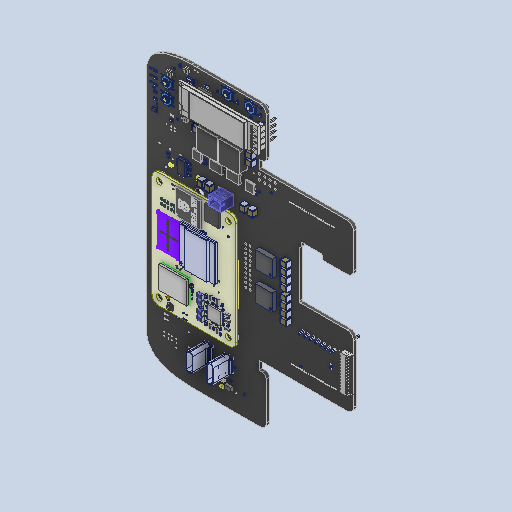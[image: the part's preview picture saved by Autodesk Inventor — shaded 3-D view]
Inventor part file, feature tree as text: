
AUTODESK INVENTOR PART (.ipt)
format: ipt  version: 2022 (Build 260153000, 153)  size: 57,300,480 bytes
history: native  units: mm
features: other x3626, sketch x2448, extrude x2
ambient origin geometry x8: Origin, YZ Plane, XZ Plane, XY Plane, X Axis, Y Axis, Z Axis, Center Point
bodies: Body1 (feature_tree), Body2 (feature_tree), Body3 (feature_tree), Body4 (feature_tree), Body5 (feature_tree), Body6 (feature_tree), Body7 (feature_tree), Body8 (feature_tree), Body9 (feature_tree), Body10 (feature_tree), Body11 (feature_tree), Body12 (feature_tree), Body13 (feature_tree), Body14 (feature_tree), Body15 (feature_tree), Body16 (feature_tree), Body17 (feature_tree), Body18 (feature_tree), Body19 (feature_tree), Body20 (feature_tree), Body21 (feature_tree), Body22 (feature_tree), Body23 (feature_tree), Body24 (feature_tree), Body25 (feature_tree), Body26 (feature_tree), Body27 (feature_tree), Body28 (feature_tree), Body29 (feature_tree), Body30 (feature_tree), Body31 (feature_tree), Body32 (feature_tree), Body33 (feature_tree), Body34 (feature_tree), Body35 (feature_tree), Body36 (feature_tree), Body37 (feature_tree), Body38 (feature_tree), Body39 (feature_tree), Body40 (feature_tree), Body41 (feature_tree), Body42 (feature_tree), Body43 (feature_tree), Body44 (feature_tree), Body45 (feature_tree), Body46 (feature_tree), Body47 (feature_tree), Body48 (feature_tree), Body49 (feature_tree), Body50 (feature_tree), Body51 (feature_tree), Body52 (feature_tree), Body53 (feature_tree), Body54 (feature_tree), Body55 (feature_tree), Body56 (feature_tree), Body57 (feature_tree), Body58 (feature_tree), Body59 (feature_tree), Body60 (feature_tree), Body61 (feature_tree), Body62 (feature_tree), Body63 (feature_tree), Body64 (feature_tree), Body65 (feature_tree), Body66 (feature_tree), Body67 (feature_tree), Body68 (feature_tree), Body69 (feature_tree), Body70 (feature_tree), Body71 (feature_tree), Body72 (feature_tree), Body73 (feature_tree), Body74 (feature_tree), Body75 (feature_tree), Body76 (feature_tree), Body77 (feature_tree), Body78 (feature_tree), Body79 (feature_tree), Body80 (feature_tree), Body81 (feature_tree), Body82 (feature_tree), Body83 (feature_tree), Body84 (feature_tree), Body85 (feature_tree), Body86 (feature_tree), Body87 (feature_tree), Body88 (feature_tree), Body89 (feature_tree), Body90 (feature_tree), Body91 (feature_tree), Body92 (feature_tree), Body93 (feature_tree), Body94 (feature_tree), Body95 (feature_tree), Body96 (feature_tree), Body97 (feature_tree), Body98 (feature_tree), Body99 (feature_tree), Body100 (feature_tree), Body101 (feature_tree), Body102 (feature_tree), Body103 (feature_tree), Body104 (feature_tree), Body105 (feature_tree), Body106 (feature_tree), Body107 (feature_tree), Body108 (feature_tree), Body109 (feature_tree), Body110 (feature_tree), Body111 (feature_tree), Body112 (feature_tree), Body113 (feature_tree), Body114 (feature_tree), Body115 (feature_tree), Body116 (feature_tree), Body117 (feature_tree), Body118 (feature_tree), Body119 (feature_tree), Body120 (feature_tree), Body121 (feature_tree), Body122 (feature_tree), Body123 (feature_tree), Body124 (feature_tree), Body125 (feature_tree), Body126 (feature_tree), Body127 (feature_tree), Body128 (feature_tree), Body129 (feature_tree), Body130 (feature_tree), Body131 (feature_tree), Body132 (feature_tree), Body133 (feature_tree), Body134 (feature_tree), Body135 (feature_tree), Body136 (feature_tree), Body137 (feature_tree), Body138 (feature_tree), Body139 (feature_tree), Body140 (feature_tree), Body141 (feature_tree), Body142 (feature_tree), Body143 (feature_tree), Body144 (feature_tree), Body145 (feature_tree), Body146 (feature_tree), Body147 (feature_tree), Body148 (feature_tree), Body149 (feature_tree), Body150 (feature_tree), Body151 (feature_tree), Body152 (feature_tree), Body153 (feature_tree), Body154 (feature_tree), Body155 (feature_tree), Body156 (feature_tree), Body157 (feature_tree), Body158 (feature_tree), Body159 (feature_tree), Body160 (feature_tree), Body161 (feature_tree), Body162 (feature_tree), Body163 (feature_tree), Body164 (feature_tree), Body165 (feature_tree), Body166 (feature_tree), Body167 (feature_tree), Body168 (feature_tree), Body169 (feature_tree), Body170 (feature_tree), Body171 (feature_tree), Body172 (feature_tree), Body173 (feature_tree), Body174 (feature_tree), Body175 (feature_tree), Body176 (feature_tree), Body177 (feature_tree), Body178 (feature_tree), Body179 (feature_tree), Body180 (feature_tree), Body181 (feature_tree), Body182 (feature_tree), Body183 (feature_tree), Body184 (feature_tree), Body185 (feature_tree), Body186 (feature_tree), Body187 (feature_tree), Body188 (feature_tree), Body189 (feature_tree), Body190 (feature_tree), Body191 (feature_tree), Body192 (feature_tree), Body193 (feature_tree), Body194 (feature_tree), Body195 (feature_tree), Body196 (feature_tree), Body197 (feature_tree), Body198 (feature_tree), Body199 (feature_tree), Body200 (feature_tree), Body201 (feature_tree), Body202 (feature_tree), Body203 (feature_tree), Body204 (feature_tree), Body205 (feature_tree), Body206 (feature_tree), Body207 (feature_tree), Body208 (feature_tree), Body209 (feature_tree), Body210 (feature_tree), Body211 (feature_tree), Body212 (feature_tree), Body213 (feature_tree), Body214 (feature_tree), Body215 (feature_tree), Body216 (feature_tree), Body217 (feature_tree), Body218 (feature_tree), Body219 (feature_tree), Body220 (feature_tree), Body221 (feature_tree), Body222 (feature_tree), Body223 (feature_tree), Body224 (feature_tree), Body225 (feature_tree), Body226 (feature_tree), Body227 (feature_tree), Body228 (feature_tree), Body229 (feature_tree), Body230 (feature_tree), Body231 (feature_tree), Body232 (feature_tree), Body233 (feature_tree), Body234 (feature_tree), Body235 (feature_tree), Body236 (feature_tree), Body237 (feature_tree), Body238 (feature_tree), Body239 (feature_tree), Body240 (feature_tree), Body241 (feature_tree), Body242 (feature_tree), Body243 (feature_tree), Body244 (feature_tree), Body245 (feature_tree), Body246 (feature_tree), Body247 (feature_tree), Body248 (feature_tree), Body249 (feature_tree), Body250 (feature_tree), Body251 (feature_tree), Body252 (feature_tree), Body253 (feature_tree), Body254 (feature_tree), Body255 (feature_tree), Body256 (feature_tree), Body257 (feature_tree), Body258 (feature_tree), Body259 (feature_tree), Body260 (feature_tree), Body261 (feature_tree), Body262 (feature_tree), Body263 (feature_tree), Body264 (feature_tree), Body265 (feature_tree), Body266 (feature_tree), Body267 (feature_tree), Body268 (feature_tree), Body269 (feature_tree), Body270 (feature_tree), Body271 (feature_tree), Body272 (feature_tree), Body273 (feature_tree), Body274 (feature_tree), Body275 (feature_tree), Body276 (feature_tree), Body277 (feature_tree), Body278 (feature_tree), Body279 (feature_tree), Body280 (feature_tree), Body281 (feature_tree), Body282 (feature_tree), Body283 (feature_tree), Body284 (feature_tree), Body285 (feature_tree), Body286 (feature_tree), Body287 (feature_tree), Body288 (feature_tree), Body289 (feature_tree), Body290 (feature_tree), Body291 (feature_tree), Body292 (feature_tree), Body293 (feature_tree), Body294 (feature_tree), Body295 (feature_tree), Body296 (feature_tree), Body297 (feature_tree), Body298 (feature_tree), Body299 (feature_tree), Body300 (feature_tree), Body301 (feature_tree), Body302 (feature_tree), Body303 (feature_tree), Body304 (feature_tree), Body305 (feature_tree), Body306 (feature_tree), Body307 (feature_tree), Body308 (feature_tree), Body309 (feature_tree), Body310 (feature_tree), Body311 (feature_tree), Body312 (feature_tree), Body313 (feature_tree), Body314 (feature_tree), Body315 (feature_tree), Body316 (feature_tree), Body317 (feature_tree), Body318 (feature_tree), Body319 (feature_tree), Body320 (feature_tree), Body321 (feature_tree), Body322 (feature_tree), Body323 (feature_tree), Body324 (feature_tree), Body325 (feature_tree), Body326 (feature_tree), Body327 (feature_tree), Body328 (feature_tree), Body329 (feature_tree), Body330 (feature_tree), Body331 (feature_tree), Body332 (feature_tree), Body333 (feature_tree), Body334 (feature_tree), Body335 (feature_tree), Body336 (feature_tree), Body337 (feature_tree), Body338 (feature_tree), Body339 (feature_tree), Body340 (feature_tree), Body341 (feature_tree), Body342 (feature_tree), Body343 (feature_tree), Body344 (feature_tree), Body345 (feature_tree), Body346 (feature_tree), Body347 (feature_tree), Body348 (feature_tree), Body349 (feature_tree), Body350 (feature_tree), Body351 (feature_tree), Body352 (feature_tree), Body353 (feature_tree), Body354 (feature_tree), Body355 (feature_tree), Body356 (feature_tree), Body357 (feature_tree), Body358 (feature_tree), Body359 (feature_tree), Body360 (feature_tree), Body361 (feature_tree), Body362 (feature_tree), Body363 (feature_tree), Body364 (feature_tree), Body365 (feature_tree), Body366 (feature_tree), Body367 (feature_tree), Body368 (feature_tree), Body369 (feature_tree), Body370 (feature_tree), Body371 (feature_tree), Body372 (feature_tree), Body373 (feature_tree), Body374 (feature_tree), Body375 (feature_tree), Body376 (feature_tree), Body377 (feature_tree), Body378 (feature_tree), Body379 (feature_tree), Body380 (feature_tree), Body381 (feature_tree), Body382 (feature_tree), Body383 (feature_tree), Body384 (feature_tree), Body385 (feature_tree), Body386 (feature_tree), Body387 (feature_tree), Body388 (feature_tree), Body389 (feature_tree), Body390 (feature_tree), Body391 (feature_tree), Body392 (feature_tree), Body393 (feature_tree), Body394 (feature_tree), Body395 (feature_tree), Body396 (feature_tree), Body397 (feature_tree), Body398 (feature_tree), Body399 (feature_tree), Body400 (feature_tree), Body401 (feature_tree), Body402 (feature_tree), Body403 (feature_tree), Body404 (feature_tree), Body405 (feature_tree), Body406 (feature_tree), Body407 (feature_tree), Body408 (feature_tree), Body409 (feature_tree), Body410 (feature_tree), Body411 (feature_tree), Body412 (feature_tree), Body413 (feature_tree), Body414 (feature_tree), Body415 (feature_tree), Body416 (feature_tree), Body417 (feature_tree), Body418 (feature_tree), Body419 (feature_tree), Body420 (feature_tree), Body421 (feature_tree), Body422 (feature_tree), Body423 (feature_tree), Body424 (feature_tree), Body425 (feature_tree), Body426 (feature_tree), Body427 (feature_tree), Body428 (feature_tree), Body429 (feature_tree), Body430 (feature_tree), Body431 (feature_tree), Body432 (feature_tree), Body433 (feature_tree), Body434 (feature_tree), Body435 (feature_tree), Body436 (feature_tree), Body437 (feature_tree), Body438 (feature_tree), Body439 (feature_tree), Body440 (feature_tree), Body441 (feature_tree), Body442 (feature_tree), Body443 (feature_tree), Body444 (feature_tree), Body445 (feature_tree), Body446 (feature_tree), Body447 (feature_tree), Body448 (feature_tree), Body449 (feature_tree), Body450 (feature_tree), Body451 (feature_tree), Body452 (feature_tree), Body453 (feature_tree), Body454 (feature_tree), Body455 (feature_tree), Body456 (feature_tree), Body457 (feature_tree), Body458 (feature_tree), Body459 (feature_tree), Body460 (feature_tree), Body461 (feature_tree), Body462 (feature_tree), Body463 (feature_tree), Body464 (feature_tree), Body465 (feature_tree), Body466 (feature_tree), Body467 (feature_tree), Body468 (feature_tree), Body469 (feature_tree), Body470 (feature_tree), Body471 (feature_tree), Body472 (feature_tree), Body473 (feature_tree), Body474 (feature_tree), Body475 (feature_tree), Body476 (feature_tree), Body477 (feature_tree), Body478 (feature_tree), Body479 (feature_tree), Body480 (feature_tree), Body481 (feature_tree), Body482 (feature_tree), Body483 (feature_tree), Body484 (feature_tree), Body485 (feature_tree), Body486 (feature_tree), Body487 (feature_tree), Body488 (feature_tree), Body489 (feature_tree), Body490 (feature_tree), Body491 (feature_tree), Body492 (feature_tree), Body493 (feature_tree), Body494 (feature_tree), Body495 (feature_tree), Body496 (feature_tree), Body497 (feature_tree), Body498 (feature_tree), Body499 (feature_tree), Body500 (feature_tree), Body501 (feature_tree), Body502 (feature_tree), Body503 (feature_tree), Body504 (feature_tree), Body505 (feature_tree), Body506 (feature_tree), Body507 (feature_tree), Body508 (feature_tree), Body509 (feature_tree), Body510 (feature_tree), Body511 (feature_tree), Body512 (feature_tree), Body513 (feature_tree), Body514 (feature_tree), Body515 (feature_tree), Body516 (feature_tree), Body517 (feature_tree), Body518 (feature_tree), Body519 (feature_tree), Body520 (feature_tree), Body521 (feature_tree), Body522 (feature_tree), Body523 (feature_tree), Body524 (feature_tree), Body525 (feature_tree), Body526 (feature_tree), Body527 (feature_tree), Body528 (feature_tree), Body529 (feature_tree), Body530 (feature_tree), Body531 (feature_tree), Body532 (feature_tree), Body533 (feature_tree), Body534 (feature_tree), Body535 (feature_tree), Body536 (feature_tree), Body537 (feature_tree), Body538 (feature_tree), Body539 (feature_tree), Body540 (feature_tree), Body541 (feature_tree), Body542 (feature_tree), Body543 (feature_tree), Body544 (feature_tree), Body545 (feature_tree), Body546 (feature_tree), Body547 (feature_tree), Body548 (feature_tree), Body549 (feature_tree), Body550 (feature_tree), Body551 (feature_tree), Body552 (feature_tree), Body553 (feature_tree), Body554 (feature_tree), Body555 (feature_tree), Body556 (feature_tree), Body557 (feature_tree), Body558 (feature_tree), Body559 (feature_tree), Body560 (feature_tree), Body561 (feature_tree), Body562 (feature_tree), Body563 (feature_tree), Body564 (feature_tree), Body565 (feature_tree), Body566 (feature_tree), Body567 (feature_tree), Body568 (feature_tree), Body569 (feature_tree), Body570 (feature_tree), Body571 (feature_tree), Body572 (feature_tree), Body573 (feature_tree), Body574 (feature_tree), Body575 (feature_tree), Body576 (feature_tree), Body577 (feature_tree), Body578 (feature_tree), Body579 (feature_tree), Body580 (feature_tree), Body581 (feature_tree), Body582 (feature_tree), Body583 (feature_tree), Body584 (feature_tree), Body585 (feature_tree), Body586 (feature_tree), Body587 (feature_tree), Body588 (feature_tree), Body589 (feature_tree), Body590 (feature_tree), Body591 (feature_tree), Body592 (feature_tree), Body593 (feature_tree), Body594 (feature_tree), Body595 (feature_tree), Body596 (feature_tree), Body597 (feature_tree), Body598 (feature_tree), Body599 (feature_tree), Body600 (feature_tree), Body601 (feature_tree), Body602 (feature_tree), Body603 (feature_tree), Body604 (feature_tree), Body605 (feature_tree), Body606 (feature_tree), Body607 (feature_tree), Body608 (feature_tree), Body609 (feature_tree), Body610 (feature_tree), Body611 (feature_tree), Body612 (feature_tree), Body613 (feature_tree), Body614 (feature_tree), Body615 (feature_tree), Body616 (feature_tree), Body617 (feature_tree), Body618 (feature_tree), Body619 (feature_tree), Body620 (feature_tree), Body621 (feature_tree), Body622 (feature_tree), Body623 (feature_tree), Body624 (feature_tree), Body625 (feature_tree), Body626 (feature_tree), Body627 (feature_tree), Body628 (feature_tree), Body629 (feature_tree), Body630 (feature_tree), Body631 (feature_tree), Body632 (feature_tree), Body633 (feature_tree), Body634 (feature_tree), Body635 (feature_tree), Body636 (feature_tree), Body637 (feature_tree), Body638 (feature_tree), Body639 (feature_tree), Body640 (feature_tree), Body641 (feature_tree), Body642 (feature_tree), Body643 (feature_tree), Body644 (feature_tree), Body645 (feature_tree), Body646 (feature_tree), Body647 (feature_tree), Body648 (feature_tree), Body649 (feature_tree), Body650 (feature_tree), Body651 (feature_tree), Body652 (feature_tree), Body653 (feature_tree), Body654 (feature_tree), Body655 (feature_tree), Body656 (feature_tree), Body657 (feature_tree), Body658 (feature_tree), Body659 (feature_tree), Body660 (feature_tree), Body661 (feature_tree), Body662 (feature_tree), Body663 (feature_tree), Body664 (feature_tree), Body665 (feature_tree), Body666 (feature_tree), Body667 (feature_tree), Body668 (feature_tree), Body669 (feature_tree), Body670 (feature_tree), Body671 (feature_tree), Body672 (feature_tree), Body673 (feature_tree), Body674 (feature_tree), Body675 (feature_tree), Body676 (feature_tree), Body677 (feature_tree), Body678 (feature_tree), Body679 (feature_tree), Body680 (feature_tree), Body681 (feature_tree), Body682 (feature_tree), Body683 (feature_tree), Body684 (feature_tree), Body685 (feature_tree), Body686 (feature_tree), Body687 (feature_tree), Body688 (feature_tree), Body689 (feature_tree), Body690 (feature_tree), Body691 (feature_tree), Body692 (feature_tree), Body693 (feature_tree), Body694 (feature_tree), Body695 (feature_tree), Body696 (feature_tree), Body697 (feature_tree), Body698 (feature_tree), Body699 (feature_tree), Body700 (feature_tree), Body701 (feature_tree), Body702 (feature_tree), Body703 (feature_tree), Body704 (feature_tree), Body705 (feature_tree), Body706 (feature_tree), Body707 (feature_tree), Body708 (feature_tree), Body709 (feature_tree), Body710 (feature_tree), Body711 (feature_tree), Body712 (feature_tree), Body713 (feature_tree), Body714 (feature_tree), Body715 (feature_tree), Body716 (feature_tree), Body717 (feature_tree), Body718 (feature_tree), Body719 (feature_tree), Body720 (feature_tree), Body721 (feature_tree), Body722 (feature_tree), Body723 (feature_tree), Body724 (feature_tree), Body725 (feature_tree), Body726 (feature_tree), Body727 (feature_tree), Body728 (feature_tree), Body729 (feature_tree), Body730 (feature_tree), Body731 (feature_tree), Body732 (feature_tree), Body733 (feature_tree), Body734 (feature_tree), Body735 (feature_tree), Body736 (feature_tree), Body737 (feature_tree), Body738 (feature_tree), Body739 (feature_tree), Body740 (feature_tree), Body741 (feature_tree), Body742 (feature_tree), Body743 (feature_tree), Body744 (feature_tree), Body745 (feature_tree), Body746 (feature_tree), Body747 (feature_tree), Body748 (feature_tree), Body749 (feature_tree), Body750 (feature_tree), Body751 (feature_tree), Body752 (feature_tree), Body753 (feature_tree), Body754 (feature_tree), Body755 (feature_tree), Body756 (feature_tree), Body757 (feature_tree), Body758 (feature_tree), Body759 (feature_tree), Body760 (feature_tree), Body761 (feature_tree), Body762 (feature_tree), Body763 (feature_tree), Body764 (feature_tree), Body765 (feature_tree), Body766 (feature_tree), Body767 (feature_tree), Body768 (feature_tree), Body769 (feature_tree), Body770 (feature_tree), Body771 (feature_tree), Body772 (feature_tree), Body773 (feature_tree), Body774 (feature_tree), Body775 (feature_tree), Body776 (feature_tree), Body777 (feature_tree), Body778 (feature_tree), Body779 (feature_tree), Body780 (feature_tree), Body781 (feature_tree), Body782 (feature_tree), Body783 (feature_tree), Body784 (feature_tree), Body785 (feature_tree), Body786 (feature_tree), Body787 (feature_tree), Body788 (feature_tree), Body789 (feature_tree), Body790 (feature_tree), Body791 (feature_tree), Body792 (feature_tree), Body793 (feature_tree), Body794 (feature_tree), Body795 (feature_tree), Body796 (feature_tree), Body797 (feature_tree), Body798 (feature_tree), Body799 (feature_tree), Body800 (feature_tree), Body801 (feature_tree), Body802 (feature_tree), Body803 (feature_tree), Body804 (feature_tree), Body805 (feature_tree), Body806 (feature_tree), Body807 (feature_tree), Body808 (feature_tree), Body809 (feature_tree), Body810 (feature_tree), Body811 (feature_tree), Body812 (feature_tree), Body813 (feature_tree), Body814 (feature_tree), Body815 (feature_tree), Body816 (feature_tree), Body817 (feature_tree), Body818 (feature_tree), Body819 (feature_tree), Body820 (feature_tree), Body821 (feature_tree), Body822 (feature_tree), Body823 (feature_tree), Body824 (feature_tree), Body825 (feature_tree), Body826 (feature_tree), Body827 (feature_tree), Body828 (feature_tree), Body829 (feature_tree), Body830 (feature_tree), Body831 (feature_tree), Body832 (feature_tree), Body833 (feature_tree), Body834 (feature_tree), Body835 (feature_tree), Body836 (feature_tree), Body837 (feature_tree), Body838 (feature_tree), Body839 (feature_tree), Body840 (feature_tree), Body841 (feature_tree), Body842 (feature_tree), Body843 (feature_tree), Body844 (feature_tree), Body845 (feature_tree), Body846 (feature_tree), Body847 (feature_tree), Body848 (feature_tree), Body849 (feature_tree), Body850 (feature_tree), Body851 (feature_tree), Body852 (feature_tree), Body853 (feature_tree), Body854 (feature_tree), Body855 (feature_tree), Body856 (feature_tree), Body857 (feature_tree), Body858 (feature_tree), Body859 (feature_tree), Body860 (feature_tree), Body861 (feature_tree), Body862 (feature_tree), Body863 (feature_tree), Body864 (feature_tree), Body865 (feature_tree), Body866 (feature_tree), Body867 (feature_tree), Body868 (feature_tree), Body869 (feature_tree), Body870 (feature_tree), Body871 (feature_tree), Body872 (feature_tree), Body873 (feature_tree), Body874 (feature_tree), Body875 (feature_tree), Body876 (feature_tree), Body877 (feature_tree), Body878 (feature_tree), Body879 (feature_tree), Body880 (feature_tree), Body881 (feature_tree), Body882 (feature_tree), Body883 (feature_tree), Body884 (feature_tree), Body885 (feature_tree), Body886 (feature_tree), Body887 (feature_tree), Body888 (feature_tree), Body889 (feature_tree), Body890 (feature_tree), Body891 (feature_tree), Body892 (feature_tree), Body893 (feature_tree), Body894 (feature_tree), Body895 (feature_tree), Body896 (feature_tree), Body897 (feature_tree), Body898 (feature_tree), Body899 (feature_tree), Body900 (feature_tree), Body901 (feature_tree), Body902 (feature_tree), Body903 (feature_tree), Body904 (feature_tree), Body905 (feature_tree), Body906 (feature_tree), Body907 (feature_tree), Body908 (feature_tree), Body909 (feature_tree), Body910 (feature_tree), Body911 (feature_tree), Body912 (feature_tree), Body913 (feature_tree), Body914 (feature_tree), Body915 (feature_tree), Body916 (feature_tree), Body917 (feature_tree), Body918 (feature_tree), Body919 (feature_tree), Body920 (feature_tree), Body921 (feature_tree), Body922 (feature_tree), Body923 (feature_tree), Body924 (feature_tree), Body925 (feature_tree), Body926 (feature_tree), Body927 (feature_tree), Body928 (feature_tree), Body929 (feature_tree), Body930 (feature_tree), Body931 (feature_tree), Body932 (feature_tree), Body933 (feature_tree), Body934 (feature_tree), Body935 (feature_tree), Body936 (feature_tree), Body937 (feature_tree), Body938 (feature_tree), Body939 (feature_tree), Body940 (feature_tree), Body941 (feature_tree), Body942 (feature_tree), Body943 (feature_tree), Body944 (feature_tree), Body945 (feature_tree), Body946 (feature_tree), Body947 (feature_tree), Body948 (feature_tree), Body949 (feature_tree), Body950 (feature_tree), Body951 (feature_tree), Body952 (feature_tree), Body953 (feature_tree), Body954 (feature_tree), Body955 (feature_tree), Body956 (feature_tree), Body957 (feature_tree), Body958 (feature_tree), Body959 (feature_tree), Body960 (feature_tree), Body961 (feature_tree), Body962 (feature_tree), Body963 (feature_tree), Body964 (feature_tree), Body965 (feature_tree), Body966 (feature_tree), Body967 (feature_tree), Body968 (feature_tree), Body969 (feature_tree), Body970 (feature_tree), Body971 (feature_tree), Body972 (feature_tree), Body973 (feature_tree), Body974 (feature_tree), Body975 (feature_tree), Body976 (feature_tree), Body977 (feature_tree), Body978 (feature_tree), Body979 (feature_tree), Body980 (feature_tree), Body981 (feature_tree), Body982 (feature_tree), Body983 (feature_tree), Body984 (feature_tree), Body985 (feature_tree), Body986 (feature_tree), Body987 (feature_tree), Body988 (feature_tree), Body989 (feature_tree), Body990 (feature_tree), Body991 (feature_tree), Body992 (feature_tree), Body993 (feature_tree), Body994 (feature_tree), Body995 (feature_tree), Body996 (feature_tree), Body997 (feature_tree), Body998 (feature_tree), Body999 (feature_tree), Body1000 (feature_tree), Body1001 (feature_tree), Body1002 (feature_tree), Body1003 (feature_tree), Body1004 (feature_tree), Body1005 (feature_tree), Body1006 (feature_tree), Body1007 (feature_tree), Body1008 (feature_tree), Body1009 (feature_tree), Body1010 (feature_tree), Body1011 (feature_tree), Body1012 (feature_tree), Body1013 (feature_tree), Body1014 (feature_tree), Body1015 (feature_tree), Body1016 (feature_tree), Body1017 (feature_tree), Body1018 (feature_tree), Body1019 (feature_tree), Body1020 (feature_tree), Body1021 (feature_tree), Body1022 (feature_tree), Body1023 (feature_tree), Body1024 (feature_tree), Body1025 (feature_tree), Body1026 (feature_tree), Body1027 (feature_tree), Body1028 (feature_tree), Body1029 (feature_tree), Body1030 (feature_tree), Body1031 (feature_tree), Body1032 (feature_tree), Body1033 (feature_tree), Body1034 (feature_tree), Body1035 (feature_tree), Body1036 (feature_tree), Body1037 (feature_tree), Body1038 (feature_tree), Body1039 (feature_tree), Body1040 (feature_tree), Body1041 (feature_tree), Body1042 (feature_tree), Body1043 (feature_tree), Body1044 (feature_tree), Body1045 (feature_tree), Body1046 (feature_tree), Body1047 (feature_tree), Body1048 (feature_tree), Body1049 (feature_tree), Body1050 (feature_tree), Body1051 (feature_tree), Body1052 (feature_tree), Body1053 (feature_tree), Body1054 (feature_tree), Body1055 (feature_tree), Body1056 (feature_tree), Body1057 (feature_tree), Body1058 (feature_tree), Body1059 (feature_tree), Body1060 (feature_tree), Body1061 (feature_tree), Body1062 (feature_tree), Body1063 (feature_tree), Body1064 (feature_tree), Body1065 (feature_tree), Body1066 (feature_tree), Body1067 (feature_tree), Body1068 (feature_tree), Body1069 (feature_tree), Body1070 (feature_tree), Body1071 (feature_tree), Body1072 (feature_tree), Body1073 (feature_tree), Body1074 (feature_tree), Body1075 (feature_tree), Body1076 (feature_tree), Body1077 (feature_tree), Body1078 (feature_tree), Body1079 (feature_tree), Body1080 (feature_tree), Body1081 (feature_tree), Body1082 (feature_tree), Body1083 (feature_tree), Body1084 (feature_tree), Body1085 (feature_tree), Body1086 (feature_tree), Body1087 (feature_tree), Body1088 (feature_tree), Body1089 (feature_tree), Body1090 (feature_tree), Body1091 (feature_tree), Body1092 (feature_tree), Body1093 (feature_tree), Body1094 (feature_tree), Body1095 (feature_tree), Body1096 (feature_tree), Body1097 (feature_tree), Body1098 (feature_tree), Body1099 (feature_tree), Body1100 (feature_tree), Body1101 (feature_tree), Body1102 (feature_tree), Body1103 (feature_tree), Body1104 (feature_tree), Body1105 (feature_tree), Body1106 (feature_tree), Body1107 (feature_tree), Body1108 (feature_tree), Body1109 (feature_tree), Body1110 (feature_tree), Body1111 (feature_tree), Body1112 (feature_tree), Body1113 (feature_tree), Body1114 (feature_tree), Body1115 (feature_tree), Body1116 (feature_tree), Body1117 (feature_tree), Body1118 (feature_tree), Body1119 (feature_tree), Body1120 (feature_tree), Body1121 (feature_tree), Body1122 (feature_tree), Body1123 (feature_tree), Body1124 (feature_tree), Body1125 (feature_tree), Body1126 (feature_tree), Body1127 (feature_tree), Body1128 (feature_tree), Body1129 (feature_tree), Body1130 (feature_tree), Body1131 (feature_tree), Body1132 (feature_tree), Body1133 (feature_tree), Body1134 (feature_tree), Body1135 (feature_tree), Body1136 (feature_tree), Body1137 (feature_tree), Body1138 (feature_tree), Body1139 (feature_tree), Body1140 (feature_tree), Body1141 (feature_tree), Body1142 (feature_tree), Body1143 (feature_tree), Body1144 (feature_tree), Body1145 (feature_tree), Body1146 (feature_tree), Body1147 (feature_tree), Body1148 (feature_tree), Body1149 (feature_tree), Body1150 (feature_tree), Body1151 (feature_tree), Body1152 (feature_tree), Body1153 (feature_tree), Body1154 (feature_tree), Body1155 (feature_tree), Body1156 (feature_tree), Body1157 (feature_tree), Body1158 (feature_tree), Body1159 (feature_tree), Body1160 (feature_tree), Body1161 (feature_tree), Body1162 (feature_tree), Body1163 (feature_tree), Body1164 (feature_tree), Body1165 (feature_tree), Body1166 (feature_tree), Body1167 (feature_tree), Body1168 (feature_tree), Body1169 (feature_tree), Body1170 (feature_tree), Body1171 (feature_tree), Body1172 (feature_tree), Body1173 (feature_tree), Body1174 (feature_tree), Body1175 (feature_tree), Body1176 (feature_tree), Body1177 (feature_tree), Body1178 (feature_tree), Body1179 (feature_tree), Body1180 (feature_tree), Body1181 (feature_tree), Body1182 (feature_tree), Body1183 (feature_tree), Body1184 (feature_tree), Body1185 (feature_tree), Body1186 (feature_tree), Body1187 (feature_tree), Body1188 (feature_tree), Body1189 (feature_tree), Body1190 (feature_tree), Body1191 (feature_tree), Body1192 (feature_tree), Body1193 (feature_tree), Body1194 (feature_tree), Body1195 (feature_tree), Body1196 (feature_tree), Body1197 (feature_tree), Body1198 (feature_tree), Body1199 (feature_tree), Body1200 (feature_tree), Body1201 (feature_tree), Body1202 (feature_tree), Body1203 (feature_tree), Body1204 (feature_tree), Body1205 (feature_tree), Body1206 (feature_tree), Body1207 (feature_tree), Body1208 (feature_tree), Body1209 (feature_tree), Body1210 (feature_tree), Body1211 (feature_tree), Body1212 (feature_tree), Body1213 (feature_tree), Body1214 (feature_tree), Body1215 (feature_tree), Body1216 (feature_tree), Body1217 (feature_tree), Body1218 (feature_tree), Body1219 (feature_tree), Body1220 (feature_tree), Body1221 (feature_tree), Body1222 (feature_tree), Body1223 (feature_tree), Body1224 (feature_tree), Body1225 (feature_tree), Body1226 (feature_tree), Body1227 (feature_tree), Body1228 (feature_tree), Body1229 (feature_tree), Body1230 (feature_tree), Body1231 (feature_tree), Body1232 (feature_tree), Body1233 (feature_tree), Body1234 (feature_tree), Body1235 (feature_tree), Body1236 (feature_tree), Body1237 (feature_tree), Body1238 (feature_tree), Body1239 (feature_tree), Body1240 (feature_tree), Body1241 (feature_tree), Body1242 (feature_tree), Body1243 (feature_tree), Body1244 (feature_tree), Body1245 (feature_tree), Body1246 (feature_tree), Body1247 (feature_tree), Body1248 (feature_tree), Body1249 (feature_tree), Body1250 (feature_tree), Body1251 (feature_tree), Body1252 (feature_tree), Body1253 (feature_tree), Body1254 (feature_tree), Body1255 (feature_tree), Body1256 (feature_tree), Body1257 (feature_tree), Body1258 (feature_tree), Body1259 (feature_tree), Body1260 (feature_tree), Body1261 (feature_tree), Body1262 (feature_tree), Body1263 (feature_tree), Body1264 (feature_tree), Body1265 (feature_tree), Body1266 (feature_tree), Body1267 (feature_tree), Body1268 (feature_tree), Body1269 (feature_tree), Body1270 (feature_tree), Body1271 (feature_tree), Body1272 (feature_tree), Body1273 (feature_tree), Body1274 (feature_tree), Body1275 (feature_tree), Body1276 (feature_tree), Body1277 (feature_tree), Body1278 (feature_tree), Body1279 (feature_tree), Body1280 (feature_tree), Body1281 (feature_tree), Body1282 (feature_tree), Body1283 (feature_tree), Body1284 (feature_tree), Body1285 (feature_tree), Body1286 (feature_tree), Body1287 (feature_tree), Body1288 (feature_tree), Body1289 (feature_tree), Body1290 (feature_tree), Body1291 (feature_tree), Body1292 (feature_tree), Body1293 (feature_tree), Body1294 (feature_tree), Body1295 (feature_tree), Body1296 (feature_tree), Body1297 (feature_tree), Body1298 (feature_tree), Body1299 (feature_tree), Body1300 (feature_tree), Body1301 (feature_tree), Body1302 (feature_tree), Body1303 (feature_tree), Body1304 (feature_tree), Body1305 (feature_tree), Body1306 (feature_tree), Body1307 (feature_tree), Body1308 (feature_tree), Body1309 (feature_tree), Body1310 (feature_tree), Body1311 (feature_tree), Body1312 (feature_tree), Body1313 (feature_tree), Body1314 (feature_tree), Body1315 (feature_tree), Body1316 (feature_tree), Body1317 (feature_tree), Body1318 (feature_tree), Body1319 (feature_tree), Body1320 (feature_tree), Body1321 (feature_tree), Body1322 (feature_tree), Body1323 (feature_tree), Body1324 (feature_tree), Body1325 (feature_tree), Body1326 (feature_tree), Body1327 (feature_tree), Body1328 (feature_tree), Body1329 (feature_tree), Body1330 (feature_tree), Body1331 (feature_tree), Body1332 (feature_tree), Body1333 (feature_tree), Body1334 (feature_tree), Body1335 (feature_tree), Body1336 (feature_tree), Body1337 (feature_tree), Body1338 (feature_tree), Body1339 (feature_tree), Body1340 (feature_tree), Body1341 (feature_tree), Body1342 (feature_tree), Body1343 (feature_tree), Body1344 (feature_tree), Body1345 (feature_tree), Body1346 (feature_tree), Body1347 (feature_tree), Body1348 (feature_tree), Body1349 (feature_tree), Body1350 (feature_tree), Body1351 (feature_tree), Body1352 (feature_tree), Body1353 (feature_tree), Body1354 (feature_tree), Body1355 (feature_tree), Body1356 (feature_tree), Body1357 (feature_tree), Body1358 (feature_tree), Body1359 (feature_tree), Body1360 (feature_tree), Body1361 (feature_tree), Body1362 (feature_tree), Body1363 (feature_tree), Body1364 (feature_tree), Body1365 (feature_tree), Body1366 (feature_tree), Body1367 (feature_tree), Body1368 (feature_tree), Body1369 (feature_tree), Body1370 (feature_tree), Body1371 (feature_tree), Body1372 (feature_tree), Body1373 (feature_tree), Body1374 (feature_tree), Body1375 (feature_tree), Body1376 (feature_tree), Body1377 (feature_tree), Body1378 (feature_tree), Body1379 (feature_tree), Body1380 (feature_tree), Body1381 (feature_tree), Body1382 (feature_tree), Body1383 (feature_tree), Body1384 (feature_tree), Body1385 (feature_tree), Body1386 (feature_tree), Body1387 (feature_tree), Body1388 (feature_tree), Body1389 (feature_tree), Body1390 (feature_tree), Body1391 (feature_tree), Body1392 (feature_tree), Body1393 (feature_tree), Body1394 (feature_tree), Body1395 (feature_tree), Body1396 (feature_tree), Body1397 (feature_tree), Body1398 (feature_tree), Body1399 (feature_tree), Body1400 (feature_tree), Body1401 (feature_tree), Body1402 (feature_tree), Body1403 (feature_tree), Body1404 (feature_tree), Body1405 (feature_tree), Body1406 (feature_tree), Body1407 (feature_tree), Body1408 (feature_tree), Body1409 (feature_tree), Body1410 (feature_tree), Body1411 (feature_tree), Body1412 (feature_tree), Body1413 (feature_tree), Body1414 (feature_tree), Body1415 (feature_tree), Body1416 (feature_tree), Body1417 (feature_tree), Body1418 (feature_tree), Body1419 (feature_tree), Body1420 (feature_tree), Body1421 (feature_tree), Body1422 (feature_tree), Body1423 (feature_tree), Body1424 (feature_tree), Body1425 (feature_tree), Body1426 (feature_tree), Body1427 (feature_tree), Body1428 (feature_tree), Body1429 (feature_tree), Body1430 (feature_tree), Body1431 (feature_tree), Body1432 (feature_tree), Body1433 (feature_tree), Body1434 (feature_tree), Body1435 (feature_tree), Body1436 (feature_tree), Body1437 (feature_tree), Body1438 (feature_tree), Body1439 (feature_tree), Body1440 (feature_tree), Body1441 (feature_tree), Body1442 (feature_tree), Body1443 (feature_tree), Body1444 (feature_tree), Body1445 (feature_tree), Body1446 (feature_tree), Body1447 (feature_tree), Body1448 (feature_tree), Body1449 (feature_tree), Body1450 (feature_tree), Body1451 (feature_tree), Body1452 (feature_tree), Body1453 (feature_tree), Body1454 (feature_tree), Body1455 (feature_tree), Body1456 (feature_tree), Body1457 (feature_tree), Body1458 (feature_tree), Body1459 (feature_tree), Body1460 (feature_tree), Body1461 (feature_tree), Body1462 (feature_tree), Body1463 (feature_tree), Body1464 (feature_tree), Body1465 (feature_tree), Body1466 (feature_tree), Body1467 (feature_tree), Body1468 (feature_tree), Body1469 (feature_tree), Body1470 (feature_tree), Body1471 (feature_tree), Body1472 (feature_tree), Body1473 (feature_tree), Body1474 (feature_tree), Body1475 (feature_tree), Body1476 (feature_tree), Body1477 (feature_tree), Body1478 (feature_tree), Body1479 (feature_tree), Body1480 (feature_tree), Body1481 (feature_tree), Body1482 (feature_tree), Body1483 (feature_tree), Body1484 (feature_tree), Body1485 (feature_tree), Body1486 (feature_tree), Body1487 (feature_tree), Body1488 (feature_tree), Body1489 (feature_tree), Body1490 (feature_tree), Body1491 (feature_tree), Body1492 (feature_tree), Body1493 (feature_tree), Body1494 (feature_tree), Body1495 (feature_tree), Body1496 (feature_tree), Body1497 (feature_tree), Body1498 (feature_tree), Body1499 (feature_tree), Body1500 (feature_tree), Body1501 (feature_tree), Body1502 (feature_tree), Body1503 (feature_tree), Body1504 (feature_tree), Body1505 (feature_tree), Body1506 (feature_tree), Body1507 (feature_tree), Body1508 (feature_tree), Body1509 (feature_tree), Body1510 (feature_tree), Body1511 (feature_tree), Body1512 (feature_tree), Body1513 (feature_tree), Body1514 (feature_tree), Body1515 (feature_tree), Body1516 (feature_tree), Body1517 (feature_tree), Body1518 (feature_tree), Body1519 (feature_tree), Body1520 (feature_tree), Body1521 (feature_tree), Body1522 (feature_tree), Body1523 (feature_tree), Body1524 (feature_tree), Body1525 (feature_tree), Body1526 (feature_tree), Body1527 (feature_tree), Body1528 (feature_tree), Body1529 (feature_tree), Body1530 (feature_tree), Body1531 (feature_tree), Body1532 (feature_tree), Body1533 (feature_tree), Body1534 (feature_tree), Body1535 (feature_tree), Body1536 (feature_tree), Body1537 (feature_tree), Body1538 (feature_tree), Body1539 (feature_tree), Body1540 (feature_tree), Body1541 (feature_tree), Body1542 (feature_tree), Body1543 (feature_tree), Body1544 (feature_tree), Body1545 (feature_tree), Body1546 (feature_tree), Body1547 (feature_tree), Body1548 (feature_tree), Body1549 (feature_tree), Body1550 (feature_tree), Body1551 (feature_tree), Body1552 (feature_tree), Body1553 (feature_tree), Body1554 (feature_tree), Body1555 (feature_tree), Body1556 (feature_tree), Body1557 (feature_tree), Body1558 (feature_tree), Body1559 (feature_tree), Body1560 (feature_tree), Body1561 (feature_tree), Body1562 (feature_tree), Body1563 (feature_tree), Body1564 (feature_tree), Body1565 (feature_tree), Body1566 (feature_tree), Body1567 (feature_tree), Body1568 (feature_tree), Body1569 (feature_tree), Body1570 (feature_tree), Body1571 (feature_tree), Body1572 (feature_tree), Body1573 (feature_tree), Body1574 (feature_tree), Body1575 (feature_tree), Body1576 (feature_tree), Body1577 (feature_tree), Body1578 (feature_tree), Body1579 (feature_tree), Body1580 (feature_tree), Body1581 (feature_tree), Body1582 (feature_tree), Body1583 (feature_tree), Body1584 (feature_tree), Body1585 (feature_tree), Body1586 (feature_tree), Body1587 (feature_tree), Body1588 (feature_tree), Body1589 (feature_tree), Body1590 (feature_tree), Body1591 (feature_tree), Body1592 (feature_tree), Body1593 (feature_tree), Body1594 (feature_tree), Body1595 (feature_tree), Body1596 (feature_tree), Body1597 (feature_tree), Body1598 (feature_tree), Body1599 (feature_tree), Body1600 (feature_tree), Body1601 (feature_tree), Body1602 (feature_tree), Body1603 (feature_tree), Body1604 (feature_tree), Body1605 (feature_tree), Body1606 (feature_tree), Body1607 (feature_tree), Body1608 (feature_tree), Body1609 (feature_tree), Body1610 (feature_tree), Body1611 (feature_tree), Body1612 (feature_tree), Body1613 (feature_tree), Body1614 (feature_tree), Body1615 (feature_tree), Body1616 (feature_tree), Body1617 (feature_tree), Body1618 (feature_tree), Body1619 (feature_tree), Body1620 (feature_tree), Body1621 (feature_tree), Body1622 (feature_tree), Body1623 (feature_tree), Body1624 (feature_tree), Body1625 (feature_tree), Body1626 (feature_tree), Body1627 (feature_tree), Body1628 (feature_tree), Body1629 (feature_tree), Body1630 (feature_tree), Body1631 (feature_tree), Body1632 (feature_tree), Body1633 (feature_tree), Body1634 (feature_tree), Body1635 (feature_tree), Body1636 (feature_tree), Body1637 (feature_tree), Body1638 (feature_tree), Body1639 (feature_tree), Body1640 (feature_tree), Body1641 (feature_tree), Body1642 (feature_tree), Body1643 (feature_tree), Body1644 (feature_tree), Body1645 (feature_tree), Body1646 (feature_tree), Body1647 (feature_tree), Body1648 (feature_tree), Body1649 (feature_tree), Body1650 (feature_tree), Body1651 (feature_tree), Body1652 (feature_tree), Body1653 (feature_tree), Body1654 (feature_tree), Body1655 (feature_tree), Body1656 (feature_tree), Body1657 (feature_tree), Body1658 (feature_tree), Body1659 (feature_tree), Body1660 (feature_tree), Body1661 (feature_tree), Body1662 (feature_tree), Body1663 (feature_tree), Body1664 (feature_tree), Body1665 (feature_tree), Body1666 (feature_tree), Body1667 (feature_tree), Body1668 (feature_tree), Body1669 (feature_tree), Body1670 (feature_tree), Body1671 (feature_tree), Body1672 (feature_tree), Body1673 (feature_tree), Body1674 (feature_tree), Body1675 (feature_tree), Body1676 (feature_tree), Body1677 (feature_tree), Body1678 (feature_tree), Body1679 (feature_tree), Body1680 (feature_tree), Body1681 (feature_tree), Body1682 (feature_tree), Body1683 (feature_tree), Body1684 (feature_tree), Body1685 (feature_tree), Body1686 (feature_tree), Body1687 (feature_tree), Body1688 (feature_tree), Body1689 (feature_tree), Body1690 (feature_tree), Body1691 (feature_tree), Body1692 (feature_tree), Body1693 (feature_tree), Body1694 (feature_tree), Body1695 (feature_tree), Body1696 (feature_tree), Body1697 (feature_tree), Body1698 (feature_tree), Body1699 (feature_tree), Body1700 (feature_tree), Body1701 (feature_tree), Body1702 (feature_tree), Body1703 (feature_tree), Body1704 (feature_tree), Body1705 (feature_tree), Body1706 (feature_tree), Body1707 (feature_tree), Body1708 (feature_tree), Body1709 (feature_tree), Body1710 (feature_tree), Body1711 (feature_tree), Body1712 (feature_tree), Body1713 (feature_tree), Body1714 (feature_tree), Body1715 (feature_tree), Body1716 (feature_tree), Body1717 (feature_tree), Body1718 (feature_tree), Body1719 (feature_tree), Body1720 (feature_tree), Body1721 (feature_tree), Body1722 (feature_tree), Body1723 (feature_tree), Body1724 (feature_tree), Body1725 (feature_tree), Body1726 (feature_tree), Body1727 (feature_tree), Body1728 (feature_tree), Body1729 (feature_tree), Body1730 (feature_tree), Body1731 (feature_tree), Body1732 (feature_tree), Body1733 (feature_tree), Body1734 (feature_tree), Body1735 (feature_tree), Body1736 (feature_tree), Body1737 (feature_tree), Body1738 (feature_tree), Body1739 (feature_tree), Body1740 (feature_tree), Body1741 (feature_tree), Body1742 (feature_tree), Body1743 (feature_tree), Body1744 (feature_tree), Body1745 (feature_tree), Body1746 (feature_tree), Body1747 (feature_tree), Body1748 (feature_tree), Body1749 (feature_tree), Body1750 (feature_tree), Body1751 (feature_tree), Body1752 (feature_tree), Body1753 (feature_tree), Body1754 (feature_tree), Body1755 (feature_tree), Body1756 (feature_tree), Body1757 (feature_tree), Body1758 (feature_tree), Body1759 (feature_tree), Body1760 (feature_tree), Body1761 (feature_tree), Body1762 (feature_tree), Body1763 (feature_tree), Body1764 (feature_tree), Body1765 (feature_tree), Body1766 (feature_tree), Body1767 (feature_tree), Body1768 (feature_tree), Body1769 (feature_tree), Body1770 (feature_tree), Body1771 (feature_tree), Body1772 (feature_tree), Body1773 (feature_tree), Body1774 (feature_tree), Body1775 (feature_tree), Body1776 (feature_tree), Body1777 (feature_tree), Body1778 (feature_tree), Body1779 (feature_tree), Body1780 (feature_tree), Body1781 (feature_tree), Body1782 (feature_tree), Body1783 (feature_tree), Body1784 (feature_tree), Body1785 (feature_tree), Body1786 (feature_tree), Body1787 (feature_tree), Body1788 (feature_tree), Body1789 (feature_tree), Body1790 (feature_tree), Body1791 (feature_tree), Body1792 (feature_tree), Body1793 (feature_tree), Body1794 (feature_tree), Body1795 (feature_tree), Body1796 (feature_tree), Body1797 (feature_tree), Body1798 (feature_tree), Body1799 (feature_tree), Body1800 (feature_tree), Body1801 (feature_tree), Body1802 (feature_tree), Body1803 (feature_tree), Body1804 (feature_tree), Body1805 (feature_tree), Body1806 (feature_tree), Body1807 (feature_tree), Body1808 (feature_tree), Body1809 (feature_tree), Body1810 (feature_tree), Body1811 (feature_tree), Body1812 (feature_tree), Body1813 (feature_tree), Body1814 (feature_tree), Body1815 (feature_tree)
feature tree (6076):
  other  "Твердое тело1"
  other  "Исправленная геометрия1"
  sketch  "3D эскиз1"
  sketch  "3D эскиз2"
  sketch  "3D эскиз3"
  sketch  "3D эскиз4"
  sketch  "3D эскиз5"
  sketch  "3D эскиз6"
  sketch  "3D эскиз7"
  sketch  "3D эскиз8"
  sketch  "3D эскиз9"
  sketch  "3D эскиз10"
  sketch  "3D эскиз11"
  sketch  "3D эскиз12"
  sketch  "3D эскиз13"
  sketch  "3D эскиз14"
  sketch  "3D эскиз15"
  sketch  "3D эскиз16"
  sketch  "3D эскиз17"
  sketch  "3D эскиз18"
  sketch  "3D эскиз19"
  sketch  "3D эскиз20"
  sketch  "3D эскиз21"
  sketch  "3D эскиз22"
  sketch  "3D эскиз23"
  sketch  "3D эскиз24"
  sketch  "3D эскиз25"
  sketch  "3D эскиз26"
  sketch  "3D эскиз27"
  sketch  "3D эскиз28"
  sketch  "3D эскиз29"
  sketch  "3D эскиз30"
  sketch  "3D эскиз31"
  sketch  "3D эскиз32"
  sketch  "3D эскиз33"
  sketch  "3D эскиз34"
  sketch  "3D эскиз35"
  sketch  "3D эскиз36"
  sketch  "3D эскиз37"
  sketch  "3D эскиз38"
  sketch  "3D эскиз39"
  sketch  "3D эскиз40"
  sketch  "3D эскиз41"
  sketch  "3D эскиз42"
  sketch  "3D эскиз43"
  sketch  "3D эскиз44"
  sketch  "3D эскиз45"
  sketch  "3D эскиз46"
  sketch  "3D эскиз47"
  sketch  "3D эскиз48"
  sketch  "3D эскиз49"
  sketch  "3D эскиз50"
  sketch  "3D эскиз51"
  sketch  "3D эскиз52"
  sketch  "3D эскиз53"
  sketch  "3D эскиз54"
  sketch  "3D эскиз55"
  sketch  "3D эскиз56"
  sketch  "3D эскиз57"
  sketch  "3D эскиз58"
  sketch  "3D эскиз59"
  sketch  "3D эскиз60"
  sketch  "3D эскиз61"
  sketch  "3D эскиз62"
  sketch  "3D эскиз63"
  sketch  "3D эскиз64"
  sketch  "3D эскиз65"
  sketch  "3D эскиз66"
  sketch  "3D эскиз67"
  sketch  "3D эскиз68"
  sketch  "3D эскиз69"
  sketch  "3D эскиз70"
  sketch  "3D эскиз71"
  sketch  "3D эскиз72"
  sketch  "3D эскиз73"
  sketch  "3D эскиз74"
  sketch  "3D эскиз75"
  sketch  "3D эскиз76"
  sketch  "3D эскиз77"
  sketch  "3D эскиз78"
  sketch  "3D эскиз79"
  sketch  "3D эскиз80"
  sketch  "3D эскиз81"
  sketch  "3D эскиз82"
  sketch  "3D эскиз83"
  sketch  "3D эскиз84"
  sketch  "3D эскиз85"
  sketch  "3D эскиз86"
  sketch  "3D эскиз87"
  sketch  "3D эскиз88"
  sketch  "3D эскиз89"
  sketch  "3D эскиз90"
  sketch  "3D эскиз91"
  sketch  "3D эскиз92"
  sketch  "3D эскиз93"
  sketch  "3D эскиз94"
  sketch  "3D эскиз95"
  sketch  "3D эскиз96"
  sketch  "3D эскиз97"
  sketch  "3D эскиз98"
  sketch  "3D эскиз99"
  sketch  "3D эскиз100"
  sketch  "3D эскиз101"
  sketch  "3D эскиз102"
  sketch  "3D эскиз103"
  sketch  "3D эскиз104"
  sketch  "3D эскиз105"
  sketch  "3D эскиз106"
  sketch  "3D эскиз107"
  sketch  "3D эскиз108"
  sketch  "3D эскиз109"
  sketch  "3D эскиз110"
  sketch  "3D эскиз111"
  sketch  "3D эскиз112"
  sketch  "3D эскиз113"
  sketch  "3D эскиз114"
  sketch  "3D эскиз115"
  sketch  "3D эскиз116"
  sketch  "3D эскиз117"
  sketch  "3D эскиз118"
  sketch  "3D эскиз119"
  sketch  "3D эскиз120"
  sketch  "3D эскиз121"
  sketch  "3D эскиз122"
  sketch  "3D эскиз123"
  sketch  "3D эскиз124"
  sketch  "3D эскиз125"
  sketch  "3D эскиз126"
  sketch  "3D эскиз127"
  sketch  "3D эскиз128"
  sketch  "3D эскиз129"
  sketch  "3D эскиз130"
  sketch  "3D эскиз131"
  sketch  "3D эскиз132"
  sketch  "3D эскиз133"
  sketch  "3D эскиз134"
  sketch  "3D эскиз135"
  sketch  "3D эскиз136"
  sketch  "3D эскиз137"
  sketch  "3D эскиз138"
  sketch  "3D эскиз139"
  sketch  "3D эскиз140"
  sketch  "3D эскиз141"
  sketch  "3D эскиз142"
  sketch  "3D эскиз143"
  sketch  "3D эскиз144"
  sketch  "3D эскиз145"
  sketch  "3D эскиз146"
  sketch  "3D эскиз147"
  sketch  "3D эскиз148"
  sketch  "3D эскиз149"
  sketch  "3D эскиз150"
  sketch  "3D эскиз151"
  sketch  "3D эскиз152"
  sketch  "3D эскиз153"
  sketch  "3D эскиз154"
  sketch  "3D эскиз155"
  sketch  "3D эскиз156"
  sketch  "3D эскиз157"
  sketch  "3D эскиз158"
  sketch  "3D эскиз159"
  sketch  "3D эскиз160"
  sketch  "3D эскиз161"
  sketch  "3D эскиз162"
  sketch  "3D эскиз163"
  sketch  "3D эскиз164"
  sketch  "3D эскиз165"
  sketch  "3D эскиз166"
  sketch  "3D эскиз167"
  sketch  "3D эскиз168"
  sketch  "3D эскиз169"
  sketch  "3D эскиз170"
  sketch  "3D эскиз171"
  sketch  "3D эскиз172"
  sketch  "3D эскиз173"
  sketch  "3D эскиз174"
  sketch  "3D эскиз175"
  sketch  "3D эскиз176"
  sketch  "3D эскиз177"
  sketch  "3D эскиз178"
  sketch  "3D эскиз179"
  sketch  "3D эскиз180"
  sketch  "3D эскиз181"
  sketch  "3D эскиз182"
  sketch  "3D эскиз183"
  sketch  "3D эскиз184"
  sketch  "3D эскиз185"
  sketch  "3D эскиз186"
  sketch  "3D эскиз187"
  sketch  "3D эскиз188"
  sketch  "3D эскиз189"
  sketch  "3D эскиз190"
  sketch  "3D эскиз191"
  sketch  "3D эскиз192"
  sketch  "3D эскиз193"
  sketch  "3D эскиз194"
  sketch  "3D эскиз195"
  sketch  "3D эскиз196"
  sketch  "3D эскиз197"
  sketch  "3D эскиз198"
  sketch  "3D эскиз199"
  sketch  "3D эскиз200"
  sketch  "3D эскиз201"
  sketch  "3D эскиз202"
  sketch  "3D эскиз203"
  sketch  "3D эскиз204"
  sketch  "3D эскиз205"
  sketch  "3D эскиз206"
  sketch  "3D эскиз207"
  sketch  "3D эскиз208"
  sketch  "3D эскиз209"
  sketch  "3D эскиз210"
  sketch  "3D эскиз211"
  sketch  "3D эскиз212"
  sketch  "3D эскиз213"
  sketch  "3D эскиз214"
  sketch  "3D эскиз215"
  sketch  "3D эскиз216"
  sketch  "3D эскиз217"
  sketch  "3D эскиз218"
  sketch  "3D эскиз219"
  sketch  "3D эскиз220"
  sketch  "3D эскиз221"
  sketch  "3D эскиз222"
  sketch  "3D эскиз223"
  sketch  "3D эскиз224"
  sketch  "3D эскиз225"
  sketch  "3D эскиз226"
  sketch  "3D эскиз227"
  sketch  "3D эскиз228"
  sketch  "3D эскиз229"
  sketch  "3D эскиз230"
  sketch  "3D эскиз231"
  sketch  "3D эскиз232"
  sketch  "3D эскиз233"
  sketch  "3D эскиз234"
  sketch  "3D эскиз235"
  sketch  "3D эскиз236"
  sketch  "3D эскиз237"
  sketch  "3D эскиз238"
  sketch  "3D эскиз239"
  sketch  "3D эскиз240"
  sketch  "3D эскиз241"
  sketch  "3D эскиз242"
  sketch  "3D эскиз243"
  sketch  "3D эскиз244"
  sketch  "3D эскиз245"
  sketch  "3D эскиз246"
  sketch  "3D эскиз247"
  sketch  "3D эскиз248"
  sketch  "3D эскиз249"
  sketch  "3D эскиз250"
  sketch  "3D эскиз251"
  sketch  "3D эскиз252"
  sketch  "3D эскиз253"
  sketch  "3D эскиз254"
  sketch  "3D эскиз255"
  sketch  "3D эскиз256"
  sketch  "3D эскиз257"
  sketch  "3D эскиз258"
  sketch  "3D эскиз259"
  sketch  "3D эскиз260"
  sketch  "3D эскиз261"
  sketch  "3D эскиз262"
  sketch  "3D эскиз263"
  sketch  "3D эскиз264"
  sketch  "3D эскиз265"
  sketch  "3D эскиз266"
  sketch  "3D эскиз267"
  sketch  "3D эскиз268"
  sketch  "3D эскиз269"
  sketch  "3D эскиз270"
  sketch  "3D эскиз271"
  sketch  "3D эскиз272"
  sketch  "3D эскиз273"
  sketch  "3D эскиз274"
  sketch  "3D эскиз275"
  sketch  "3D эскиз276"
  sketch  "3D эскиз277"
  sketch  "3D эскиз278"
  sketch  "3D эскиз279"
  sketch  "3D эскиз280"
  sketch  "3D эскиз281"
  sketch  "3D эскиз282"
  sketch  "3D эскиз283"
  sketch  "3D эскиз284"
  sketch  "3D эскиз285"
  sketch  "3D эскиз286"
  sketch  "3D эскиз287"
  sketch  "3D эскиз288"
  sketch  "3D эскиз289"
  sketch  "3D эскиз290"
  sketch  "3D эскиз291"
  sketch  "3D эскиз292"
  sketch  "3D эскиз293"
  sketch  "3D эскиз294"
  sketch  "3D эскиз295"
  sketch  "3D эскиз296"
  sketch  "3D эскиз297"
  sketch  "3D эскиз298"
  sketch  "3D эскиз299"
  sketch  "3D эскиз300"
  sketch  "3D эскиз301"
  sketch  "3D эскиз302"
  sketch  "3D эскиз303"
  sketch  "3D эскиз304"
  sketch  "3D эскиз305"
  sketch  "3D эскиз306"
  sketch  "3D эскиз307"
  sketch  "3D эскиз308"
  sketch  "3D эскиз309"
  sketch  "3D эскиз310"
  sketch  "3D эскиз311"
  sketch  "3D эскиз312"
  sketch  "3D эскиз313"
  sketch  "3D эскиз314"
  sketch  "3D эскиз315"
  sketch  "3D эскиз316"
  sketch  "3D эскиз317"
  sketch  "3D эскиз318"
  sketch  "3D эскиз319"
  sketch  "3D эскиз320"
  sketch  "3D эскиз321"
  sketch  "3D эскиз322"
  sketch  "3D эскиз323"
  sketch  "3D эскиз324"
  sketch  "3D эскиз325"
  sketch  "3D эскиз326"
  sketch  "3D эскиз327"
  sketch  "3D эскиз328"
  sketch  "3D эскиз329"
  sketch  "3D эскиз330"
  sketch  "3D эскиз331"
  sketch  "3D эскиз332"
  sketch  "3D эскиз333"
  sketch  "3D эскиз334"
  sketch  "3D эскиз335"
  sketch  "3D эскиз336"
  sketch  "3D эскиз337"
  sketch  "3D эскиз338"
  sketch  "3D эскиз339"
  sketch  "3D эскиз340"
  sketch  "3D эскиз341"
  sketch  "3D эскиз342"
  sketch  "3D эскиз343"
  sketch  "3D эскиз344"
  sketch  "3D эскиз345"
  sketch  "3D эскиз346"
  sketch  "3D эскиз347"
  sketch  "3D эскиз348"
  sketch  "3D эскиз349"
  sketch  "3D эскиз350"
  sketch  "3D эскиз351"
  sketch  "3D эскиз352"
  sketch  "3D эскиз353"
  sketch  "3D эскиз354"
  sketch  "3D эскиз355"
  sketch  "3D эскиз356"
  sketch  "3D эскиз357"
  sketch  "3D эскиз358"
  sketch  "3D эскиз359"
  sketch  "3D эскиз360"
  sketch  "3D эскиз361"
  sketch  "3D эскиз362"
  sketch  "3D эскиз363"
  sketch  "3D эскиз364"
  sketch  "3D эскиз365"
  sketch  "3D эскиз366"
  sketch  "3D эскиз367"
  sketch  "3D эскиз368"
  sketch  "3D эскиз369"
  sketch  "3D эскиз370"
  sketch  "3D эскиз371"
  sketch  "3D эскиз372"
  sketch  "3D эскиз373"
  sketch  "3D эскиз374"
  sketch  "3D эскиз375"
  sketch  "3D эскиз376"
  sketch  "3D эскиз377"
  sketch  "3D эскиз378"
  sketch  "3D эскиз379"
  sketch  "3D эскиз380"
  sketch  "3D эскиз381"
  sketch  "3D эскиз382"
  sketch  "3D эскиз383"
  sketch  "3D эскиз384"
  sketch  "3D эскиз385"
  sketch  "3D эскиз386"
  sketch  "3D эскиз387"
  sketch  "3D эскиз388"
  sketch  "3D эскиз389"
  sketch  "3D эскиз390"
  sketch  "3D эскиз391"
  sketch  "3D эскиз392"
  sketch  "3D эскиз393"
  sketch  "3D эскиз394"
  sketch  "3D эскиз395"
  sketch  "3D эскиз396"
  sketch  "3D эскиз397"
  sketch  "3D эскиз398"
  sketch  "3D эскиз399"
  sketch  "3D эскиз400"
  sketch  "3D эскиз401"
  sketch  "3D эскиз402"
  sketch  "3D эскиз403"
  sketch  "3D эскиз404"
  sketch  "3D эскиз405"
  sketch  "3D эскиз406"
  sketch  "3D эскиз407"
  sketch  "3D эскиз408"
  sketch  "3D эскиз409"
  sketch  "3D эскиз410"
  sketch  "3D эскиз411"
  sketch  "3D эскиз412"
  sketch  "3D эскиз413"
  sketch  "3D эскиз414"
  sketch  "3D эскиз415"
  sketch  "3D эскиз416"
  sketch  "3D эскиз417"
  sketch  "3D эскиз418"
  sketch  "3D эскиз419"
  sketch  "3D эскиз420"
  sketch  "3D эскиз421"
  sketch  "3D эскиз422"
  sketch  "3D эскиз423"
  sketch  "3D эскиз424"
  sketch  "3D эскиз425"
  sketch  "3D эскиз426"
  sketch  "3D эскиз427"
  sketch  "3D эскиз428"
  sketch  "3D эскиз429"
  sketch  "3D эскиз430"
  sketch  "3D эскиз431"
  sketch  "3D эскиз432"
  sketch  "3D эскиз433"
  sketch  "3D эскиз434"
  sketch  "3D эскиз435"
  sketch  "3D эскиз436"
  sketch  "3D эскиз437"
  sketch  "3D эскиз438"
  sketch  "3D эскиз439"
  sketch  "3D эскиз440"
  sketch  "3D эскиз441"
  sketch  "3D эскиз442"
  sketch  "3D эскиз443"
  sketch  "3D эскиз444"
  sketch  "3D эскиз445"
  sketch  "3D эскиз446"
  sketch  "3D эскиз447"
  sketch  "3D эскиз448"
  sketch  "3D эскиз449"
  sketch  "3D эскиз450"
  sketch  "3D эскиз451"
  sketch  "3D эскиз452"
  sketch  "3D эскиз453"
  sketch  "3D эскиз454"
  sketch  "3D эскиз455"
  sketch  "3D эскиз456"
  sketch  "3D эскиз457"
  sketch  "3D эскиз458"
  sketch  "3D эскиз459"
  sketch  "3D эскиз460"
  sketch  "3D эскиз461"
  sketch  "3D эскиз462"
  sketch  "3D эскиз463"
  sketch  "3D эскиз464"
  sketch  "3D эскиз465"
  sketch  "3D эскиз466"
  sketch  "3D эскиз467"
  sketch  "3D эскиз468"
  sketch  "3D эскиз469"
  sketch  "3D эскиз470"
  sketch  "3D эскиз471"
  sketch  "3D эскиз472"
  sketch  "3D эскиз473"
  sketch  "3D эскиз474"
  sketch  "3D эскиз475"
  sketch  "3D эскиз476"
  sketch  "3D эскиз477"
  sketch  "3D эскиз478"
  sketch  "3D эскиз479"
  sketch  "3D эскиз480"
  sketch  "3D эскиз481"
  sketch  "3D эскиз482"
  sketch  "3D эскиз483"
  sketch  "3D эскиз484"
  sketch  "3D эскиз485"
  sketch  "3D эскиз486"
  sketch  "3D эскиз487"
  sketch  "3D эскиз488"
  sketch  "3D эскиз489"
  sketch  "3D эскиз490"
  sketch  "3D эскиз491"
  sketch  "3D эскиз492"
  sketch  "3D эскиз493"
  sketch  "3D эскиз494"
  sketch  "3D эскиз495"
  sketch  "3D эскиз496"
  sketch  "3D эскиз497"
  sketch  "3D эскиз498"
  sketch  "3D эскиз499"
  sketch  "3D эскиз500"
  sketch  "3D эскиз501"
  sketch  "3D эскиз502"
  sketch  "3D эскиз503"
  sketch  "3D эскиз504"
  sketch  "3D эскиз505"
  sketch  "3D эскиз506"
  sketch  "3D эскиз507"
  sketch  "3D эскиз508"
  sketch  "3D эскиз509"
  sketch  "3D эскиз510"
  sketch  "3D эскиз511"
  sketch  "3D эскиз512"
  sketch  "3D эскиз513"
  sketch  "3D эскиз514"
  sketch  "3D эскиз515"
  sketch  "3D эскиз516"
  sketch  "3D эскиз517"
  sketch  "3D эскиз518"
  sketch  "3D эскиз519"
  sketch  "3D эскиз520"
  sketch  "3D эскиз521"
  sketch  "3D эскиз522"
  sketch  "3D эскиз523"
  sketch  "3D эскиз524"
  sketch  "3D эскиз525"
  sketch  "3D эскиз526"
  sketch  "3D эскиз527"
  sketch  "3D эскиз528"
  sketch  "3D эскиз529"
  sketch  "3D эскиз530"
  sketch  "3D эскиз531"
  sketch  "3D эскиз532"
  sketch  "3D эскиз533"
  sketch  "3D эскиз534"
  sketch  "3D эскиз535"
  sketch  "3D эскиз536"
  sketch  "3D эскиз537"
  sketch  "3D эскиз538"
  sketch  "3D эскиз539"
  sketch  "3D эскиз540"
  sketch  "3D эскиз541"
  sketch  "3D эскиз542"
  sketch  "3D эскиз543"
  sketch  "3D эскиз544"
  sketch  "3D эскиз545"
  sketch  "3D эскиз546"
  sketch  "3D эскиз547"
  sketch  "3D эскиз548"
  sketch  "3D эскиз549"
  sketch  "3D эскиз550"
  sketch  "3D эскиз551"
  sketch  "3D эскиз552"
  sketch  "3D эскиз553"
  sketch  "3D эскиз554"
  sketch  "3D эскиз555"
  sketch  "3D эскиз556"
  sketch  "3D эскиз557"
  sketch  "3D эскиз558"
  sketch  "3D эскиз559"
  sketch  "3D эскиз560"
  sketch  "3D эскиз561"
  sketch  "3D эскиз562"
  sketch  "3D эскиз563"
  sketch  "3D эскиз564"
  sketch  "3D эскиз565"
  sketch  "3D эскиз566"
  sketch  "3D эскиз567"
  sketch  "3D эскиз568"
  sketch  "3D эскиз569"
  sketch  "3D эскиз570"
  sketch  "3D эскиз571"
  sketch  "3D эскиз572"
  sketch  "3D эскиз573"
  sketch  "3D эскиз574"
  sketch  "3D эскиз575"
  sketch  "3D эскиз576"
  sketch  "3D эскиз577"
  sketch  "3D эскиз578"
  sketch  "3D эскиз579"
  sketch  "3D эскиз580"
  sketch  "3D эскиз581"
  sketch  "3D эскиз582"
  sketch  "3D эскиз583"
  sketch  "3D эскиз584"
  sketch  "3D эскиз585"
  sketch  "3D эскиз586"
  sketch  "3D эскиз587"
  sketch  "3D эскиз588"
  sketch  "3D эскиз589"
  sketch  "3D эскиз590"
  sketch  "3D эскиз591"
  sketch  "3D эскиз592"
  sketch  "3D эскиз593"
  sketch  "3D эскиз594"
  sketch  "3D эскиз595"
  sketch  "3D эскиз596"
  sketch  "3D эскиз597"
  sketch  "3D эскиз598"
  sketch  "3D эскиз599"
  sketch  "3D эскиз600"
  sketch  "3D эскиз601"
  sketch  "3D эскиз602"
  sketch  "3D эскиз603"
  sketch  "3D эскиз604"
  sketch  "3D эскиз605"
  sketch  "3D эскиз606"
  sketch  "3D эскиз607"
  sketch  "3D эскиз608"
  sketch  "3D эскиз609"
  sketch  "3D эскиз610"
  sketch  "3D эскиз611"
  sketch  "3D эскиз612"
  sketch  "3D эскиз613"
  sketch  "3D эскиз614"
  sketch  "3D эскиз615"
  sketch  "3D эскиз616"
  sketch  "3D эскиз617"
  sketch  "3D эскиз618"
  sketch  "3D эскиз619"
  sketch  "3D эскиз620"
  sketch  "3D эскиз621"
  sketch  "3D эскиз622"
  sketch  "3D эскиз623"
  sketch  "3D эскиз624"
  sketch  "3D эскиз625"
  sketch  "3D эскиз626"
  sketch  "3D эскиз627"
  sketch  "3D эскиз628"
  sketch  "3D эскиз629"
  sketch  "3D эскиз630"
  sketch  "3D эскиз631"
  sketch  "3D эскиз632"
  sketch  "3D эскиз633"
  sketch  "3D эскиз634"
  sketch  "3D эскиз635"
  sketch  "3D эскиз636"
  sketch  "3D эскиз637"
  sketch  "3D эскиз638"
  sketch  "3D эскиз639"
  sketch  "3D эскиз640"
  sketch  "3D эскиз641"
  sketch  "3D эскиз642"
  sketch  "3D эскиз643"
  sketch  "3D эскиз644"
  sketch  "3D эскиз645"
  sketch  "3D эскиз646"
  sketch  "3D эскиз647"
  sketch  "3D эскиз648"
  sketch  "3D эскиз649"
  sketch  "3D эскиз650"
  sketch  "3D эскиз651"
  sketch  "3D эскиз652"
  sketch  "3D эскиз653"
  sketch  "3D эскиз654"
  sketch  "3D эскиз655"
  sketch  "3D эскиз656"
  sketch  "3D эскиз657"
  sketch  "3D эскиз658"
  sketch  "3D эскиз659"
  sketch  "3D эскиз660"
  sketch  "3D эскиз661"
  sketch  "3D эскиз662"
  sketch  "3D эскиз663"
  sketch  "3D эскиз664"
  sketch  "3D эскиз665"
  sketch  "3D эскиз666"
  sketch  "3D эскиз667"
  sketch  "3D эскиз668"
  sketch  "3D эскиз669"
  sketch  "3D эскиз670"
  sketch  "3D эскиз671"
  sketch  "3D эскиз672"
  sketch  "3D эскиз673"
  sketch  "3D эскиз674"
  sketch  "3D эскиз675"
  sketch  "3D эскиз676"
  sketch  "3D эскиз677"
  sketch  "3D эскиз678"
  sketch  "3D эскиз679"
  sketch  "3D эскиз680"
  sketch  "3D эскиз681"
  sketch  "3D эскиз682"
  sketch  "3D эскиз683"
  sketch  "3D эскиз684"
  sketch  "3D эскиз685"
  sketch  "3D эскиз686"
  sketch  "3D эскиз687"
  sketch  "3D эскиз688"
  sketch  "3D эскиз689"
  sketch  "3D эскиз690"
  sketch  "3D эскиз691"
  sketch  "3D эскиз692"
  sketch  "3D эскиз693"
  sketch  "3D эскиз694"
  sketch  "3D эскиз695"
  sketch  "3D эскиз696"
  sketch  "3D эскиз697"
  sketch  "3D эскиз698"
  sketch  "3D эскиз699"
  sketch  "3D эскиз700"
  sketch  "3D эскиз701"
  sketch  "3D эскиз702"
  sketch  "3D эскиз703"
  sketch  "3D эскиз704"
  sketch  "3D эскиз705"
  sketch  "3D эскиз706"
  sketch  "3D эскиз707"
  sketch  "3D эскиз708"
  sketch  "3D эскиз709"
  sketch  "3D эскиз710"
  sketch  "3D эскиз711"
  sketch  "3D эскиз712"
  sketch  "3D эскиз713"
  sketch  "3D эскиз714"
  sketch  "3D эскиз715"
  sketch  "3D эскиз716"
  sketch  "3D эскиз717"
  sketch  "3D эскиз718"
  sketch  "3D эскиз719"
  sketch  "3D эскиз720"
  sketch  "3D эскиз721"
  sketch  "3D эскиз722"
  sketch  "3D эскиз723"
  sketch  "3D эскиз724"
  sketch  "3D эскиз725"
  sketch  "3D эскиз726"
  sketch  "3D эскиз727"
  sketch  "3D эскиз728"
  sketch  "3D эскиз729"
  sketch  "3D эскиз730"
  sketch  "3D эскиз731"
  sketch  "3D эскиз732"
  sketch  "3D эскиз733"
  sketch  "3D эскиз734"
  sketch  "3D эскиз735"
  sketch  "3D эскиз736"
  sketch  "3D эскиз737"
  sketch  "3D эскиз738"
  sketch  "3D эскиз739"
  sketch  "3D эскиз740"
  sketch  "3D эскиз741"
  sketch  "3D эскиз742"
  sketch  "3D эскиз743"
  sketch  "3D эскиз744"
  sketch  "3D эскиз745"
  sketch  "3D эскиз746"
  sketch  "3D эскиз747"
  sketch  "3D эскиз748"
  sketch  "3D эскиз749"
  sketch  "3D эскиз750"
  sketch  "3D эскиз751"
  sketch  "3D эскиз752"
  sketch  "3D эскиз753"
  sketch  "3D эскиз754"
  sketch  "3D эскиз755"
  sketch  "3D эскиз756"
  sketch  "3D эскиз757"
  sketch  "3D эскиз758"
  sketch  "3D эскиз759"
  sketch  "3D эскиз760"
  sketch  "3D эскиз761"
  sketch  "3D эскиз762"
  sketch  "3D эскиз763"
  sketch  "3D эскиз764"
  sketch  "3D эскиз765"
  sketch  "3D эскиз766"
  sketch  "3D эскиз767"
  sketch  "3D эскиз768"
  sketch  "3D эскиз769"
  sketch  "3D эскиз770"
  sketch  "3D эскиз771"
  sketch  "3D эскиз772"
  sketch  "3D эскиз773"
  sketch  "3D эскиз774"
  sketch  "3D эскиз775"
  sketch  "3D эскиз776"
  sketch  "3D эскиз777"
  sketch  "3D эскиз778"
  sketch  "3D эскиз779"
  sketch  "3D эскиз780"
  sketch  "3D эскиз781"
  sketch  "3D эскиз782"
  sketch  "3D эскиз783"
  sketch  "3D эскиз784"
  sketch  "3D эскиз785"
  sketch  "3D эскиз786"
  sketch  "3D эскиз787"
  sketch  "3D эскиз788"
  sketch  "3D эскиз789"
  sketch  "3D эскиз790"
  sketch  "3D эскиз791"
  sketch  "3D эскиз792"
  sketch  "3D эскиз793"
  sketch  "3D эскиз794"
  sketch  "3D эскиз795"
  sketch  "3D эскиз796"
  sketch  "3D эскиз797"
  sketch  "3D эскиз798"
  sketch  "3D эскиз799"
  sketch  "3D эскиз800"
  sketch  "3D эскиз801"
  sketch  "3D эскиз802"
  sketch  "3D эскиз803"
  sketch  "3D эскиз804"
  sketch  "3D эскиз805"
  sketch  "3D эскиз806"
  sketch  "3D эскиз807"
  sketch  "3D эскиз808"
  sketch  "3D эскиз809"
  sketch  "3D эскиз810"
  sketch  "3D эскиз811"
  sketch  "3D эскиз812"
  sketch  "3D эскиз813"
  sketch  "3D эскиз814"
  sketch  "3D эскиз815"
  sketch  "3D эскиз816"
  sketch  "3D эскиз817"
  sketch  "3D эскиз818"
  sketch  "3D эскиз819"
  sketch  "3D эскиз820"
  sketch  "3D эскиз821"
  sketch  "3D эскиз822"
  sketch  "3D эскиз823"
  sketch  "3D эскиз824"
  sketch  "3D эскиз825"
  sketch  "3D эскиз826"
  sketch  "3D эскиз827"
  sketch  "3D эскиз828"
  sketch  "3D эскиз829"
  sketch  "3D эскиз830"
  sketch  "3D эскиз831"
  sketch  "3D эскиз832"
  sketch  "3D эскиз833"
  sketch  "3D эскиз834"
  sketch  "3D эскиз835"
  sketch  "3D эскиз836"
  sketch  "3D эскиз837"
  sketch  "3D эскиз838"
  sketch  "3D эскиз839"
  sketch  "3D эскиз840"
  sketch  "3D эскиз841"
  sketch  "3D эскиз842"
  sketch  "3D эскиз843"
  sketch  "3D эскиз844"
  sketch  "3D эскиз845"
  sketch  "3D эскиз846"
  sketch  "3D эскиз847"
  sketch  "3D эскиз848"
  sketch  "3D эскиз849"
  sketch  "3D эскиз850"
  sketch  "3D эскиз851"
  sketch  "3D эскиз852"
  sketch  "3D эскиз853"
  sketch  "3D эскиз854"
  sketch  "3D эскиз855"
  sketch  "3D эскиз856"
  sketch  "3D эскиз857"
  sketch  "3D эскиз858"
  sketch  "3D эскиз859"
  sketch  "3D эскиз860"
  sketch  "3D эскиз861"
  sketch  "3D эскиз862"
  sketch  "3D эскиз863"
  sketch  "3D эскиз864"
  sketch  "3D эскиз865"
  sketch  "3D эскиз866"
  sketch  "3D эскиз867"
  sketch  "3D эскиз868"
  sketch  "3D эскиз869"
  sketch  "3D эскиз870"
  sketch  "3D эскиз871"
  sketch  "3D эскиз872"
  sketch  "3D эскиз873"
  sketch  "3D эскиз874"
  sketch  "3D эскиз875"
  sketch  "3D эскиз876"
  sketch  "3D эскиз877"
  sketch  "3D эскиз878"
  sketch  "3D эскиз879"
  sketch  "3D эскиз880"
  sketch  "3D эскиз881"
  sketch  "3D эскиз882"
  sketch  "3D эскиз883"
  sketch  "3D эскиз884"
  sketch  "3D эскиз885"
  sketch  "3D эскиз886"
  sketch  "3D эскиз887"
  sketch  "3D эскиз888"
  sketch  "3D эскиз889"
  sketch  "3D эскиз890"
  sketch  "3D эскиз891"
  sketch  "3D эскиз892"
  sketch  "3D эскиз893"
  sketch  "3D эскиз894"
  sketch  "3D эскиз895"
  sketch  "3D эскиз896"
  sketch  "3D эскиз897"
  sketch  "3D эскиз898"
  sketch  "3D эскиз899"
  sketch  "3D эскиз900"
  sketch  "3D эскиз901"
  sketch  "3D эскиз902"
  sketch  "3D эскиз903"
  sketch  "3D эскиз904"
  sketch  "3D эскиз905"
  sketch  "3D эскиз906"
  sketch  "3D эскиз907"
  sketch  "3D эскиз908"
  sketch  "3D эскиз909"
  sketch  "3D эскиз910"
  sketch  "3D эскиз911"
  sketch  "3D эскиз912"
  sketch  "3D эскиз913"
  sketch  "3D эскиз914"
  sketch  "3D эскиз915"
  sketch  "3D эскиз916"
  sketch  "3D эскиз917"
  sketch  "3D эскиз918"
  sketch  "3D эскиз919"
  sketch  "3D эскиз920"
  sketch  "3D эскиз921"
  sketch  "3D эскиз922"
  sketch  "3D эскиз923"
  sketch  "3D эскиз924"
  sketch  "3D эскиз925"
  sketch  "3D эскиз926"
  sketch  "3D эскиз927"
  sketch  "3D эскиз928"
  sketch  "3D эскиз929"
  sketch  "3D эскиз930"
  sketch  "3D эскиз931"
  sketch  "3D эскиз932"
  sketch  "3D эскиз933"
  sketch  "3D эскиз934"
  sketch  "3D эскиз935"
  sketch  "3D эскиз936"
  sketch  "3D эскиз937"
  sketch  "3D эскиз938"
  sketch  "3D эскиз939"
  sketch  "3D эскиз940"
  sketch  "3D эскиз941"
  sketch  "3D эскиз942"
  sketch  "3D эскиз943"
  sketch  "3D эскиз944"
  sketch  "3D эскиз945"
  sketch  "3D эскиз946"
  sketch  "3D эскиз947"
  sketch  "3D эскиз948"
  sketch  "3D эскиз949"
  sketch  "3D эскиз950"
  sketch  "3D эскиз951"
  sketch  "3D эскиз952"
  sketch  "3D эскиз953"
  sketch  "3D эскиз954"
  sketch  "3D эскиз955"
  sketch  "3D эскиз956"
  sketch  "3D эскиз957"
  sketch  "3D эскиз958"
  sketch  "3D эскиз959"
  sketch  "3D эскиз960"
  sketch  "3D эскиз961"
  sketch  "3D эскиз962"
  sketch  "3D эскиз963"
  sketch  "3D эскиз964"
  sketch  "3D эскиз965"
  sketch  "3D эскиз966"
  sketch  "3D эскиз967"
  sketch  "3D эскиз968"
  sketch  "3D эскиз969"
  sketch  "3D эскиз970"
  sketch  "3D эскиз971"
  sketch  "3D эскиз972"
  sketch  "3D эскиз973"
  sketch  "3D эскиз974"
  sketch  "3D эскиз975"
  sketch  "3D эскиз976"
  sketch  "3D эскиз977"
  sketch  "3D эскиз978"
  sketch  "3D эскиз979"
  sketch  "3D эскиз980"
  sketch  "3D эскиз981"
  sketch  "3D эскиз982"
  sketch  "3D эскиз983"
  sketch  "3D эскиз984"
  sketch  "3D эскиз985"
  sketch  "3D эскиз986"
  sketch  "3D эскиз987"
  sketch  "3D эскиз988"
  sketch  "3D эскиз989"
  sketch  "3D эскиз990"
  sketch  "3D эскиз991"
  sketch  "3D эскиз992"
  sketch  "3D эскиз993"
  sketch  "3D эскиз994"
  sketch  "3D эскиз995"
  sketch  "3D эскиз996"
  sketch  "3D эскиз997"
  sketch  "3D эскиз998"
  sketch  "3D эскиз999"
  sketch  "3D эскиз1000"
  sketch  "3D эскиз1001"
  sketch  "3D эскиз1002"
  sketch  "3D эскиз1003"
  sketch  "3D эскиз1004"
  sketch  "3D эскиз1005"
  sketch  "3D эскиз1006"
  sketch  "3D эскиз1007"
  sketch  "3D эскиз1008"
  sketch  "3D эскиз1009"
  sketch  "3D эскиз1010"
  sketch  "3D эскиз1011"
  sketch  "3D эскиз1012"
  sketch  "3D эскиз1013"
  sketch  "3D эскиз1014"
  sketch  "3D эскиз1015"
  sketch  "3D эскиз1016"
  sketch  "3D эскиз1017"
  sketch  "3D эскиз1018"
  sketch  "3D эскиз1019"
  sketch  "3D эскиз1020"
  sketch  "3D эскиз1021"
  sketch  "3D эскиз1022"
  sketch  "3D эскиз1023"
  sketch  "3D эскиз1024"
  sketch  "3D эскиз1025"
  sketch  "3D эскиз1026"
  sketch  "3D эскиз1027"
  sketch  "3D эскиз1028"
  sketch  "3D эскиз1029"
  sketch  "3D эскиз1030"
  sketch  "3D эскиз1031"
  sketch  "3D эскиз1032"
  sketch  "3D эскиз1033"
  sketch  "3D эскиз1034"
  sketch  "3D эскиз1035"
  sketch  "3D эскиз1036"
  sketch  "3D эскиз1037"
  sketch  "3D эскиз1038"
  sketch  "3D эскиз1039"
  sketch  "3D эскиз1040"
  sketch  "3D эскиз1041"
  sketch  "3D эскиз1042"
  sketch  "3D эскиз1043"
  sketch  "3D эскиз1044"
  sketch  "3D эскиз1045"
  sketch  "3D эскиз1046"
  sketch  "3D эскиз1047"
  sketch  "3D эскиз1048"
  sketch  "3D эскиз1049"
  sketch  "3D эскиз1050"
  sketch  "3D эскиз1051"
  sketch  "3D эскиз1052"
  sketch  "3D эскиз1053"
  sketch  "3D эскиз1054"
  sketch  "3D эскиз1055"
  sketch  "3D эскиз1056"
  sketch  "3D эскиз1057"
  sketch  "3D эскиз1058"
  sketch  "3D эскиз1059"
  sketch  "3D эскиз1060"
  sketch  "3D эскиз1061"
  sketch  "3D эскиз1062"
  sketch  "3D эскиз1063"
  sketch  "3D эскиз1064"
  sketch  "3D эскиз1065"
  sketch  "3D эскиз1066"
  sketch  "3D эскиз1067"
  sketch  "3D эскиз1068"
  sketch  "3D эскиз1069"
  sketch  "3D эскиз1070"
  sketch  "3D эскиз1071"
  sketch  "3D эскиз1072"
  sketch  "3D эскиз1073"
  sketch  "3D эскиз1074"
  sketch  "3D эскиз1075"
  sketch  "3D эскиз1076"
  sketch  "3D эскиз1077"
  sketch  "3D эскиз1078"
  sketch  "3D эскиз1079"
  sketch  "3D эскиз1080"
  sketch  "3D эскиз1081"
  sketch  "3D эскиз1082"
  sketch  "3D эскиз1083"
  sketch  "3D эскиз1084"
  sketch  "3D эскиз1085"
  sketch  "3D эскиз1086"
  sketch  "3D эскиз1087"
  sketch  "3D эскиз1088"
  sketch  "3D эскиз1089"
  sketch  "3D эскиз1090"
  sketch  "3D эскиз1091"
  sketch  "3D эскиз1092"
  sketch  "3D эскиз1093"
  sketch  "3D эскиз1094"
  sketch  "3D эскиз1095"
  sketch  "3D эскиз1096"
  sketch  "3D эскиз1097"
  sketch  "3D эскиз1098"
  sketch  "3D эскиз1099"
  sketch  "3D эскиз1100"
  sketch  "3D эскиз1101"
  sketch  "3D эскиз1102"
  sketch  "3D эскиз1103"
  sketch  "3D эскиз1104"
  sketch  "3D эскиз1105"
  sketch  "3D эскиз1106"
  sketch  "3D эскиз1107"
  sketch  "3D эскиз1108"
  sketch  "3D эскиз1109"
  sketch  "3D эскиз1110"
  sketch  "3D эскиз1111"
  sketch  "3D эскиз1112"
  sketch  "3D эскиз1113"
  sketch  "3D эскиз1114"
  sketch  "3D эскиз1115"
  sketch  "3D эскиз1116"
  sketch  "3D эскиз1117"
  sketch  "3D эскиз1118"
  sketch  "3D эскиз1119"
  sketch  "3D эскиз1120"
  sketch  "3D эскиз1121"
  sketch  "3D эскиз1122"
  sketch  "3D эскиз1123"
  sketch  "3D эскиз1124"
  sketch  "3D эскиз1125"
  sketch  "3D эскиз1126"
  sketch  "3D эскиз1127"
  sketch  "3D эскиз1128"
  sketch  "3D эскиз1129"
  sketch  "3D эскиз1130"
  sketch  "3D эскиз1131"
  sketch  "3D эскиз1132"
  sketch  "3D эскиз1133"
  sketch  "3D эскиз1134"
  sketch  "3D эскиз1135"
  sketch  "3D эскиз1136"
  sketch  "3D эскиз1137"
  sketch  "3D эскиз1138"
  sketch  "3D эскиз1139"
  sketch  "3D эскиз1140"
  sketch  "3D эскиз1141"
  sketch  "3D эскиз1142"
  sketch  "3D эскиз1143"
  sketch  "3D эскиз1144"
  sketch  "3D эскиз1145"
  sketch  "3D эскиз1146"
  sketch  "3D эскиз1147"
  sketch  "3D эскиз1148"
  sketch  "3D эскиз1149"
  sketch  "3D эскиз1150"
  sketch  "3D эскиз1151"
  sketch  "3D эскиз1152"
  sketch  "3D эскиз1153"
  sketch  "3D эскиз1154"
  sketch  "3D эскиз1155"
  sketch  "3D эскиз1156"
  sketch  "3D эскиз1157"
  sketch  "3D эскиз1158"
  sketch  "3D эскиз1159"
  sketch  "3D эскиз1160"
  sketch  "3D эскиз1161"
  sketch  "3D эскиз1162"
  sketch  "3D эскиз1163"
  sketch  "3D эскиз1164"
  sketch  "3D эскиз1165"
  sketch  "3D эскиз1166"
  sketch  "3D эскиз1167"
  sketch  "3D эскиз1168"
  sketch  "3D эскиз1169"
  sketch  "3D эскиз1170"
  sketch  "3D эскиз1171"
  sketch  "3D эскиз1172"
  sketch  "3D эскиз1173"
  sketch  "3D эскиз1174"
  sketch  "3D эскиз1175"
  sketch  "3D эскиз1176"
  sketch  "3D эскиз1177"
  sketch  "3D эскиз1178"
  sketch  "3D эскиз1179"
  sketch  "3D эскиз1180"
  sketch  "3D эскиз1181"
  sketch  "3D эскиз1182"
  sketch  "3D эскиз1183"
  sketch  "3D эскиз1184"
  sketch  "3D эскиз1185"
  sketch  "3D эскиз1186"
  sketch  "3D эскиз1187"
  sketch  "3D эскиз1188"
  sketch  "3D эскиз1189"
  sketch  "3D эскиз1190"
  sketch  "3D эскиз1191"
  sketch  "3D эскиз1192"
  sketch  "3D эскиз1193"
  sketch  "3D эскиз1194"
  sketch  "3D эскиз1195"
  sketch  "3D эскиз1196"
  sketch  "3D эскиз1197"
  sketch  "3D эскиз1198"
  sketch  "3D эскиз1199"
  sketch  "3D эскиз1200"
  sketch  "3D эскиз1201"
  sketch  "3D эскиз1202"
  sketch  "3D эскиз1203"
  sketch  "3D эскиз1204"
  sketch  "3D эскиз1205"
  sketch  "3D эскиз1206"
  sketch  "3D эскиз1207"
  sketch  "3D эскиз1208"
  sketch  "3D эскиз1209"
  sketch  "3D эскиз1210"
  sketch  "3D эскиз1211"
  sketch  "3D эскиз1212"
  sketch  "3D эскиз1213"
  sketch  "3D эскиз1214"
  sketch  "3D эскиз1215"
  sketch  "3D эскиз1216"
  sketch  "3D эскиз1217"
  sketch  "3D эскиз1218"
  sketch  "3D эскиз1219"
  sketch  "3D эскиз1220"
  sketch  "3D эскиз1221"
  sketch  "3D эскиз1222"
  sketch  "3D эскиз1223"
  sketch  "3D эскиз1224"
  sketch  "3D эскиз1225"
  sketch  "3D эскиз1226"
  sketch  "3D эскиз1227"
  sketch  "3D эскиз1228"
  sketch  "3D эскиз1229"
  sketch  "3D эскиз1230"
  sketch  "3D эскиз1231"
  sketch  "3D эскиз1232"
  sketch  "3D эскиз1233"
  sketch  "3D эскиз1234"
  sketch  "3D эскиз1235"
  sketch  "3D эскиз1236"
  sketch  "3D эскиз1237"
  sketch  "3D эскиз1238"
  sketch  "3D эскиз1239"
  sketch  "3D эскиз1240"
  sketch  "3D эскиз1241"
  sketch  "3D эскиз1242"
  sketch  "3D эскиз1243"
  sketch  "3D эскиз1244"
  sketch  "3D эскиз1245"
  sketch  "3D эскиз1246"
  sketch  "3D эскиз1247"
  sketch  "3D эскиз1248"
  sketch  "3D эскиз1249"
  sketch  "3D эскиз1250"
  sketch  "3D эскиз1251"
  sketch  "3D эскиз1252"
  sketch  "3D эскиз1253"
  sketch  "3D эскиз1254"
  sketch  "3D эскиз1255"
  sketch  "3D эскиз1256"
  sketch  "3D эскиз1257"
  sketch  "3D эскиз1258"
  sketch  "3D эскиз1259"
  sketch  "3D эскиз1260"
  sketch  "3D эскиз1261"
  sketch  "3D эскиз1262"
  sketch  "3D эскиз1263"
  sketch  "3D эскиз1264"
  sketch  "3D эскиз1265"
  sketch  "3D эскиз1266"
  sketch  "3D эскиз1267"
  sketch  "3D эскиз1268"
  sketch  "3D эскиз1269"
  sketch  "3D эскиз1270"
  sketch  "3D эскиз1271"
  sketch  "3D эскиз1272"
  sketch  "3D эскиз1273"
  sketch  "3D эскиз1274"
  sketch  "3D эскиз1275"
  sketch  "3D эскиз1276"
  sketch  "3D эскиз1277"
  sketch  "3D эскиз1278"
  sketch  "3D эскиз1279"
  sketch  "3D эскиз1280"
  sketch  "3D эскиз1281"
  sketch  "3D эскиз1282"
  sketch  "3D эскиз1283"
  sketch  "3D эскиз1284"
  sketch  "3D эскиз1285"
  sketch  "3D эскиз1286"
  sketch  "3D эскиз1287"
  sketch  "3D эскиз1288"
  sketch  "3D эскиз1289"
  sketch  "3D эскиз1290"
  sketch  "3D эскиз1291"
  sketch  "3D эскиз1292"
  sketch  "3D эскиз1293"
  sketch  "3D эскиз1294"
  sketch  "3D эскиз1295"
  sketch  "3D эскиз1296"
  sketch  "3D эскиз1297"
  sketch  "3D эскиз1298"
  sketch  "3D эскиз1299"
  sketch  "3D эскиз1300"
  sketch  "3D эскиз1301"
  sketch  "3D эскиз1302"
  sketch  "3D эскиз1303"
  sketch  "3D эскиз1304"
  sketch  "3D эскиз1305"
  sketch  "3D эскиз1306"
  sketch  "3D эскиз1307"
  sketch  "3D эскиз1308"
  sketch  "3D эскиз1309"
  sketch  "3D эскиз1310"
  sketch  "3D эскиз1311"
  sketch  "3D эскиз1312"
  sketch  "3D эскиз1313"
  sketch  "3D эскиз1314"
  sketch  "3D эскиз1315"
  sketch  "3D эскиз1316"
  sketch  "3D эскиз1317"
  sketch  "3D эскиз1318"
  sketch  "3D эскиз1319"
  sketch  "3D эскиз1320"
  sketch  "3D эскиз1321"
  sketch  "3D эскиз1322"
  sketch  "3D эскиз1323"
  sketch  "3D эскиз1324"
  sketch  "3D эскиз1325"
  sketch  "3D эскиз1326"
  sketch  "3D эскиз1327"
  sketch  "3D эскиз1328"
  sketch  "3D эскиз1329"
  sketch  "3D эскиз1330"
  sketch  "3D эскиз1331"
  sketch  "3D эскиз1332"
  sketch  "3D эскиз1333"
  sketch  "3D эскиз1334"
  sketch  "3D эскиз1335"
  sketch  "3D эскиз1336"
  sketch  "3D эскиз1337"
  sketch  "3D эскиз1338"
  sketch  "3D эскиз1339"
  sketch  "3D эскиз1340"
  sketch  "3D эскиз1341"
  sketch  "3D эскиз1342"
  sketch  "3D эскиз1343"
  sketch  "3D эскиз1344"
  sketch  "3D эскиз1345"
  sketch  "3D эскиз1346"
  sketch  "3D эскиз1347"
  sketch  "3D эскиз1348"
  sketch  "3D эскиз1349"
  sketch  "3D эскиз1350"
  sketch  "3D эскиз1351"
  sketch  "3D эскиз1352"
  sketch  "3D эскиз1353"
  sketch  "3D эскиз1354"
  sketch  "3D эскиз1355"
  sketch  "3D эскиз1356"
  sketch  "3D эскиз1357"
  sketch  "3D эскиз1358"
  sketch  "3D эскиз1359"
  sketch  "3D эскиз1360"
  sketch  "3D эскиз1361"
  sketch  "3D эскиз1362"
  sketch  "3D эскиз1363"
  sketch  "3D эскиз1364"
  sketch  "3D эскиз1365"
  sketch  "3D эскиз1366"
  sketch  "3D эскиз1367"
  sketch  "3D эскиз1368"
  sketch  "3D эскиз1369"
  sketch  "3D эскиз1370"
  sketch  "3D эскиз1371"
  sketch  "3D эскиз1372"
  sketch  "3D эскиз1373"
  sketch  "3D эскиз1374"
  sketch  "3D эскиз1375"
  sketch  "3D эскиз1376"
  sketch  "3D эскиз1377"
  sketch  "3D эскиз1378"
  sketch  "3D эскиз1379"
  sketch  "3D эскиз1380"
  sketch  "3D эскиз1381"
  sketch  "3D эскиз1382"
  sketch  "3D эскиз1383"
  sketch  "3D эскиз1384"
  sketch  "3D эскиз1385"
  sketch  "3D эскиз1386"
  sketch  "3D эскиз1387"
  sketch  "3D эскиз1388"
  sketch  "3D эскиз1389"
  sketch  "3D эскиз1390"
  sketch  "3D эскиз1391"
  sketch  "3D эскиз1392"
  sketch  "3D эскиз1393"
  sketch  "3D эскиз1394"
  sketch  "3D эскиз1395"
  sketch  "3D эскиз1396"
  sketch  "3D эскиз1397"
  sketch  "3D эскиз1398"
  sketch  "3D эскиз1399"
  sketch  "3D эскиз1400"
  sketch  "3D эскиз1401"
  sketch  "3D эскиз1402"
  sketch  "3D эскиз1403"
  sketch  "3D эскиз1404"
  sketch  "3D эскиз1405"
  sketch  "3D эскиз1406"
  sketch  "3D эскиз1407"
  sketch  "3D эскиз1408"
  sketch  "3D эскиз1409"
  sketch  "3D эскиз1410"
  sketch  "3D эскиз1411"
  sketch  "3D эскиз1412"
  sketch  "3D эскиз1413"
  sketch  "3D эскиз1414"
  sketch  "3D эскиз1415"
  sketch  "3D эскиз1416"
  sketch  "3D эскиз1417"
  sketch  "3D эскиз1418"
  sketch  "3D эскиз1419"
  sketch  "3D эскиз1420"
  sketch  "3D эскиз1421"
  sketch  "3D эскиз1422"
  sketch  "3D эскиз1423"
  sketch  "3D эскиз1424"
  sketch  "3D эскиз1425"
  sketch  "3D эскиз1426"
  sketch  "3D эскиз1427"
  sketch  "3D эскиз1428"
  sketch  "3D эскиз1429"
  sketch  "3D эскиз1430"
  sketch  "3D эскиз1431"
  sketch  "3D эскиз1432"
  sketch  "3D эскиз1433"
  sketch  "3D эскиз1434"
  sketch  "3D эскиз1435"
  sketch  "3D эскиз1436"
  sketch  "3D эскиз1437"
  sketch  "3D эскиз1438"
  sketch  "3D эскиз1439"
  sketch  "3D эскиз1440"
  sketch  "3D эскиз1441"
  sketch  "3D эскиз1442"
  sketch  "3D эскиз1443"
  sketch  "3D эскиз1444"
  sketch  "3D эскиз1445"
  sketch  "3D эскиз1446"
  sketch  "3D эскиз1447"
  sketch  "3D эскиз1448"
  sketch  "3D эскиз1449"
  sketch  "3D эскиз1450"
  sketch  "3D эскиз1451"
  sketch  "3D эскиз1452"
  sketch  "3D эскиз1453"
  sketch  "3D эскиз1454"
  sketch  "3D эскиз1455"
  sketch  "3D эскиз1456"
  sketch  "3D эскиз1457"
  sketch  "3D эскиз1458"
  sketch  "3D эскиз1459"
  sketch  "3D эскиз1460"
  sketch  "3D эскиз1461"
  sketch  "3D эскиз1462"
  sketch  "3D эскиз1463"
  sketch  "3D эскиз1464"
  sketch  "3D эскиз1465"
  sketch  "3D эскиз1466"
  sketch  "3D эскиз1467"
  sketch  "3D эскиз1468"
  sketch  "3D эскиз1469"
  sketch  "3D эскиз1470"
  sketch  "3D эскиз1471"
  sketch  "3D эскиз1472"
  sketch  "3D эскиз1473"
  sketch  "3D эскиз1474"
  sketch  "3D эскиз1475"
  sketch  "3D эскиз1476"
  sketch  "3D эскиз1477"
  sketch  "3D эскиз1478"
  sketch  "3D эскиз1479"
  sketch  "3D эскиз1480"
  sketch  "3D эскиз1481"
  sketch  "3D эскиз1482"
  sketch  "3D эскиз1483"
  sketch  "3D эскиз1484"
  sketch  "3D эскиз1485"
  sketch  "3D эскиз1486"
  sketch  "3D эскиз1487"
  sketch  "3D эскиз1488"
  sketch  "3D эскиз1489"
  sketch  "3D эскиз1490"
  sketch  "3D эскиз1491"
  sketch  "3D эскиз1492"
  sketch  "3D эскиз1493"
  sketch  "3D эскиз1494"
  sketch  "3D эскиз1495"
  sketch  "3D эскиз1496"
  sketch  "3D эскиз1497"
  sketch  "3D эскиз1498"
  sketch  "3D эскиз1499"
  sketch  "3D эскиз1500"
  sketch  "3D эскиз1501"
  sketch  "3D эскиз1502"
  sketch  "3D эскиз1503"
  sketch  "3D эскиз1504"
  sketch  "3D эскиз1505"
  sketch  "3D эскиз1506"
  sketch  "3D эскиз1507"
  sketch  "3D эскиз1508"
  sketch  "3D эскиз1509"
  sketch  "3D эскиз1510"
  sketch  "3D эскиз1511"
  sketch  "3D эскиз1512"
  sketch  "3D эскиз1513"
  sketch  "3D эскиз1514"
  sketch  "3D эскиз1515"
  sketch  "3D эскиз1516"
  sketch  "3D эскиз1517"
  sketch  "3D эскиз1518"
  sketch  "3D эскиз1519"
  sketch  "3D эскиз1520"
  sketch  "3D эскиз1521"
  sketch  "3D эскиз1522"
  sketch  "3D эскиз1523"
  sketch  "3D эскиз1524"
  sketch  "3D эскиз1525"
  sketch  "3D эскиз1526"
  sketch  "3D эскиз1527"
  sketch  "3D эскиз1528"
  sketch  "3D эскиз1529"
  sketch  "3D эскиз1530"
  sketch  "3D эскиз1531"
  sketch  "3D эскиз1532"
  sketch  "3D эскиз1533"
  sketch  "3D эскиз1534"
  sketch  "3D эскиз1535"
  sketch  "3D эскиз1536"
  sketch  "3D эскиз1537"
  sketch  "3D эскиз1538"
  sketch  "3D эскиз1539"
  sketch  "3D эскиз1540"
  sketch  "3D эскиз1541"
  sketch  "3D эскиз1542"
  sketch  "3D эскиз1543"
  sketch  "3D эскиз1544"
  sketch  "3D эскиз1545"
  sketch  "3D эскиз1546"
  sketch  "3D эскиз1547"
  sketch  "3D эскиз1548"
  sketch  "3D эскиз1549"
  sketch  "3D эскиз1550"
  sketch  "3D эскиз1551"
  sketch  "3D эскиз1552"
  sketch  "3D эскиз1553"
  sketch  "3D эскиз1554"
  sketch  "3D эскиз1555"
  sketch  "3D эскиз1556"
  sketch  "3D эскиз1557"
  sketch  "3D эскиз1558"
  sketch  "3D эскиз1559"
  sketch  "3D эскиз1560"
  sketch  "3D эскиз1561"
  sketch  "3D эскиз1562"
  sketch  "3D эскиз1563"
  sketch  "3D эскиз1564"
  sketch  "3D эскиз1565"
  sketch  "3D эскиз1566"
  sketch  "3D эскиз1567"
  sketch  "3D эскиз1568"
  sketch  "3D эскиз1569"
  sketch  "3D эскиз1570"
  sketch  "3D эскиз1571"
  sketch  "3D эскиз1572"
  sketch  "3D эскиз1573"
  sketch  "3D эскиз1574"
  sketch  "3D эскиз1575"
  sketch  "3D эскиз1576"
  sketch  "3D эскиз1577"
  sketch  "3D эскиз1578"
  sketch  "3D эскиз1579"
  sketch  "3D эскиз1580"
  sketch  "3D эскиз1581"
  sketch  "3D эскиз1582"
  sketch  "3D эскиз1583"
  sketch  "3D эскиз1584"
  sketch  "3D эскиз1585"
  sketch  "3D эскиз1586"
  sketch  "3D эскиз1587"
  sketch  "3D эскиз1588"
  sketch  "3D эскиз1589"
  sketch  "3D эскиз1590"
  sketch  "3D эскиз1591"
  sketch  "3D эскиз1592"
  sketch  "3D эскиз1593"
  sketch  "3D эскиз1594"
  sketch  "3D эскиз1595"
  sketch  "3D эскиз1596"
  sketch  "3D эскиз1597"
  sketch  "3D эскиз1598"
  sketch  "3D эскиз1599"
  sketch  "3D эскиз1600"
  sketch  "3D эскиз1601"
  sketch  "3D эскиз1602"
  sketch  "3D эскиз1603"
  sketch  "3D эскиз1604"
  sketch  "3D эскиз1605"
  sketch  "3D эскиз1606"
  sketch  "3D эскиз1607"
  sketch  "3D эскиз1608"
  sketch  "3D эскиз1609"
  sketch  "3D эскиз1610"
  sketch  "3D эскиз1611"
  sketch  "3D эскиз1612"
  sketch  "3D эскиз1613"
  sketch  "3D эскиз1614"
  sketch  "3D эскиз1615"
  sketch  "3D эскиз1616"
  sketch  "3D эскиз1617"
  sketch  "3D эскиз1618"
  sketch  "3D эскиз1619"
  sketch  "3D эскиз1620"
  sketch  "3D эскиз1621"
  sketch  "3D эскиз1622"
  sketch  "3D эскиз1623"
  sketch  "3D эскиз1624"
  sketch  "3D эскиз1625"
  sketch  "3D эскиз1626"
  sketch  "3D эскиз1627"
  sketch  "3D эскиз1628"
  sketch  "3D эскиз1629"
  sketch  "3D эскиз1630"
  sketch  "3D эскиз1631"
  sketch  "3D эскиз1632"
  sketch  "3D эскиз1633"
  sketch  "3D эскиз1634"
  sketch  "3D эскиз1635"
  sketch  "3D эскиз1636"
  sketch  "3D эскиз1637"
  sketch  "3D эскиз1638"
  sketch  "3D эскиз1639"
  sketch  "3D эскиз1640"
  sketch  "3D эскиз1641"
  sketch  "3D эскиз1642"
  sketch  "3D эскиз1643"
  sketch  "3D эскиз1644"
  sketch  "3D эскиз1645"
  sketch  "3D эскиз1646"
  sketch  "3D эскиз1647"
  sketch  "3D эскиз1648"
  sketch  "3D эскиз1649"
  sketch  "3D эскиз1650"
  sketch  "3D эскиз1651"
  sketch  "3D эскиз1652"
  sketch  "3D эскиз1653"
  sketch  "3D эскиз1654"
  sketch  "3D эскиз1655"
  sketch  "3D эскиз1656"
  sketch  "3D эскиз1657"
  sketch  "3D эскиз1658"
  sketch  "3D эскиз1659"
  sketch  "3D эскиз1660"
  sketch  "3D эскиз1661"
  sketch  "3D эскиз1662"
  sketch  "3D эскиз1663"
  sketch  "3D эскиз1664"
  sketch  "3D эскиз1665"
  sketch  "3D эскиз1666"
  sketch  "3D эскиз1667"
  sketch  "3D эскиз1668"
  sketch  "3D эскиз1669"
  sketch  "3D эскиз1670"
  sketch  "3D эскиз1671"
  sketch  "3D эскиз1672"
  sketch  "3D эскиз1673"
  sketch  "3D эскиз1674"
  sketch  "3D эскиз1675"
  sketch  "3D эскиз1676"
  sketch  "3D эскиз1677"
  sketch  "3D эскиз1678"
  sketch  "3D эскиз1679"
  sketch  "3D эскиз1680"
  sketch  "3D эскиз1681"
  sketch  "3D эскиз1682"
  sketch  "3D эскиз1683"
  sketch  "3D эскиз1684"
  sketch  "3D эскиз1685"
  sketch  "3D эскиз1686"
  sketch  "3D эскиз1687"
  sketch  "3D эскиз1688"
  sketch  "3D эскиз1689"
  sketch  "3D эскиз1690"
  sketch  "3D эскиз1691"
  sketch  "3D эскиз1692"
  sketch  "3D эскиз1693"
  sketch  "3D эскиз1694"
  sketch  "3D эскиз1695"
  sketch  "3D эскиз1696"
  sketch  "3D эскиз1697"
  sketch  "3D эскиз1698"
  sketch  "3D эскиз1699"
  sketch  "3D эскиз1700"
  sketch  "3D эскиз1701"
  sketch  "3D эскиз1702"
  sketch  "3D эскиз1703"
  sketch  "3D эскиз1704"
  sketch  "3D эскиз1705"
  sketch  "3D эскиз1706"
  sketch  "3D эскиз1707"
  sketch  "3D эскиз1708"
  sketch  "3D эскиз1709"
  sketch  "3D эскиз1710"
  sketch  "3D эскиз1711"
  sketch  "3D эскиз1712"
  sketch  "3D эскиз1713"
  sketch  "3D эскиз1714"
  sketch  "3D эскиз1715"
  sketch  "3D эскиз1716"
  sketch  "3D эскиз1717"
  sketch  "3D эскиз1718"
  sketch  "3D эскиз1719"
  sketch  "3D эскиз1720"
  sketch  "3D эскиз1721"
  sketch  "3D эскиз1722"
  sketch  "3D эскиз1723"
  sketch  "3D эскиз1724"
  sketch  "3D эскиз1725"
  sketch  "3D эскиз1726"
  sketch  "3D эскиз1727"
  sketch  "3D эскиз1728"
  sketch  "3D эскиз1729"
  sketch  "3D эскиз1730"
  sketch  "3D эскиз1731"
  sketch  "3D эскиз1732"
  sketch  "3D эскиз1733"
  sketch  "3D эскиз1734"
  sketch  "3D эскиз1735"
  sketch  "3D эскиз1736"
  sketch  "3D эскиз1737"
  sketch  "3D эскиз1738"
  sketch  "3D эскиз1739"
  sketch  "3D эскиз1740"
  sketch  "3D эскиз1741"
  sketch  "3D эскиз1742"
  sketch  "3D эскиз1743"
  sketch  "3D эскиз1744"
  sketch  "3D эскиз1745"
  sketch  "3D эскиз1746"
  sketch  "3D эскиз1747"
  sketch  "3D эскиз1748"
  sketch  "3D эскиз1749"
  sketch  "3D эскиз1750"
  sketch  "3D эскиз1751"
  sketch  "3D эскиз1752"
  sketch  "3D эскиз1753"
  sketch  "3D эскиз1754"
  sketch  "3D эскиз1755"
  sketch  "3D эскиз1756"
  sketch  "3D эскиз1757"
  sketch  "3D эскиз1758"
  sketch  "3D эскиз1759"
  sketch  "3D эскиз1760"
  sketch  "3D эскиз1761"
  sketch  "3D эскиз1762"
  sketch  "3D эскиз1763"
  sketch  "3D эскиз1764"
  sketch  "3D эскиз1765"
  sketch  "3D эскиз1766"
  sketch  "3D эскиз1767"
  sketch  "3D эскиз1768"
  sketch  "3D эскиз1769"
  sketch  "3D эскиз1770"
  sketch  "3D эскиз1771"
  sketch  "3D эскиз1772"
  sketch  "3D эскиз1773"
  sketch  "3D эскиз1774"
  sketch  "3D эскиз1775"
  sketch  "3D эскиз1776"
  sketch  "3D эскиз1777"
  sketch  "3D эскиз1778"
  sketch  "3D эскиз1779"
  sketch  "3D эскиз1780"
  sketch  "3D эскиз1781"
  sketch  "3D эскиз1782"
  sketch  "3D эскиз1783"
  sketch  "3D эскиз1784"
  sketch  "3D эскиз1785"
  sketch  "3D эскиз1786"
  sketch  "3D эскиз1787"
  sketch  "3D эскиз1788"
  sketch  "3D эскиз1789"
  sketch  "3D эскиз1790"
  sketch  "3D эскиз1791"
  sketch  "3D эскиз1792"
  sketch  "3D эскиз1793"
  sketch  "3D эскиз1794"
  sketch  "3D эскиз1795"
  sketch  "3D эскиз1796"
  sketch  "3D эскиз1797"
  sketch  "3D эскиз1798"
  sketch  "3D эскиз1799"
  sketch  "3D эскиз1800"
  sketch  "3D эскиз1801"
  sketch  "3D эскиз1802"
  sketch  "3D эскиз1803"
  sketch  "3D эскиз1804"
  sketch  "3D эскиз1805"
  sketch  "3D эскиз1806"
  sketch  "3D эскиз1807"
  sketch  "3D эскиз1808"
  sketch  "3D эскиз1809"
  sketch  "3D эскиз1810"
  sketch  "3D эскиз1811"
  sketch  "3D эскиз1812"
  sketch  "3D эскиз1813"
  sketch  "3D эскиз1814"
  sketch  "3D эскиз1815"
  sketch  "3D эскиз1816"
  sketch  "3D эскиз1817"
  sketch  "3D эскиз1818"
  sketch  "3D эскиз1819"
  sketch  "3D эскиз1820"
  sketch  "3D эскиз1821"
  sketch  "3D эскиз1822"
  sketch  "3D эскиз1823"
  sketch  "3D эскиз1824"
  sketch  "3D эскиз1825"
  sketch  "3D эскиз1826"
  sketch  "3D эскиз1827"
  sketch  "3D эскиз1828"
  sketch  "3D эскиз1829"
  sketch  "3D эскиз1830"
  sketch  "3D эскиз1831"
  sketch  "3D эскиз1832"
  sketch  "3D эскиз1833"
  sketch  "3D эскиз1834"
  sketch  "3D эскиз1835"
  sketch  "3D эскиз1836"
  sketch  "3D эскиз1837"
  sketch  "3D эскиз1838"
  sketch  "3D эскиз1839"
  sketch  "3D эскиз1840"
  sketch  "3D эскиз1841"
  sketch  "3D эскиз1842"
  sketch  "3D эскиз1843"
  sketch  "3D эскиз1844"
  sketch  "3D эскиз1845"
  sketch  "3D эскиз1846"
  sketch  "3D эскиз1847"
  sketch  "3D эскиз1848"
  sketch  "3D эскиз1849"
  sketch  "3D эскиз1850"
  sketch  "3D эскиз1851"
  sketch  "3D эскиз1852"
  sketch  "3D эскиз1853"
  sketch  "3D эскиз1854"
  sketch  "3D эскиз1855"
  sketch  "3D эскиз1856"
  sketch  "3D эскиз1857"
  sketch  "3D эскиз1858"
  sketch  "3D эскиз1859"
  sketch  "3D эскиз1860"
  sketch  "3D эскиз1861"
  sketch  "3D эскиз1862"
  sketch  "3D эскиз1863"
  sketch  "3D эскиз1864"
  sketch  "3D эскиз1865"
  sketch  "3D эскиз1866"
  sketch  "3D эскиз1867"
  sketch  "3D эскиз1868"
  sketch  "3D эскиз1869"
  sketch  "3D эскиз1870"
  sketch  "3D эскиз1871"
  sketch  "3D эскиз1872"
  sketch  "3D эскиз1873"
  sketch  "3D эскиз1874"
  sketch  "3D эскиз1875"
  sketch  "3D эскиз1876"
  sketch  "3D эскиз1877"
  sketch  "3D эскиз1878"
  sketch  "3D эскиз1879"
  sketch  "3D эскиз1880"
  sketch  "3D эскиз1881"
  sketch  "3D эскиз1882"
  sketch  "3D эскиз1883"
  sketch  "3D эскиз1884"
  sketch  "3D эскиз1885"
  sketch  "3D эскиз1886"
  sketch  "3D эскиз1887"
  sketch  "3D эскиз1888"
  sketch  "3D эскиз1889"
  sketch  "3D эскиз1890"
  sketch  "3D эскиз1891"
  sketch  "3D эскиз1892"
  sketch  "3D эскиз1893"
  sketch  "3D эскиз1894"
  sketch  "3D эскиз1895"
  sketch  "3D эскиз1896"
  sketch  "3D эскиз1897"
  sketch  "3D эскиз1898"
  sketch  "3D эскиз1899"
  sketch  "3D эскиз1900"
  sketch  "3D эскиз1901"
  sketch  "3D эскиз1902"
  sketch  "3D эскиз1903"
  sketch  "3D эскиз1904"
  sketch  "3D эскиз1905"
  sketch  "3D эскиз1906"
  sketch  "3D эскиз1907"
  sketch  "3D эскиз1908"
  sketch  "3D эскиз1909"
  sketch  "3D эскиз1910"
  sketch  "3D эскиз1911"
  sketch  "3D эскиз1912"
  sketch  "3D эскиз1913"
  sketch  "3D эскиз1914"
  sketch  "3D эскиз1915"
  sketch  "3D эскиз1916"
  sketch  "3D эскиз1917"
  sketch  "3D эскиз1918"
  sketch  "3D эскиз1919"
  sketch  "3D эскиз1920"
  sketch  "3D эскиз1921"
  sketch  "3D эскиз1922"
  sketch  "3D эскиз1923"
  sketch  "3D эскиз1924"
  sketch  "3D эскиз1925"
  sketch  "3D эскиз1926"
  sketch  "3D эскиз1927"
  sketch  "3D эскиз1928"
  sketch  "3D эскиз1929"
  sketch  "3D эскиз1930"
  sketch  "3D эскиз1931"
  sketch  "3D эскиз1932"
  sketch  "3D эскиз1933"
  sketch  "3D эскиз1934"
  sketch  "3D эскиз1935"
  sketch  "3D эскиз1936"
  sketch  "3D эскиз1937"
  sketch  "3D эскиз1938"
  sketch  "3D эскиз1939"
  sketch  "3D эскиз1940"
  sketch  "3D эскиз1941"
  sketch  "3D эскиз1942"
  sketch  "3D эскиз1943"
  sketch  "3D эскиз1944"
  sketch  "3D эскиз1945"
  sketch  "3D эскиз1946"
  sketch  "3D эскиз1947"
  sketch  "3D эскиз1948"
  sketch  "3D эскиз1949"
  sketch  "3D эскиз1950"
  sketch  "3D эскиз1951"
  sketch  "3D эскиз1952"
  sketch  "3D эскиз1953"
  sketch  "3D эскиз1954"
  sketch  "3D эскиз1955"
  sketch  "3D эскиз1956"
  sketch  "3D эскиз1957"
  sketch  "3D эскиз1958"
  sketch  "3D эскиз1959"
  sketch  "3D эскиз1960"
  sketch  "3D эскиз1961"
  sketch  "3D эскиз1962"
  sketch  "3D эскиз1963"
  sketch  "3D эскиз1964"
  sketch  "3D эскиз1965"
  sketch  "3D эскиз1966"
  sketch  "3D эскиз1967"
  sketch  "3D эскиз1968"
  sketch  "3D эскиз1969"
  sketch  "3D эскиз1970"
  sketch  "3D эскиз1971"
  sketch  "3D эскиз1972"
  sketch  "3D эскиз1973"
  sketch  "3D эскиз1974"
  sketch  "3D эскиз1975"
  sketch  "3D эскиз1976"
  sketch  "3D эскиз1977"
  sketch  "3D эскиз1978"
  sketch  "3D эскиз1979"
  sketch  "3D эскиз1980"
  sketch  "3D эскиз1981"
  sketch  "3D эскиз1982"
  sketch  "3D эскиз1983"
  sketch  "3D эскиз1984"
  sketch  "3D эскиз1985"
  sketch  "3D эскиз1986"
  sketch  "3D эскиз1987"
  sketch  "3D эскиз1988"
  sketch  "3D эскиз1989"
  sketch  "3D эскиз1990"
  sketch  "3D эскиз1991"
  sketch  "3D эскиз1992"
  sketch  "3D эскиз1993"
  sketch  "3D эскиз1994"
  sketch  "3D эскиз1995"
  sketch  "3D эскиз1996"
  sketch  "3D эскиз1997"
  sketch  "3D эскиз1998"
  sketch  "3D эскиз1999"
  sketch  "3D эскиз2000"
  sketch  "3D эскиз2001"
  sketch  "3D эскиз2002"
  sketch  "3D эскиз2003"
  sketch  "3D эскиз2004"
  sketch  "3D эскиз2005"
  sketch  "3D эскиз2006"
  sketch  "3D эскиз2007"
  sketch  "3D эскиз2008"
  sketch  "3D эскиз2009"
  sketch  "3D эскиз2010"
  sketch  "3D эскиз2011"
  sketch  "3D эскиз2012"
  sketch  "3D эскиз2013"
  sketch  "3D эскиз2014"
  sketch  "3D эскиз2015"
  sketch  "3D эскиз2016"
  sketch  "3D эскиз2017"
  sketch  "3D эскиз2018"
  sketch  "3D эскиз2019"
  sketch  "3D эскиз2020"
  sketch  "3D эскиз2021"
  sketch  "3D эскиз2022"
  sketch  "3D эскиз2023"
  sketch  "3D эскиз2024"
  sketch  "3D эскиз2025"
  sketch  "3D эскиз2026"
  sketch  "3D эскиз2027"
  sketch  "3D эскиз2028"
  sketch  "3D эскиз2029"
  sketch  "3D эскиз2030"
  sketch  "3D эскиз2031"
  sketch  "3D эскиз2032"
  sketch  "3D эскиз2033"
  sketch  "3D эскиз2034"
  sketch  "3D эскиз2035"
  sketch  "3D эскиз2036"
  sketch  "3D эскиз2037"
  sketch  "3D эскиз2038"
  sketch  "3D эскиз2039"
  sketch  "3D эскиз2040"
  sketch  "3D эскиз2041"
  sketch  "3D эскиз2042"
  sketch  "3D эскиз2043"
  sketch  "3D эскиз2044"
  sketch  "3D эскиз2045"
  sketch  "3D эскиз2046"
  sketch  "3D эскиз2047"
  sketch  "3D эскиз2048"
  sketch  "3D эскиз2049"
  sketch  "3D эскиз2050"
  sketch  "3D эскиз2051"
  sketch  "3D эскиз2052"
  sketch  "3D эскиз2053"
  sketch  "3D эскиз2054"
  sketch  "3D эскиз2055"
  sketch  "3D эскиз2056"
  sketch  "3D эскиз2057"
  sketch  "3D эскиз2058"
  sketch  "3D эскиз2059"
  sketch  "3D эскиз2060"
  sketch  "3D эскиз2061"
  sketch  "3D эскиз2062"
  sketch  "3D эскиз2063"
  sketch  "3D эскиз2064"
  sketch  "3D эскиз2065"
  sketch  "3D эскиз2066"
  sketch  "3D эскиз2067"
  sketch  "3D эскиз2068"
  sketch  "3D эскиз2069"
  sketch  "3D эскиз2070"
  sketch  "3D эскиз2071"
  sketch  "3D эскиз2072"
  sketch  "3D эскиз2073"
  sketch  "3D эскиз2074"
  sketch  "3D эскиз2075"
  sketch  "3D эскиз2076"
  sketch  "3D эскиз2077"
  sketch  "3D эскиз2078"
  sketch  "3D эскиз2079"
  sketch  "3D эскиз2080"
  sketch  "3D эскиз2081"
  sketch  "3D эскиз2082"
  sketch  "3D эскиз2083"
  sketch  "3D эскиз2084"
  sketch  "3D эскиз2085"
  sketch  "3D эскиз2086"
  sketch  "3D эскиз2087"
  sketch  "3D эскиз2088"
  sketch  "3D эскиз2089"
  sketch  "3D эскиз2090"
  sketch  "3D эскиз2091"
  sketch  "3D эскиз2092"
  sketch  "3D эскиз2093"
  sketch  "3D эскиз2094"
  sketch  "3D эскиз2095"
  sketch  "3D эскиз2096"
  sketch  "3D эскиз2097"
  sketch  "3D эскиз2098"
  sketch  "3D эскиз2099"
  sketch  "3D эскиз2100"
  sketch  "3D эскиз2101"
  sketch  "3D эскиз2102"
  sketch  "3D эскиз2103"
  sketch  "3D эскиз2104"
  sketch  "3D эскиз2105"
  sketch  "3D эскиз2106"
  sketch  "3D эскиз2107"
  sketch  "3D эскиз2108"
  sketch  "3D эскиз2109"
  sketch  "3D эскиз2110"
  sketch  "3D эскиз2111"
  sketch  "3D эскиз2112"
  sketch  "3D эскиз2113"
  sketch  "3D эскиз2114"
  sketch  "3D эскиз2115"
  sketch  "3D эскиз2116"
  sketch  "3D эскиз2117"
  sketch  "3D эскиз2118"
  sketch  "3D эскиз2119"
  sketch  "3D эскиз2120"
  sketch  "3D эскиз2121"
  sketch  "3D эскиз2122"
  sketch  "3D эскиз2123"
  sketch  "3D эскиз2124"
  sketch  "3D эскиз2125"
  sketch  "3D эскиз2126"
  sketch  "3D эскиз2127"
  sketch  "3D эскиз2128"
  sketch  "3D эскиз2129"
  sketch  "3D эскиз2130"
  sketch  "3D эскиз2131"
  sketch  "3D эскиз2132"
  sketch  "3D эскиз2133"
  sketch  "3D эскиз2134"
  sketch  "3D эскиз2135"
  sketch  "3D эскиз2136"
  sketch  "3D эскиз2137"
  sketch  "3D эскиз2138"
  sketch  "3D эскиз2139"
  sketch  "3D эскиз2140"
  sketch  "3D эскиз2141"
  sketch  "3D эскиз2142"
  sketch  "3D эскиз2143"
  sketch  "3D эскиз2144"
  sketch  "3D эскиз2145"
  sketch  "3D эскиз2146"
  sketch  "3D эскиз2147"
  sketch  "3D эскиз2148"
  sketch  "3D эскиз2149"
  sketch  "3D эскиз2150"
  sketch  "3D эскиз2151"
  sketch  "3D эскиз2152"
  sketch  "3D эскиз2153"
  sketch  "3D эскиз2154"
  sketch  "3D эскиз2155"
  sketch  "3D эскиз2156"
  sketch  "3D эскиз2157"
  sketch  "3D эскиз2158"
  sketch  "3D эскиз2159"
  sketch  "3D эскиз2160"
  sketch  "3D эскиз2161"
  sketch  "3D эскиз2162"
  sketch  "3D эскиз2163"
  sketch  "3D эскиз2164"
  sketch  "3D эскиз2165"
  sketch  "3D эскиз2166"
  sketch  "3D эскиз2167"
  sketch  "3D эскиз2168"
  sketch  "3D эскиз2169"
  sketch  "3D эскиз2170"
  sketch  "3D эскиз2171"
  sketch  "3D эскиз2172"
  sketch  "3D эскиз2173"
  sketch  "3D эскиз2174"
  sketch  "3D эскиз2175"
  sketch  "3D эскиз2176"
  sketch  "3D эскиз2177"
  sketch  "3D эскиз2178"
  sketch  "3D эскиз2179"
  sketch  "3D эскиз2180"
  sketch  "3D эскиз2181"
  sketch  "3D эскиз2182"
  sketch  "3D эскиз2183"
  sketch  "3D эскиз2184"
  sketch  "3D эскиз2185"
  sketch  "3D эскиз2186"
  sketch  "3D эскиз2187"
  sketch  "3D эскиз2188"
  sketch  "3D эскиз2189"
  sketch  "3D эскиз2190"
  sketch  "3D эскиз2191"
  sketch  "3D эскиз2192"
  sketch  "3D эскиз2193"
  sketch  "3D эскиз2194"
  sketch  "3D эскиз2195"
  sketch  "3D эскиз2196"
  sketch  "3D эскиз2197"
  sketch  "3D эскиз2198"
  sketch  "3D эскиз2199"
  sketch  "3D эскиз2200"
  sketch  "3D эскиз2201"
  sketch  "3D эскиз2202"
  sketch  "3D эскиз2203"
  sketch  "3D эскиз2204"
  sketch  "3D эскиз2205"
  sketch  "3D эскиз2206"
  sketch  "3D эскиз2207"
  sketch  "3D эскиз2208"
  sketch  "3D эскиз2209"
  sketch  "3D эскиз2210"
  sketch  "3D эскиз2211"
  sketch  "3D эскиз2212"
  sketch  "3D эскиз2213"
  sketch  "3D эскиз2214"
  sketch  "3D эскиз2215"
  sketch  "3D эскиз2216"
  sketch  "3D эскиз2217"
  sketch  "3D эскиз2218"
  sketch  "3D эскиз2219"
  sketch  "3D эскиз2220"
  sketch  "3D эскиз2221"
  sketch  "3D эскиз2222"
  sketch  "3D эскиз2223"
  sketch  "3D эскиз2224"
  sketch  "3D эскиз2225"
  sketch  "3D эскиз2226"
  sketch  "3D эскиз2227"
  sketch  "3D эскиз2228"
  sketch  "3D эскиз2229"
  sketch  "3D эскиз2230"
  sketch  "3D эскиз2231"
  sketch  "3D эскиз2232"
  sketch  "3D эскиз2233"
  sketch  "3D эскиз2234"
  sketch  "3D эскиз2235"
  sketch  "3D эскиз2236"
  sketch  "3D эскиз2237"
  sketch  "3D эскиз2238"
  sketch  "3D эскиз2239"
  sketch  "3D эскиз2240"
  sketch  "3D эскиз2241"
  sketch  "3D эскиз2242"
  sketch  "3D эскиз2243"
  sketch  "3D эскиз2244"
  sketch  "3D эскиз2245"
  sketch  "3D эскиз2246"
  sketch  "3D эскиз2247"
  sketch  "3D эскиз2248"
  sketch  "3D эскиз2249"
  sketch  "3D эскиз2250"
  sketch  "3D эскиз2251"
  sketch  "3D эскиз2252"
  sketch  "3D эскиз2253"
  sketch  "3D эскиз2254"
  sketch  "3D эскиз2255"
  sketch  "3D эскиз2256"
  sketch  "3D эскиз2257"
  sketch  "3D эскиз2258"
  sketch  "3D эскиз2259"
  sketch  "3D эскиз2260"
  sketch  "3D эскиз2261"
  sketch  "3D эскиз2262"
  sketch  "3D эскиз2263"
  sketch  "3D эскиз2264"
  sketch  "3D эскиз2265"
  sketch  "3D эскиз2266"
  sketch  "3D эскиз2267"
  sketch  "3D эскиз2268"
  sketch  "3D эскиз2269"
  sketch  "3D эскиз2270"
  sketch  "3D эскиз2271"
  sketch  "3D эскиз2272"
  sketch  "3D эскиз2273"
  sketch  "3D эскиз2274"
  sketch  "3D эскиз2275"
  sketch  "3D эскиз2276"
  sketch  "3D эскиз2277"
  sketch  "3D эскиз2278"
  sketch  "3D эскиз2279"
  sketch  "3D эскиз2280"
  sketch  "3D эскиз2281"
  sketch  "3D эскиз2282"
  sketch  "3D эскиз2283"
  sketch  "3D эскиз2284"
  sketch  "3D эскиз2285"
  sketch  "3D эскиз2286"
  sketch  "3D эскиз2287"
  sketch  "3D эскиз2288"
  sketch  "3D эскиз2289"
  sketch  "3D эскиз2290"
  sketch  "3D эскиз2291"
  sketch  "3D эскиз2292"
  sketch  "3D эскиз2293"
  sketch  "3D эскиз2294"
  sketch  "3D эскиз2295"
  sketch  "3D эскиз2296"
  sketch  "3D эскиз2297"
  sketch  "3D эскиз2298"
  sketch  "3D эскиз2299"
  sketch  "3D эскиз2300"
  sketch  "3D эскиз2301"
  sketch  "3D эскиз2302"
  sketch  "3D эскиз2303"
  sketch  "3D эскиз2304"
  sketch  "3D эскиз2305"
  sketch  "3D эскиз2306"
  sketch  "3D эскиз2307"
  sketch  "3D эскиз2308"
  sketch  "3D эскиз2309"
  sketch  "3D эскиз2310"
  sketch  "3D эскиз2311"
  sketch  "3D эскиз2312"
  sketch  "3D эскиз2313"
  sketch  "3D эскиз2314"
  sketch  "3D эскиз2315"
  sketch  "3D эскиз2316"
  sketch  "3D эскиз2317"
  sketch  "3D эскиз2318"
  sketch  "3D эскиз2319"
  sketch  "3D эскиз2320"
  sketch  "3D эскиз2321"
  sketch  "3D эскиз2322"
  sketch  "3D эскиз2323"
  sketch  "3D эскиз2324"
  sketch  "3D эскиз2325"
  sketch  "3D эскиз2326"
  sketch  "3D эскиз2327"
  sketch  "3D эскиз2328"
  sketch  "3D эскиз2329"
  sketch  "3D эскиз2330"
  sketch  "3D эскиз2331"
  sketch  "3D эскиз2332"
  sketch  "3D эскиз2333"
  sketch  "3D эскиз2334"
  sketch  "3D эскиз2335"
  sketch  "3D эскиз2336"
  sketch  "3D эскиз2337"
  sketch  "3D эскиз2338"
  sketch  "3D эскиз2339"
  sketch  "3D эскиз2340"
  sketch  "3D эскиз2341"
  sketch  "3D эскиз2342"
  sketch  "3D эскиз2343"
  sketch  "3D эскиз2344"
  sketch  "3D эскиз2345"
  sketch  "3D эскиз2346"
  sketch  "3D эскиз2347"
  sketch  "3D эскиз2348"
  sketch  "3D эскиз2349"
  sketch  "3D эскиз2350"
  sketch  "3D эскиз2351"
  sketch  "3D эскиз2352"
  sketch  "3D эскиз2353"
  sketch  "3D эскиз2354"
  sketch  "3D эскиз2355"
  sketch  "3D эскиз2356"
  sketch  "3D эскиз2357"
  sketch  "3D эскиз2358"
  sketch  "3D эскиз2359"
  sketch  "3D эскиз2360"
  sketch  "3D эскиз2361"
  sketch  "3D эскиз2362"
  sketch  "3D эскиз2363"
  sketch  "3D эскиз2364"
  sketch  "3D эскиз2365"
  sketch  "3D эскиз2366"
  sketch  "3D эскиз2367"
  sketch  "3D эскиз2368"
  sketch  "3D эскиз2369"
  sketch  "3D эскиз2370"
  sketch  "3D эскиз2371"
  sketch  "3D эскиз2372"
  sketch  "3D эскиз2373"
  sketch  "3D эскиз2374"
  sketch  "3D эскиз2375"
  sketch  "3D эскиз2376"
  sketch  "3D эскиз2377"
  sketch  "3D эскиз2378"
  sketch  "3D эскиз2379"
  sketch  "3D эскиз2380"
  sketch  "3D эскиз2381"
  sketch  "3D эскиз2382"
  sketch  "3D эскиз2383"
  sketch  "3D эскиз2384"
  sketch  "3D эскиз2385"
  sketch  "3D эскиз2386"
  sketch  "3D эскиз2387"
  sketch  "3D эскиз2388"
  sketch  "3D эскиз2389"
  sketch  "3D эскиз2390"
  sketch  "3D эскиз2391"
  sketch  "3D эскиз2392"
  sketch  "3D эскиз2393"
  sketch  "3D эскиз2394"
  sketch  "3D эскиз2395"
  sketch  "3D эскиз2396"
  sketch  "3D эскиз2397"
  sketch  "3D эскиз2398"
  sketch  "3D эскиз2399"
  sketch  "3D эскиз2400"
  sketch  "3D эскиз2401"
  sketch  "3D эскиз2402"
  sketch  "3D эскиз2403"
  sketch  "3D эскиз2404"
  sketch  "3D эскиз2405"
  sketch  "3D эскиз2406"
  sketch  "3D эскиз2407"
  sketch  "3D эскиз2408"
  sketch  "3D эскиз2409"
  sketch  "3D эскиз2410"
  sketch  "3D эскиз2411"
  sketch  "3D эскиз2412"
  sketch  "3D эскиз2413"
  sketch  "3D эскиз2414"
  sketch  "3D эскиз2415"
  sketch  "3D эскиз2416"
  sketch  "3D эскиз2417"
  sketch  "3D эскиз2418"
  sketch  "3D эскиз2419"
  sketch  "3D эскиз2420"
  sketch  "3D эскиз2421"
  sketch  "3D эскиз2422"
  sketch  "3D эскиз2423"
  sketch  "3D эскиз2424"
  sketch  "3D эскиз2425"
  sketch  "3D эскиз2426"
  sketch  "3D эскиз2427"
  sketch  "3D эскиз2428"
  sketch  "3D эскиз2429"
  sketch  "3D эскиз2430"
  sketch  "3D эскиз2431"
  sketch  "3D эскиз2432"
  sketch  "3D эскиз2433"
  sketch  "3D эскиз2434"
  sketch  "3D эскиз2435"
  sketch  "3D эскиз2436"
  sketch  "3D эскиз2437"
  sketch  "3D эскиз2438"
  sketch  "3D эскиз2439"
  sketch  "3D эскиз2440"
  sketch  "3D эскиз2441"
  sketch  "3D эскиз2442"
  sketch  "3D эскиз2443"
  sketch  "3D эскиз2444"
  sketch  "3D эскиз2445"
  sketch  "3D эскиз2446"
  sketch  "3D эскиз2447"
  other  "Твердое тело2"
  other  "Твердое тело3"
  other  "Твердое тело4"
  other  "Твердое тело5"
  other  "Твердое тело6"
  other  "Твердое тело7"
  other  "Твердое тело8"
  other  "Твердое тело9"
  other  "Твердое тело10"
  other  "Твердое тело11"
  other  "Твердое тело12"
  other  "Твердое тело13"
  other  "Твердое тело14"
  other  "Твердое тело15"
  other  "Твердое тело16"
  other  "Твердое тело17"
  other  "Твердое тело18"
  other  "Твердое тело19"
  other  "Твердое тело20"
  other  "Твердое тело21"
  other  "Твердое тело22"
  other  "Твердое тело23"
  other  "Твердое тело24"
  other  "Твердое тело25"
  other  "Твердое тело26"
  other  "Твердое тело27"
  other  "Твердое тело28"
  other  "Твердое тело29"
  other  "Твердое тело30"
  other  "Твердое тело31"
  other  "Твердое тело32"
  other  "Твердое тело33"
  other  "Твердое тело34"
  other  "Твердое тело35"
  other  "Твердое тело36"
  other  "Твердое тело37"
  other  "Твердое тело38"
  other  "Твердое тело39"
  other  "Твердое тело40"
  other  "Твердое тело41"
  other  "Твердое тело42"
  other  "Твердое тело43"
  other  "Твердое тело44"
  other  "Твердое тело45"
  other  "Твердое тело46"
  other  "Твердое тело47"
  other  "Твердое тело48"
  other  "Твердое тело49"
  other  "Твердое тело50"
  other  "Твердое тело51"
  other  "Твердое тело52"
  other  "Твердое тело53"
  other  "Твердое тело54"
  other  "Твердое тело55"
  other  "Твердое тело56"
  other  "Твердое тело57"
  other  "Твердое тело58"
  other  "Твердое тело59"
  other  "Твердое тело60"
  other  "Твердое тело61"
  other  "Твердое тело62"
  other  "Твердое тело63"
  other  "Твердое тело64"
  other  "Твердое тело65"
  other  "Твердое тело66"
  other  "Твердое тело67"
  other  "Твердое тело68"
  other  "Твердое тело69"
  other  "Твердое тело70"
  other  "Твердое тело71"
  other  "Твердое тело72"
  other  "Твердое тело73"
  other  "Твердое тело74"
  other  "Твердое тело75"
  other  "Твердое тело76"
  other  "Твердое тело77"
  other  "Твердое тело78"
  other  "Твердое тело79"
  other  "Твердое тело80"
  other  "Твердое тело81"
  other  "Твердое тело82"
  other  "Твердое тело83"
  other  "Твердое тело84"
  other  "Твердое тело85"
  other  "Твердое тело86"
  other  "Твердое тело87"
  other  "Твердое тело88"
  other  "Твердое тело89"
  other  "Твердое тело90"
  other  "Твердое тело91"
  other  "Твердое тело92"
  other  "Твердое тело93"
  other  "Твердое тело94"
  other  "Твердое тело95"
  other  "Твердое тело96"
  other  "Твердое тело97"
  other  "Твердое тело98"
  other  "Твердое тело99"
  other  "Твердое тело100"
  other  "Твердое тело101"
  other  "Твердое тело102"
  other  "Твердое тело103"
  other  "Твердое тело104"
  other  "Твердое тело105"
  other  "Твердое тело106"
  other  "Твердое тело107"
  other  "Твердое тело108"
  other  "Твердое тело109"
  other  "Твердое тело110"
  other  "Твердое тело111"
  other  "Твердое тело112"
  other  "Твердое тело113"
  other  "Твердое тело114"
  other  "Твердое тело115"
  other  "Твердое тело116"
  other  "Твердое тело117"
  other  "Твердое тело118"
  other  "Твердое тело119"
  other  "Твердое тело120"
  other  "Твердое тело121"
  other  "Твердое тело122"
  other  "Твердое тело123"
  other  "Твердое тело124"
  other  "Твердое тело125"
  other  "Твердое тело126"
  other  "Твердое тело127"
  other  "Твердое тело128"
  other  "Твердое тело129"
  other  "Твердое тело130"
  other  "Твердое тело131"
  other  "Твердое тело132"
  other  "Твердое тело133"
  other  "Твердое тело134"
  other  "Твердое тело135"
  other  "Твердое тело136"
  other  "Твердое тело137"
  other  "Твердое тело138"
  other  "Твердое тело139"
  other  "Твердое тело140"
  other  "Твердое тело141"
  other  "Твердое тело142"
  other  "Твердое тело143"
  other  "Твердое тело144"
  other  "Твердое тело145"
  other  "Твердое тело146"
  other  "Твердое тело147"
  other  "Твердое тело148"
  other  "Твердое тело149"
  other  "Твердое тело150"
  other  "Твердое тело151"
  other  "Твердое тело152"
  other  "Твердое тело153"
  other  "Твердое тело154"
  other  "Твердое тело155"
  other  "Твердое тело156"
  other  "Твердое тело157"
  other  "Твердое тело158"
  other  "Твердое тело159"
  other  "Твердое тело160"
  other  "Твердое тело161"
  other  "Твердое тело162"
  other  "Твердое тело163"
  other  "Твердое тело164"
  other  "Твердое тело165"
  other  "Твердое тело166"
  other  "Твердое тело167"
  other  "Твердое тело168"
  other  "Твердое тело169"
  other  "Твердое тело170"
  other  "Твердое тело171"
  other  "Твердое тело172"
  other  "Твердое тело173"
  other  "Твердое тело174"
  other  "Твердое тело175"
  other  "Твердое тело176"
  other  "Твердое тело177"
  other  "Твердое тело178"
  other  "Твердое тело179"
  other  "Твердое тело180"
  other  "Твердое тело181"
  other  "Твердое тело182"
  other  "Твердое тело183"
  other  "Твердое тело184"
  other  "Твердое тело185"
  other  "Твердое тело186"
  other  "Твердое тело187"
  other  "Твердое тело188"
  other  "Твердое тело189"
  other  "Твердое тело190"
  other  "Твердое тело191"
  other  "Твердое тело192"
  other  "Твердое тело193"
  other  "Твердое тело194"
  other  "Твердое тело195"
  other  "Твердое тело196"
  other  "Твердое тело197"
  other  "Твердое тело198"
  other  "Твердое тело199"
  other  "Твердое тело200"
  other  "Твердое тело201"
  other  "Твердое тело202"
  other  "Твердое тело203"
  other  "Твердое тело204"
  other  "Твердое тело205"
  other  "Твердое тело206"
  other  "Твердое тело207"
  other  "Твердое тело208"
  other  "Твердое тело209"
  other  "Твердое тело210"
  other  "Твердое тело211"
  other  "Твердое тело212"
  other  "Твердое тело213"
  other  "Твердое тело214"
  other  "Твердое тело215"
  other  "Твердое тело216"
  other  "Твердое тело217"
  other  "Твердое тело218"
  other  "Твердое тело219"
  other  "Твердое тело220"
  other  "Твердое тело221"
  other  "Твердое тело222"
  other  "Твердое тело223"
  other  "Твердое тело224"
  other  "Твердое тело225"
  other  "Твердое тело226"
  other  "Твердое тело227"
  other  "Твердое тело228"
  other  "Твердое тело229"
  other  "Твердое тело230"
  other  "Твердое тело231"
  other  "Твердое тело232"
  other  "Твердое тело233"
  other  "Твердое тело234"
  other  "Твердое тело235"
  other  "Твердое тело236"
  other  "Твердое тело237"
  other  "Твердое тело238"
  other  "Твердое тело239"
  other  "Твердое тело240"
  other  "Твердое тело241"
  other  "Твердое тело242"
  other  "Твердое тело243"
  other  "Твердое тело244"
  other  "Твердое тело245"
  other  "Твердое тело246"
  other  "Твердое тело247"
  other  "Твердое тело248"
  other  "Твердое тело249"
  other  "Твердое тело250"
  other  "Твердое тело251"
  other  "Твердое тело252"
  other  "Твердое тело253"
  other  "Твердое тело254"
  other  "Твердое тело255"
  other  "Твердое тело256"
  other  "Твердое тело257"
  other  "Твердое тело258"
  other  "Твердое тело259"
  other  "Твердое тело260"
  other  "Твердое тело261"
  other  "Твердое тело262"
  other  "Твердое тело263"
  other  "Твердое тело264"
  other  "Твердое тело265"
  other  "Твердое тело266"
  other  "Твердое тело267"
  other  "Твердое тело268"
  other  "Твердое тело269"
  other  "Твердое тело270"
  other  "Твердое тело271"
  other  "Твердое тело272"
  other  "Твердое тело273"
  other  "Твердое тело274"
  other  "Твердое тело275"
  other  "Твердое тело276"
  other  "Твердое тело277"
  other  "Твердое тело278"
  other  "Твердое тело279"
  other  "Твердое тело280"
  other  "Твердое тело281"
  other  "Твердое тело282"
  other  "Твердое тело283"
  other  "Твердое тело284"
  other  "Твердое тело285"
  other  "Твердое тело286"
  other  "Твердое тело287"
  other  "Твердое тело288"
  other  "Твердое тело289"
  other  "Твердое тело290"
  other  "Твердое тело291"
  other  "Твердое тело292"
  other  "Твердое тело293"
  other  "Твердое тело294"
  other  "Твердое тело295"
  other  "Твердое тело296"
  other  "Твердое тело297"
  other  "Твердое тело298"
  other  "Твердое тело299"
  other  "Твердое тело300"
  other  "Твердое тело301"
  other  "Твердое тело302"
  other  "Твердое тело303"
  other  "Твердое тело304"
  other  "Твердое тело305"
  other  "Твердое тело306"
  other  "Твердое тело307"
  other  "Твердое тело308"
  other  "Твердое тело309"
  other  "Твердое тело310"
  other  "Твердое тело311"
  other  "Твердое тело312"
  other  "Твердое тело313"
  other  "Твердое тело314"
  other  "Твердое тело315"
  other  "Твердое тело316"
  other  "Твердое тело317"
  other  "Твердое тело318"
  other  "Твердое тело319"
  other  "Твердое тело320"
  other  "Твердое тело321"
  other  "Твердое тело322"
  other  "Твердое тело323"
  other  "Твердое тело324"
  other  "Твердое тело325"
  other  "Твердое тело326"
  other  "Твердое тело327"
  other  "Твердое тело328"
  other  "Твердое тело329"
  other  "Твердое тело330"
  other  "Твердое тело331"
  other  "Твердое тело332"
  other  "Твердое тело333"
  other  "Твердое тело334"
  other  "Твердое тело335"
  other  "Твердое тело336"
  other  "Твердое тело337"
  other  "Твердое тело338"
  other  "Твердое тело339"
  other  "Твердое тело340"
  other  "Твердое тело341"
  other  "Твердое тело342"
  other  "Твердое тело343"
  other  "Твердое тело344"
  other  "Твердое тело345"
  other  "Твердое тело346"
  other  "Твердое тело347"
  other  "Твердое тело348"
  other  "Твердое тело349"
  other  "Твердое тело350"
  other  "Твердое тело351"
  other  "Твердое тело352"
  other  "Твердое тело353"
  other  "Твердое тело354"
  other  "Твердое тело355"
  other  "Твердое тело356"
  other  "Твердое тело357"
  other  "Твердое тело358"
  other  "Твердое тело359"
  other  "Твердое тело360"
  other  "Твердое тело361"
  other  "Твердое тело362"
  other  "Твердое тело363"
  other  "Твердое тело364"
  other  "Твердое тело365"
  other  "Твердое тело366"
  other  "Твердое тело367"
  other  "Твердое тело368"
  other  "Твердое тело369"
  other  "Твердое тело370"
  other  "Твердое тело371"
  other  "Твердое тело372"
  other  "Твердое тело373"
  other  "Твердое тело374"
  other  "Твердое тело375"
  other  "Твердое тело376"
  other  "Твердое тело377"
  other  "Твердое тело378"
  other  "Твердое тело379"
  other  "Твердое тело380"
  other  "Твердое тело381"
  other  "Твердое тело382"
  other  "Твердое тело383"
  other  "Твердое тело384"
  other  "Твердое тело385"
  other  "Твердое тело386"
  other  "Твердое тело387"
  other  "Твердое тело388"
  other  "Твердое тело389"
  other  "Твердое тело390"
  other  "Твердое тело391"
  other  "Твердое тело392"
  other  "Твердое тело393"
  other  "Твердое тело394"
  other  "Твердое тело395"
  other  "Твердое тело396"
  other  "Твердое тело397"
  other  "Твердое тело398"
  other  "Твердое тело399"
  other  "Твердое тело400"
  other  "Твердое тело401"
  other  "Твердое тело402"
  other  "Твердое тело403"
  other  "Твердое тело404"
  other  "Твердое тело405"
  other  "Твердое тело406"
  other  "Твердое тело407"
  other  "Твердое тело408"
  other  "Твердое тело409"
  other  "Твердое тело410"
  other  "Твердое тело411"
  other  "Твердое тело412"
  other  "Твердое тело413"
  other  "Твердое тело414"
  other  "Твердое тело415"
  other  "Твердое тело416"
  other  "Твердое тело417"
  other  "Твердое тело418"
  other  "Твердое тело419"
  other  "Твердое тело420"
  other  "Твердое тело421"
  other  "Твердое тело422"
  other  "Твердое тело423"
  other  "Твердое тело424"
  other  "Твердое тело425"
  other  "Твердое тело426"
  other  "Твердое тело427"
  other  "Твердое тело428"
  other  "Твердое тело429"
  other  "Твердое тело430"
  other  "Твердое тело431"
  other  "Твердое тело432"
  other  "Твердое тело433"
  other  "Твердое тело434"
  other  "Твердое тело435"
  other  "Твердое тело436"
  other  "Твердое тело437"
  other  "Твердое тело438"
  other  "Твердое тело439"
  other  "Твердое тело440"
  other  "Твердое тело441"
  other  "Твердое тело442"
  other  "Твердое тело443"
  other  "Твердое тело444"
  other  "Твердое тело445"
  other  "Твердое тело446"
  other  "Твердое тело447"
  other  "Твердое тело448"
  other  "Твердое тело449"
  other  "Твердое тело450"
  other  "Твердое тело451"
  other  "Твердое тело452"
  other  "Твердое тело453"
  other  "Твердое тело454"
  other  "Твердое тело455"
  other  "Твердое тело456"
  other  "Твердое тело457"
  other  "Твердое тело458"
  other  "Твердое тело459"
  other  "Твердое тело460"
  other  "Твердое тело461"
  other  "Твердое тело462"
  other  "Твердое тело463"
  other  "Твердое тело464"
  other  "Твердое тело465"
  other  "Твердое тело466"
  other  "Твердое тело467"
  other  "Твердое тело468"
  other  "Твердое тело469"
  other  "Твердое тело470"
  other  "Твердое тело471"
  other  "Твердое тело472"
  other  "Твердое тело473"
  other  "Твердое тело474"
  other  "Твердое тело475"
  other  "Твердое тело476"
  other  "Твердое тело477"
  other  "Твердое тело478"
  other  "Твердое тело479"
  other  "Твердое тело480"
  other  "Твердое тело481"
  other  "Твердое тело482"
  other  "Твердое тело483"
  other  "Твердое тело484"
  other  "Твердое тело485"
  other  "Твердое тело486"
  other  "Твердое тело487"
  other  "Твердое тело488"
  other  "Твердое тело489"
  other  "Твердое тело490"
  other  "Твердое тело491"
  other  "Твердое тело492"
  other  "Твердое тело493"
  other  "Твердое тело494"
  other  "Твердое тело495"
  other  "Твердое тело496"
  other  "Твердое тело497"
  other  "Твердое тело498"
  other  "Твердое тело499"
  other  "Твердое тело500"
  other  "Твердое тело501"
  other  "Твердое тело502"
  other  "Твердое тело503"
  other  "Твердое тело504"
  other  "Твердое тело505"
  other  "Твердое тело506"
  other  "Твердое тело507"
  other  "Твердое тело508"
  other  "Твердое тело509"
  other  "Твердое тело510"
  other  "Твердое тело511"
  other  "Твердое тело512"
  other  "Твердое тело513"
  other  "Твердое тело514"
  other  "Твердое тело515"
  other  "Твердое тело516"
  other  "Твердое тело517"
  other  "Твердое тело518"
  other  "Твердое тело519"
  other  "Твердое тело520"
  other  "Твердое тело521"
  other  "Твердое тело522"
  other  "Твердое тело523"
  other  "Твердое тело524"
  other  "Твердое тело525"
  other  "Твердое тело526"
  other  "Твердое тело527"
  other  "Твердое тело528"
  other  "Твердое тело529"
  other  "Твердое тело530"
  other  "Твердое тело531"
  other  "Твердое тело532"
  other  "Твердое тело533"
  other  "Твердое тело534"
  other  "Твердое тело535"
  other  "Твердое тело536"
  other  "Твердое тело537"
  other  "Твердое тело538"
  other  "Твердое тело539"
  other  "Твердое тело540"
  other  "Твердое тело541"
  other  "Твердое тело542"
  other  "Твердое тело543"
  other  "Твердое тело544"
  other  "Твердое тело545"
  other  "Твердое тело546"
  other  "Твердое тело547"
  other  "Твердое тело548"
  other  "Твердое тело549"
  other  "Твердое тело550"
  other  "Твердое тело551"
  other  "Твердое тело552"
  other  "Твердое тело553"
  other  "Твердое тело554"
  other  "Твердое тело555"
  other  "Твердое тело556"
  other  "Твердое тело557"
  other  "Твердое тело558"
  other  "Твердое тело559"
  other  "Твердое тело560"
  other  "Твердое тело561"
  other  "Твердое тело562"
  other  "Твердое тело563"
  other  "Твердое тело564"
  other  "Твердое тело565"
  other  "Твердое тело566"
  other  "Твердое тело567"
  other  "Твердое тело568"
  other  "Твердое тело569"
  other  "Твердое тело570"
  other  "Твердое тело571"
  other  "Твердое тело572"
  other  "Твердое тело573"
  other  "Твердое тело574"
  other  "Твердое тело575"
  other  "Твердое тело576"
  other  "Твердое тело577"
  other  "Твердое тело578"
  other  "Твердое тело579"
  other  "Твердое тело580"
  other  "Твердое тело581"
  other  "Твердое тело582"
  other  "Твердое тело583"
  other  "Твердое тело584"
  other  "Твердое тело585"
  other  "Твердое тело586"
  other  "Твердое тело587"
  other  "Твердое тело588"
  other  "Твердое тело589"
  other  "Твердое тело590"
  other  "Твердое тело591"
  other  "Твердое тело592"
  other  "Твердое тело593"
  other  "Твердое тело594"
  other  "Твердое тело595"
  other  "Твердое тело596"
  other  "Твердое тело597"
  other  "Твердое тело598"
  other  "Твердое тело599"
  other  "Твердое тело600"
  other  "Твердое тело601"
  other  "Твердое тело602"
  other  "Твердое тело603"
  other  "Твердое тело604"
  other  "Твердое тело605"
  other  "Твердое тело606"
  other  "Твердое тело607"
  other  "Твердое тело608"
  other  "Твердое тело609"
  other  "Твердое тело610"
  other  "Твердое тело611"
  other  "Твердое тело612"
  other  "Твердое тело613"
  other  "Твердое тело614"
  other  "Твердое тело615"
  other  "Твердое тело616"
  other  "Твердое тело617"
  other  "Твердое тело618"
  other  "Твердое тело619"
  other  "Твердое тело620"
  other  "Твердое тело621"
  other  "Твердое тело622"
  other  "Твердое тело623"
  other  "Твердое тело624"
  other  "Твердое тело625"
  other  "Твердое тело626"
  other  "Твердое тело627"
  other  "Твердое тело628"
  other  "Твердое тело629"
  other  "Твердое тело630"
  other  "Твердое тело631"
  other  "Твердое тело632"
  other  "Твердое тело633"
  other  "Твердое тело634"
  other  "Твердое тело635"
  other  "Твердое тело636"
  other  "Твердое тело637"
  other  "Твердое тело638"
  other  "Твердое тело639"
  other  "Твердое тело640"
  other  "Твердое тело641"
  other  "Твердое тело642"
  other  "Твердое тело643"
  other  "Твердое тело644"
  other  "Твердое тело645"
  other  "Твердое тело646"
  other  "Твердое тело647"
  other  "Твердое тело648"
  other  "Твердое тело649"
  other  "Твердое тело650"
  other  "Твердое тело651"
  other  "Твердое тело652"
  other  "Твердое тело653"
  other  "Твердое тело654"
  other  "Твердое тело655"
  other  "Твердое тело656"
  other  "Твердое тело657"
  other  "Твердое тело658"
  other  "Твердое тело659"
  other  "Твердое тело660"
  other  "Твердое тело661"
  other  "Твердое тело662"
  other  "Твердое тело663"
  other  "Твердое тело664"
  other  "Твердое тело665"
  other  "Твердое тело666"
  other  "Твердое тело667"
  other  "Твердое тело668"
  other  "Твердое тело669"
  other  "Твердое тело670"
  other  "Твердое тело671"
  other  "Твердое тело672"
  other  "Твердое тело673"
  other  "Твердое тело674"
  other  "Твердое тело675"
  other  "Твердое тело676"
  other  "Твердое тело677"
  other  "Твердое тело678"
  other  "Твердое тело679"
  other  "Твердое тело680"
  other  "Твердое тело681"
  other  "Твердое тело682"
  other  "Твердое тело683"
  other  "Твердое тело684"
  other  "Твердое тело685"
  other  "Твердое тело686"
  other  "Твердое тело687"
  other  "Твердое тело688"
  other  "Твердое тело689"
  other  "Твердое тело690"
  other  "Твердое тело691"
  other  "Твердое тело692"
  other  "Твердое тело693"
  other  "Твердое тело694"
  other  "Твердое тело695"
  other  "Твердое тело696"
  other  "Твердое тело697"
  other  "Твердое тело698"
  other  "Твердое тело699"
  other  "Твердое тело700"
  other  "Твердое тело701"
  other  "Твердое тело702"
  other  "Твердое тело703"
  other  "Твердое тело704"
  other  "Твердое тело705"
  other  "Твердое тело706"
  other  "Твердое тело707"
  other  "Твердое тело708"
  other  "Твердое тело709"
  other  "Твердое тело710"
  other  "Твердое тело711"
  other  "Твердое тело712"
  other  "Твердое тело713"
  other  "Твердое тело714"
  other  "Твердое тело715"
  other  "Твердое тело716"
  other  "Твердое тело717"
  other  "Твердое тело718"
  other  "Твердое тело719"
  other  "Твердое тело720"
  other  "Твердое тело721"
  other  "Твердое тело722"
  other  "Твердое тело723"
  other  "Твердое тело724"
  other  "Твердое тело725"
  other  "Твердое тело726"
  other  "Твердое тело727"
  other  "Твердое тело728"
  other  "Твердое тело729"
  other  "Твердое тело730"
  other  "Твердое тело731"
  other  "Твердое тело732"
  other  "Твердое тело733"
  other  "Твердое тело734"
  other  "Твердое тело735"
  other  "Твердое тело736"
  other  "Твердое тело737"
  other  "Твердое тело738"
  other  "Твердое тело739"
  other  "Твердое тело740"
  other  "Твердое тело741"
  other  "Твердое тело742"
  other  "Твердое тело743"
  other  "Твердое тело744"
  other  "Твердое тело745"
  other  "Твердое тело746"
  other  "Твердое тело747"
  other  "Твердое тело748"
  other  "Твердое тело749"
  other  "Твердое тело750"
  other  "Твердое тело751"
  other  "Твердое тело752"
  other  "Твердое тело753"
  other  "Твердое тело754"
  other  "Твердое тело755"
  other  "Твердое тело756"
  other  "Твердое тело757"
  other  "Твердое тело758"
  other  "Твердое тело759"
  other  "Твердое тело760"
  other  "Твердое тело761"
  other  "Твердое тело762"
  other  "Твердое тело763"
  other  "Твердое тело764"
  other  "Твердое тело765"
  other  "Твердое тело766"
  other  "Твердое тело767"
  other  "Твердое тело768"
  other  "Твердое тело769"
  other  "Твердое тело770"
  other  "Твердое тело771"
  other  "Твердое тело772"
  other  "Твердое тело773"
  other  "Твердое тело774"
  other  "Твердое тело775"
  other  "Твердое тело776"
  other  "Твердое тело777"
  other  "Твердое тело778"
  other  "Твердое тело779"
  other  "Твердое тело780"
  other  "Твердое тело781"
  other  "Твердое тело782"
  other  "Твердое тело783"
  other  "Твердое тело784"
  other  "Твердое тело785"
  other  "Твердое тело786"
  other  "Твердое тело787"
  other  "Твердое тело788"
  other  "Твердое тело789"
  other  "Твердое тело790"
  other  "Твердое тело791"
  other  "Твердое тело792"
  other  "Твердое тело793"
  other  "Твердое тело794"
  other  "Твердое тело795"
  other  "Твердое тело796"
  other  "Твердое тело797"
  other  "Твердое тело798"
  other  "Твердое тело799"
  other  "Твердое тело800"
  other  "Твердое тело801"
  other  "Твердое тело802"
  other  "Твердое тело803"
  other  "Твердое тело804"
  other  "Твердое тело805"
  other  "Твердое тело806"
  other  "Твердое тело807"
  other  "Твердое тело808"
  other  "Твердое тело809"
  other  "Твердое тело810"
  other  "Твердое тело811"
  other  "Твердое тело812"
  other  "Твердое тело813"
  other  "Твердое тело814"
  other  "Твердое тело815"
  other  "Твердое тело816"
  other  "Твердое тело817"
  other  "Твердое тело818"
  other  "Твердое тело819"
  other  "Твердое тело820"
  other  "Твердое тело821"
  other  "Твердое тело822"
  other  "Твердое тело823"
  other  "Твердое тело824"
  other  "Твердое тело825"
  other  "Твердое тело826"
  other  "Твердое тело827"
  other  "Твердое тело828"
  other  "Твердое тело829"
  other  "Твердое тело830"
  other  "Твердое тело831"
  other  "Твердое тело832"
  other  "Твердое тело833"
  other  "Твердое тело834"
  other  "Твердое тело835"
  other  "Твердое тело836"
  other  "Твердое тело837"
  other  "Твердое тело838"
  other  "Твердое тело839"
  other  "Твердое тело840"
  other  "Твердое тело841"
  other  "Твердое тело842"
  other  "Твердое тело843"
  other  "Твердое тело844"
  other  "Твердое тело845"
  other  "Твердое тело846"
  other  "Твердое тело847"
  other  "Твердое тело848"
  other  "Твердое тело849"
  other  "Твердое тело850"
  other  "Твердое тело851"
  other  "Твердое тело852"
  other  "Твердое тело853"
  other  "Твердое тело854"
  other  "Твердое тело855"
  other  "Твердое тело856"
  other  "Твердое тело857"
  other  "Твердое тело858"
  other  "Твердое тело859"
  other  "Твердое тело860"
  other  "Твердое тело861"
  other  "Твердое тело862"
  other  "Твердое тело863"
  other  "Твердое тело864"
  other  "Твердое тело865"
  other  "Твердое тело866"
  other  "Твердое тело867"
  other  "Твердое тело868"
  other  "Твердое тело869"
  other  "Твердое тело870"
  other  "Твердое тело871"
  other  "Твердое тело872"
  other  "Твердое тело873"
  other  "Твердое тело874"
  other  "Твердое тело875"
  other  "Твердое тело876"
  other  "Твердое тело877"
  other  "Твердое тело878"
  other  "Твердое тело879"
  other  "Твердое тело880"
  other  "Твердое тело881"
  other  "Твердое тело882"
  other  "Твердое тело883"
  other  "Твердое тело884"
  other  "Твердое тело885"
  other  "Твердое тело886"
  other  "Твердое тело887"
  other  "Твердое тело888"
  other  "Твердое тело889"
  other  "Твердое тело890"
  other  "Твердое тело891"
  other  "Твердое тело892"
  other  "Твердое тело893"
  other  "Твердое тело894"
  other  "Твердое тело895"
  other  "Твердое тело896"
  other  "Твердое тело897"
  other  "Твердое тело898"
  other  "Твердое тело899"
  other  "Твердое тело900"
  other  "Твердое тело901"
  other  "Твердое тело902"
  other  "Твердое тело903"
  other  "Твердое тело904"
  other  "Твердое тело905"
  other  "Твердое тело906"
  other  "Твердое тело907"
  other  "Твердое тело908"
  other  "Твердое тело909"
  other  "Твердое тело910"
  other  "Твердое тело911"
  other  "Твердое тело912"
  other  "Твердое тело913"
  other  "Твердое тело914"
  other  "Твердое тело915"
  other  "Твердое тело916"
  other  "Твердое тело917"
  other  "Твердое тело918"
  other  "Твердое тело919"
  other  "Твердое тело920"
  other  "Твердое тело921"
  other  "Твердое тело922"
  other  "Твердое тело923"
  other  "Твердое тело924"
  other  "Твердое тело925"
  other  "Твердое тело926"
  other  "Твердое тело927"
  other  "Твердое тело928"
  other  "Твердое тело929"
  other  "Твердое тело930"
  other  "Твердое тело931"
  other  "Твердое тело932"
  other  "Твердое тело933"
  other  "Твердое тело934"
  other  "Твердое тело935"
  other  "Твердое тело936"
  other  "Твердое тело937"
  other  "Твердое тело938"
  other  "Твердое тело939"
  other  "Твердое тело940"
  other  "Твердое тело941"
  other  "Твердое тело942"
  other  "Твердое тело943"
  other  "Твердое тело944"
  other  "Твердое тело945"
  other  "Твердое тело946"
  other  "Твердое тело947"
  other  "Твердое тело948"
  other  "Твердое тело949"
  other  "Твердое тело950"
  other  "Твердое тело951"
  other  "Твердое тело952"
  other  "Твердое тело953"
  other  "Твердое тело954"
  other  "Твердое тело955"
  other  "Твердое тело956"
  other  "Твердое тело957"
  other  "Твердое тело958"
  other  "Твердое тело959"
  other  "Твердое тело960"
  other  "Твердое тело961"
  other  "Твердое тело962"
  other  "Твердое тело963"
  other  "Твердое тело964"
  other  "Твердое тело965"
  other  "Твердое тело966"
  other  "Твердое тело967"
  other  "Твердое тело968"
  other  "Твердое тело969"
  other  "Твердое тело970"
  other  "Твердое тело971"
  other  "Твердое тело972"
  other  "Твердое тело973"
  other  "Твердое тело974"
  other  "Твердое тело975"
  other  "Твердое тело976"
  other  "Твердое тело977"
  other  "Твердое тело978"
  other  "Твердое тело979"
  other  "Твердое тело980"
  other  "Твердое тело981"
  other  "Твердое тело982"
  other  "Твердое тело983"
  other  "Твердое тело984"
  other  "Твердое тело985"
  other  "Твердое тело986"
  other  "Твердое тело987"
  other  "Твердое тело988"
  other  "Твердое тело989"
  other  "Твердое тело990"
  other  "Твердое тело991"
  other  "Твердое тело992"
  other  "Твердое тело993"
  other  "Твердое тело994"
  other  "Твердое тело995"
  other  "Твердое тело996"
  other  "Твердое тело997"
  other  "Твердое тело998"
  other  "Твердое тело999"
  other  "Твердое тело1000"
  other  "Твердое тело1001"
  other  "Твердое тело1002"
  other  "Твердое тело1003"
  other  "Твердое тело1004"
  other  "Твердое тело1005"
  other  "Твердое тело1006"
  other  "Твердое тело1007"
  other  "Твердое тело1008"
  other  "Твердое тело1009"
  other  "Твердое тело1010"
  other  "Твердое тело1011"
  other  "Твердое тело1012"
  other  "Твердое тело1013"
  other  "Твердое тело1014"
  other  "Твердое тело1015"
  other  "Твердое тело1016"
  other  "Твердое тело1017"
  other  "Твердое тело1018"
  other  "Твердое тело1019"
  other  "Твердое тело1020"
  other  "Твердое тело1021"
  other  "Твердое тело1022"
  other  "Твердое тело1023"
  other  "Твердое тело1024"
  other  "Твердое тело1025"
  other  "Твердое тело1026"
  other  "Твердое тело1027"
  other  "Твердое тело1028"
  other  "Твердое тело1029"
  other  "Твердое тело1030"
  other  "Твердое тело1031"
  other  "Твердое тело1032"
  other  "Твердое тело1033"
  other  "Твердое тело1034"
  other  "Твердое тело1035"
  other  "Твердое тело1036"
  other  "Твердое тело1037"
  other  "Твердое тело1038"
  other  "Твердое тело1039"
  other  "Твердое тело1040"
  other  "Твердое тело1041"
  other  "Твердое тело1042"
  other  "Твердое тело1043"
  other  "Твердое тело1044"
  other  "Твердое тело1045"
  other  "Твердое тело1046"
  other  "Твердое тело1047"
  other  "Твердое тело1048"
  other  "Твердое тело1049"
  other  "Твердое тело1050"
  other  "Твердое тело1051"
  other  "Твердое тело1052"
  other  "Твердое тело1053"
  other  "Твердое тело1054"
  other  "Твердое тело1055"
  other  "Твердое тело1056"
  other  "Твердое тело1057"
  other  "Твердое тело1058"
  other  "Твердое тело1059"
  other  "Твердое тело1060"
  other  "Твердое тело1061"
  other  "Твердое тело1062"
  other  "Твердое тело1063"
  other  "Твердое тело1064"
  other  "Твердое тело1065"
  other  "Твердое тело1066"
  other  "Твердое тело1067"
  other  "Твердое тело1068"
  other  "Твердое тело1069"
  other  "Твердое тело1070"
  other  "Твердое тело1071"
  other  "Твердое тело1072"
  other  "Твердое тело1073"
  other  "Твердое тело1074"
  other  "Твердое тело1075"
  other  "Твердое тело1076"
  other  "Твердое тело1077"
  other  "Твердое тело1078"
  other  "Твердое тело1079"
  other  "Твердое тело1080"
  other  "Твердое тело1081"
  other  "Твердое тело1082"
  other  "Твердое тело1083"
  other  "Твердое тело1084"
  other  "Твердое тело1085"
  other  "Твердое тело1086"
  other  "Твердое тело1087"
  other  "Твердое тело1088"
  other  "Твердое тело1089"
  other  "Твердое тело1090"
  other  "Твердое тело1091"
  other  "Твердое тело1092"
  other  "Твердое тело1093"
  other  "Твердое тело1094"
  other  "Твердое тело1095"
  other  "Твердое тело1096"
  other  "Твердое тело1097"
  other  "Твердое тело1098"
  other  "Твердое тело1099"
  other  "Твердое тело1100"
  other  "Твердое тело1101"
  other  "Твердое тело1102"
  other  "Твердое тело1103"
  other  "Твердое тело1104"
  other  "Твердое тело1105"
  other  "Твердое тело1106"
  other  "Твердое тело1107"
  other  "Твердое тело1108"
  other  "Твердое тело1109"
  other  "Твердое тело1110"
  other  "Твердое тело1111"
  other  "Твердое тело1112"
  other  "Твердое тело1113"
  other  "Твердое тело1114"
  other  "Твердое тело1115"
  other  "Твердое тело1116"
  other  "Твердое тело1117"
  other  "Твердое тело1118"
  other  "Твердое тело1119"
  other  "Твердое тело1120"
  other  "Твердое тело1121"
  other  "Твердое тело1122"
  other  "Твердое тело1123"
  other  "Твердое тело1124"
  other  "Твердое тело1125"
  other  "Твердое тело1126"
  other  "Твердое тело1127"
  other  "Твердое тело1128"
  other  "Твердое тело1129"
  other  "Твердое тело1130"
  other  "Твердое тело1131"
  other  "Твердое тело1132"
  other  "Твердое тело1133"
  other  "Твердое тело1134"
  other  "Твердое тело1135"
  other  "Твердое тело1136"
  other  "Твердое тело1137"
  other  "Твердое тело1138"
  other  "Твердое тело1139"
  other  "Твердое тело1140"
  other  "Твердое тело1141"
  other  "Твердое тело1142"
  other  "Твердое тело1143"
  other  "Твердое тело1144"
  other  "Твердое тело1145"
  other  "Твердое тело1146"
  other  "Твердое тело1147"
  other  "Твердое тело1148"
  other  "Твердое тело1149"
  other  "Твердое тело1150"
  other  "Твердое тело1151"
  other  "Твердое тело1152"
  other  "Твердое тело1153"
  other  "Твердое тело1154"
  other  "Твердое тело1155"
  other  "Твердое тело1156"
  other  "Твердое тело1157"
  other  "Твердое тело1158"
  other  "Твердое тело1159"
  other  "Твердое тело1160"
  other  "Твердое тело1161"
  other  "Твердое тело1162"
  other  "Твердое тело1163"
  other  "Твердое тело1164"
  other  "Твердое тело1165"
  other  "Твердое тело1166"
  other  "Твердое тело1167"
  other  "Твердое тело1168"
  other  "Твердое тело1169"
  other  "Твердое тело1170"
  other  "Твердое тело1171"
  other  "Твердое тело1172"
  other  "Твердое тело1173"
  other  "Твердое тело1174"
  other  "Твердое тело1175"
  other  "Твердое тело1176"
  other  "Твердое тело1177"
  other  "Твердое тело1178"
  other  "Твердое тело1179"
  other  "Твердое тело1180"
  other  "Твердое тело1181"
  other  "Твердое тело1182"
  other  "Твердое тело1183"
  other  "Твердое тело1184"
  other  "Твердое тело1185"
  other  "Твердое тело1186"
  other  "Твердое тело1187"
  other  "Твердое тело1188"
  other  "Твердое тело1189"
  other  "Твердое тело1190"
  other  "Твердое тело1191"
  other  "Твердое тело1192"
  other  "Твердое тело1193"
  other  "Твердое тело1194"
  other  "Твердое тело1195"
  other  "Твердое тело1196"
  other  "Твердое тело1197"
  other  "Твердое тело1198"
  other  "Твердое тело1199"
  other  "Твердое тело1200"
  other  "Твердое тело1201"
  other  "Твердое тело1202"
  other  "Твердое тело1203"
  other  "Твердое тело1204"
  other  "Твердое тело1205"
  other  "Твердое тело1206"
  other  "Твердое тело1207"
  other  "Твердое тело1208"
  other  "Твердое тело1209"
  other  "Твердое тело1210"
  other  "Твердое тело1211"
  other  "Твердое тело1212"
  other  "Твердое тело1213"
  other  "Твердое тело1214"
  other  "Твердое тело1215"
  other  "Твердое тело1216"
  other  "Твердое тело1217"
  other  "Твердое тело1218"
  other  "Твердое тело1219"
  other  "Твердое тело1220"
  other  "Твердое тело1221"
  other  "Твердое тело1222"
  other  "Твердое тело1223"
  other  "Твердое тело1224"
  other  "Твердое тело1225"
  other  "Твердое тело1226"
  other  "Твердое тело1227"
  other  "Твердое тело1228"
  other  "Твердое тело1229"
  other  "Твердое тело1230"
  other  "Твердое тело1231"
  other  "Твердое тело1232"
  other  "Твердое тело1233"
  other  "Твердое тело1234"
  other  "Твердое тело1235"
  other  "Твердое тело1236"
  other  "Твердое тело1237"
  other  "Твердое тело1238"
  other  "Твердое тело1239"
  other  "Твердое тело1240"
  other  "Твердое тело1241"
  other  "Твердое тело1242"
  other  "Твердое тело1243"
  other  "Твердое тело1244"
  other  "Твердое тело1245"
  other  "Твердое тело1246"
  other  "Твердое тело1247"
  other  "Твердое тело1248"
  other  "Твердое тело1249"
  other  "Твердое тело1250"
  other  "Твердое тело1251"
  other  "Твердое тело1252"
  other  "Твердое тело1253"
  other  "Твердое тело1254"
  other  "Твердое тело1255"
  other  "Твердое тело1256"
  other  "Твердое тело1257"
  other  "Твердое тело1258"
  other  "Твердое тело1259"
  other  "Твердое тело1260"
  other  "Твердое тело1261"
  other  "Твердое тело1262"
  other  "Твердое тело1263"
  other  "Твердое тело1264"
  other  "Твердое тело1265"
  other  "Твердое тело1266"
  other  "Твердое тело1267"
  other  "Твердое тело1268"
  other  "Твердое тело1269"
  other  "Твердое тело1270"
  other  "Твердое тело1271"
  other  "Твердое тело1272"
  other  "Твердое тело1273"
  other  "Твердое тело1274"
  other  "Твердое тело1275"
  other  "Твердое тело1276"
  other  "Твердое тело1277"
  other  "Твердое тело1278"
  other  "Твердое тело1279"
  other  "Твердое тело1280"
  other  "Твердое тело1281"
  other  "Твердое тело1282"
  other  "Твердое тело1283"
  other  "Твердое тело1284"
  other  "Твердое тело1285"
  other  "Твердое тело1286"
  other  "Твердое тело1287"
  other  "Твердое тело1288"
  other  "Твердое тело1289"
  other  "Твердое тело1290"
  other  "Твердое тело1291"
  other  "Твердое тело1292"
  other  "Твердое тело1293"
  other  "Твердое тело1294"
  other  "Твердое тело1295"
  other  "Твердое тело1296"
  other  "Твердое тело1297"
  other  "Твердое тело1298"
  other  "Твердое тело1299"
  other  "Твердое тело1300"
  other  "Твердое тело1301"
  other  "Твердое тело1302"
  other  "Твердое тело1303"
  other  "Твердое тело1304"
  other  "Твердое тело1305"
  other  "Твердое тело1306"
  other  "Твердое тело1307"
  other  "Твердое тело1308"
  other  "Твердое тело1309"
  other  "Твердое тело1310"
  other  "Твердое тело1311"
  other  "Твердое тело1312"
  other  "Твердое тело1313"
  other  "Твердое тело1314"
  other  "Твердое тело1315"
  other  "Твердое тело1316"
  other  "Твердое тело1317"
  other  "Твердое тело1318"
  other  "Твердое тело1319"
  other  "Твердое тело1320"
  other  "Твердое тело1321"
  other  "Твердое тело1322"
  other  "Твердое тело1323"
  other  "Твердое тело1324"
  other  "Твердое тело1325"
  other  "Твердое тело1326"
  other  "Твердое тело1327"
  other  "Твердое тело1328"
  other  "Твердое тело1329"
  other  "Твердое тело1330"
  other  "Твердое тело1331"
  other  "Твердое тело1332"
  other  "Твердое тело1333"
  other  "Твердое тело1334"
  other  "Твердое тело1335"
  other  "Твердое тело1336"
  other  "Твердое тело1337"
  other  "Твердое тело1338"
  other  "Твердое тело1339"
  other  "Твердое тело1340"
  other  "Твердое тело1341"
  other  "Твердое тело1342"
  other  "Твердое тело1343"
  other  "Твердое тело1344"
  other  "Твердое тело1345"
  other  "Твердое тело1346"
  other  "Твердое тело1347"
  other  "Твердое тело1348"
  other  "Твердое тело1349"
  other  "Твердое тело1350"
  other  "Твердое тело1351"
  other  "Твердое тело1352"
  other  "Твердое тело1353"
  other  "Твердое тело1354"
  other  "Твердое тело1355"
  other  "Твердое тело1356"
  other  "Твердое тело1357"
  other  "Твердое тело1358"
  other  "Твердое тело1359"
  other  "Твердое тело1360"
  other  "Твердое тело1361"
  other  "Твердое тело1362"
  other  "Твердое тело1363"
  other  "Твердое тело1364"
  other  "Твердое тело1365"
  other  "Твердое тело1366"
  other  "Твердое тело1367"
  other  "Твердое тело1368"
  other  "Твердое тело1369"
  other  "Твердое тело1370"
  other  "Твердое тело1371"
  other  "Твердое тело1372"
  other  "Твердое тело1373"
  other  "Твердое тело1374"
  other  "Твердое тело1375"
  other  "Твердое тело1376"
  other  "Твердое тело1377"
  other  "Твердое тело1378"
  other  "Твердое тело1379"
  other  "Твердое тело1380"
  other  "Твердое тело1381"
  other  "Твердое тело1382"
  other  "Твердое тело1383"
  other  "Твердое тело1384"
  other  "Твердое тело1385"
  other  "Твердое тело1386"
  other  "Твердое тело1387"
  other  "Твердое тело1388"
  other  "Твердое тело1389"
  other  "Твердое тело1390"
  other  "Твердое тело1391"
  other  "Твердое тело1392"
  other  "Твердое тело1393"
  other  "Твердое тело1394"
  other  "Твердое тело1395"
  other  "Твердое тело1396"
  other  "Твердое тело1397"
  other  "Твердое тело1398"
  other  "Твердое тело1399"
  other  "Твердое тело1400"
  other  "Твердое тело1401"
  other  "Твердое тело1402"
  other  "Твердое тело1403"
  other  "Твердое тело1404"
  other  "Твердое тело1405"
  other  "Твердое тело1406"
  other  "Твердое тело1407"
  other  "Твердое тело1408"
  other  "Твердое тело1409"
  other  "Твердое тело1410"
  other  "Твердое тело1411"
  other  "Твердое тело1412"
  other  "Твердое тело1413"
  other  "Твердое тело1414"
  other  "Твердое тело1415"
  other  "Твердое тело1416"
  other  "Твердое тело1417"
  other  "Твердое тело1418"
  other  "Твердое тело1419"
  other  "Твердое тело1420"
  other  "Твердое тело1421"
  other  "Твердое тело1422"
  other  "Твердое тело1423"
  other  "Твердое тело1424"
  other  "Твердое тело1425"
  other  "Твердое тело1426"
  other  "Твердое тело1427"
  other  "Твердое тело1428"
  other  "Твердое тело1429"
  other  "Твердое тело1430"
  other  "Твердое тело1431"
  other  "Твердое тело1432"
  other  "Твердое тело1433"
  other  "Твердое тело1434"
  other  "Твердое тело1435"
  other  "Твердое тело1436"
  other  "Твердое тело1437"
  other  "Твердое тело1438"
  other  "Твердое тело1439"
  other  "Твердое тело1440"
  other  "Твердое тело1441"
  other  "Твердое тело1442"
  other  "Твердое тело1443"
  other  "Твердое тело1444"
  other  "Твердое тело1445"
  other  "Твердое тело1446"
  other  "Твердое тело1447"
  other  "Твердое тело1448"
  other  "Твердое тело1449"
  other  "Твердое тело1450"
  other  "Твердое тело1451"
  other  "Твердое тело1452"
  other  "Твердое тело1453"
  other  "Твердое тело1454"
  other  "Твердое тело1455"
  other  "Твердое тело1456"
  other  "Твердое тело1457"
  other  "Твердое тело1458"
  other  "Твердое тело1459"
  other  "Твердое тело1460"
  other  "Твердое тело1461"
  other  "Твердое тело1462"
  other  "Твердое тело1463"
  other  "Твердое тело1464"
  other  "Твердое тело1465"
  other  "Твердое тело1466"
  other  "Твердое тело1467"
  other  "Твердое тело1468"
  other  "Твердое тело1469"
  other  "Твердое тело1470"
  other  "Твердое тело1471"
  other  "Твердое тело1472"
  other  "Твердое тело1473"
  other  "Твердое тело1474"
  other  "Твердое тело1475"
  other  "Твердое тело1476"
  other  "Твердое тело1477"
  other  "Твердое тело1478"
  other  "Твердое тело1479"
  other  "Твердое тело1480"
  other  "Твердое тело1481"
  other  "Твердое тело1482"
  other  "Твердое тело1483"
  other  "Твердое тело1484"
  other  "Твердое тело1485"
  other  "Твердое тело1486"
  other  "Твердое тело1487"
  other  "Твердое тело1488"
  other  "Твердое тело1489"
  other  "Твердое тело1490"
  other  "Твердое тело1491"
  other  "Твердое тело1492"
  other  "Твердое тело1493"
  other  "Твердое тело1494"
  other  "Твердое тело1495"
  other  "Твердое тело1496"
  other  "Твердое тело1497"
  other  "Твердое тело1498"
  other  "Твердое тело1499"
  other  "Твердое тело1500"
  other  "Твердое тело1501"
  other  "Твердое тело1502"
  other  "Твердое тело1503"
  other  "Твердое тело1504"
  other  "Твердое тело1505"
  other  "Твердое тело1506"
  other  "Твердое тело1507"
  other  "Твердое тело1508"
  other  "Твердое тело1509"
  other  "Твердое тело1510"
  other  "Твердое тело1511"
  other  "Твердое тело1512"
  other  "Твердое тело1513"
  other  "Твердое тело1514"
  other  "Твердое тело1515"
  other  "Твердое тело1516"
  other  "Твердое тело1517"
  other  "Твердое тело1518"
  other  "Твердое тело1519"
  other  "Твердое тело1520"
  other  "Твердое тело1521"
  other  "Твердое тело1522"
  other  "Твердое тело1523"
  other  "Твердое тело1524"
  other  "Твердое тело1525"
  other  "Твердое тело1526"
  other  "Твердое тело1527"
  other  "Твердое тело1528"
  other  "Твердое тело1529"
  other  "Твердое тело1530"
  other  "Твердое тело1531"
  other  "Твердое тело1532"
  other  "Твердое тело1533"
  other  "Твердое тело1534"
  other  "Твердое тело1535"
  other  "Твердое тело1536"
  other  "Твердое тело1537"
  other  "Твердое тело1538"
  other  "Твердое тело1539"
  other  "Твердое тело1540"
  other  "Твердое тело1541"
  other  "Твердое тело1542"
  other  "Твердое тело1543"
  other  "Твердое тело1544"
  other  "Твердое тело1545"
  other  "Твердое тело1546"
  other  "Твердое тело1547"
  other  "Твердое тело1548"
  other  "Твердое тело1549"
  other  "Твердое тело1550"
  other  "Твердое тело1551"
  other  "Твердое тело1552"
  other  "Твердое тело1553"
  other  "Твердое тело1554"
  other  "Твердое тело1555"
  other  "Твердое тело1556"
  other  "Твердое тело1557"
  other  "Твердое тело1558"
  other  "Твердое тело1559"
  other  "Твердое тело1560"
  other  "Твердое тело1561"
  other  "Твердое тело1562"
  other  "Твердое тело1563"
  other  "Твердое тело1564"
  other  "Твердое тело1565"
  other  "Твердое тело1566"
  other  "Твердое тело1567"
  other  "Твердое тело1568"
  other  "Твердое тело1569"
  other  "Твердое тело1570"
  other  "Твердое тело1571"
  other  "Твердое тело1572"
  other  "Твердое тело1573"
  other  "Твердое тело1574"
  other  "Твердое тело1575"
  other  "Твердое тело1576"
  other  "Твердое тело1577"
  other  "Твердое тело1578"
  other  "Твердое тело1579"
  other  "Твердое тело1580"
  other  "Твердое тело1581"
  other  "Твердое тело1582"
  other  "Твердое тело1583"
  other  "Твердое тело1584"
  other  "Твердое тело1585"
  other  "Твердое тело1586"
  other  "Твердое тело1587"
  other  "Твердое тело1588"
  other  "Твердое тело1589"
  other  "Твердое тело1590"
  other  "Твердое тело1591"
  other  "Твердое тело1592"
  other  "Твердое тело1593"
  other  "Твердое тело1594"
  other  "Твердое тело1595"
  other  "Твердое тело1596"
  other  "Твердое тело1597"
  other  "Твердое тело1598"
  other  "Твердое тело1599"
  other  "Твердое тело1600"
  other  "Твердое тело1601"
  other  "Твердое тело1602"
  other  "Твердое тело1603"
  other  "Твердое тело1604"
  other  "Твердое тело1605"
  other  "Твердое тело1606"
  other  "Твердое тело1607"
  other  "Твердое тело1608"
  other  "Твердое тело1609"
  other  "Твердое тело1610"
  other  "Твердое тело1611"
  other  "Твердое тело1612"
  other  "Твердое тело1613"
  other  "Твердое тело1614"
  other  "Твердое тело1615"
  other  "Твердое тело1616"
  other  "Твердое тело1617"
  other  "Твердое тело1618"
  other  "Твердое тело1619"
  other  "Твердое тело1620"
  other  "Твердое тело1621"
  other  "Твердое тело1622"
  other  "Твердое тело1623"
  other  "Твердое тело1624"
  other  "Твердое тело1625"
  other  "Твердое тело1626"
  other  "Твердое тело1627"
  other  "Твердое тело1628"
  other  "Твердое тело1629"
  other  "Твердое тело1630"
  other  "Твердое тело1631"
  other  "Твердое тело1632"
  other  "Твердое тело1633"
  other  "Твердое тело1634"
  other  "Твердое тело1635"
  other  "Твердое тело1636"
  other  "Твердое тело1637"
  other  "Твердое тело1638"
  other  "Твердое тело1639"
  other  "Твердое тело1640"
  other  "Твердое тело1641"
  other  "Твердое тело1642"
  other  "Твердое тело1643"
  other  "Твердое тело1644"
  other  "Твердое тело1645"
  other  "Твердое тело1646"
  other  "Твердое тело1647"
  other  "Твердое тело1648"
  other  "Твердое тело1649"
  other  "Твердое тело1650"
  other  "Твердое тело1651"
  other  "Твердое тело1652"
  other  "Твердое тело1653"
  other  "Твердое тело1654"
  other  "Твердое тело1655"
  other  "Твердое тело1656"
  other  "Твердое тело1657"
  other  "Твердое тело1658"
  other  "Твердое тело1659"
  other  "Твердое тело1660"
  other  "Твердое тело1661"
  other  "Твердое тело1662"
  other  "Твердое тело1663"
  other  "Твердое тело1664"
  other  "Твердое тело1665"
  other  "Твердое тело1666"
  other  "Твердое тело1667"
  other  "Твердое тело1668"
  other  "Твердое тело1669"
  other  "Твердое тело1670"
  other  "Твердое тело1671"
  other  "Твердое тело1672"
  other  "Твердое тело1673"
  other  "Твердое тело1674"
  other  "Твердое тело1675"
  other  "Твердое тело1676"
  other  "Твердое тело1677"
  other  "Твердое тело1678"
  other  "Твердое тело1679"
  other  "Твердое тело1680"
  other  "Твердое тело1681"
  other  "Твердое тело1682"
  other  "Твердое тело1683"
  other  "Твердое тело1684"
  other  "Твердое тело1685"
  other  "Твердое тело1686"
  other  "Твердое тело1687"
  other  "Твердое тело1688"
  other  "Твердое тело1689"
  other  "Твердое тело1690"
  other  "Твердое тело1691"
  other  "Твердое тело1692"
  other  "Твердое тело1693"
  other  "Твердое тело1694"
  other  "Твердое тело1695"
  other  "Твердое тело1696"
  other  "Твердое тело1697"
  other  "Твердое тело1698"
  other  "Твердое тело1699"
  other  "Твердое тело1700"
  other  "Твердое тело1701"
  other  "Твердое тело1702"
  other  "Твердое тело1703"
  other  "Твердое тело1704"
  other  "Твердое тело1705"
  other  "Твердое тело1706"
  other  "Твердое тело1707"
  other  "Твердое тело1708"
  other  "Твердое тело1709"
  other  "Твердое тело1710"
  other  "Твердое тело1711"
  other  "Твердое тело1712"
  other  "Твердое тело1713"
  other  "Твердое тело1714"
  other  "Твердое тело1715"
  other  "Твердое тело1716"
  other  "Твердое тело1717"
  other  "Твердое тело1718"
  other  "Твердое тело1719"
  other  "Твердое тело1720"
  other  "Твердое тело1721"
  other  "Твердое тело1722"
  other  "Твердое тело1723"
  other  "Твердое тело1724"
  other  "Твердое тело1725"
  other  "Твердое тело1726"
  other  "Твердое тело1727"
  other  "Твердое тело1728"
  other  "Твердое тело1729"
  other  "Твердое тело1730"
  other  "Твердое тело1731"
  other  "Твердое тело1732"
  other  "Твердое тело1733"
  other  "Твердое тело1734"
  other  "Твердое тело1735"
  other  "Твердое тело1736"
  other  "Твердое тело1737"
  other  "Твердое тело1738"
  other  "Твердое тело1739"
  other  "Твердое тело1740"
  other  "Твердое тело1741"
  other  "Твердое тело1742"
  other  "Твердое тело1743"
  other  "Твердое тело1744"
  other  "Твердое тело1745"
  other  "Твердое тело1746"
  other  "Твердое тело1747"
  other  "Твердое тело1748"
  other  "Твердое тело1749"
  other  "Твердое тело1750"
  other  "Твердое тело1751"
  other  "Твердое тело1752"
  other  "Твердое тело1753"
  other  "Твердое тело1754"
  other  "Твердое тело1755"
  other  "Твердое тело1756"
  other  "Твердое тело1757"
  other  "Твердое тело1758"
  other  "Твердое тело1759"
  other  "Твердое тело1760"
  other  "Твердое тело1761"
  other  "Твердое тело1762"
  other  "Твердое тело1763"
  other  "Твердое тело1764"
  other  "Твердое тело1765"
  other  "Твердое тело1766"
  other  "Твердое тело1767"
  other  "Твердое тело1768"
  other  "Твердое тело1769"
  other  "Твердое тело1770"
  other  "Твердое тело1771"
  other  "Твердое тело1772"
  other  "Твердое тело1773"
  other  "Твердое тело1774"
  other  "Твердое тело1775"
  other  "Твердое тело1776"
  other  "Твердое тело1777"
  other  "Твердое тело1778"
  other  "Твердое тело1779"
  other  "Твердое тело1780"
  other  "Твердое тело1781"
  other  "Твердое тело1782"
  other  "Твердое тело1783"
  other  "Твердое тело1784"
  other  "Твердое тело1785"
  other  "Твердое тело1786"
  other  "Твердое тело1787"
  other  "Твердое тело1788"
  other  "Твердое тело1789"
  other  "Твердое тело1790"
  other  "Твердое тело1791"
  other  "Твердое тело1792"
  other  "Твердое тело1793"
  other  "Твердое тело1794"
  other  "Твердое тело1795"
  other  "Твердое тело1796"
  other  "Твердое тело1797"
  other  "Твердое тело1798"
  other  "Твердое тело1799"
  other  "Твердое тело1800"
  other  "Твердое тело1801"
  other  "Твердое тело1802"
  other  "Твердое тело1803"
  other  "Твердое тело1804"
  other  "Твердое тело1805"
  other  "Твердое тело1806"
  other  "Твердое тело1807"
  other  "Твердое тело1808"
  other  "Твердое тело1809"
  other  "Твердое тело1810"
  other  "Твердое тело1811"
  other  "Твердое тело1812"
  other  "Твердое тело1813"
  other  "Твердое тело1814"
  sketch  "3D эскиз2448"
  other  "Open CASCADE STEP translator 7.5 5.1.1_5577:1"
  other  "User Library-User Library-res0402_res0402_body_5579:1"
  other  "User Library-User Library-res0402_res0402_body_5581:1"
  other  "User Library-User Library-res0402_res0402_body_5583:1"
  other  "User Library-DF40C-100DP-0_4V(51)_5588:1"
  other  "User Library-DF40C-100DP-0_4V(51)_5589:1"
  other  "200-ball_VFBGAold.step_5590:1"
  other  "200-ball_VFBGAold.step_5590:2"
  other  "200-ball_VFBGAold.step_5590:3"
  other  "200-ball_VFBGAold.step_5590:4"
  other  "200-ball_VFBGAold.step_5590:5"
  other  "200-ball_VFBGAold.step_5590:6"
  other  "200-ball_VFBGAold.step_5590:7"
  other  "200-ball_VFBGAold.step_5590:8"
  other  "200-ball_VFBGAold.step_5590:9"
  other  "200-ball_VFBGAold.step_5590:10"
  other  "200-ball_VFBGAold.step_5590:11"
  other  "200-ball_VFBGAold.step_5590:12"
  other  "200-ball_VFBGAold.step_5590:13"
  other  "200-ball_VFBGAold.step_5590:14"
  other  "200-ball_VFBGAold.step_5590:15"
  other  "200-ball_VFBGAold.step_5590:16"
  other  "200-ball_VFBGAold.step_5590:17"
  other  "200-ball_VFBGAold.step_5590:18"
  other  "200-ball_VFBGAold.step_5590:19"
  other  "200-ball_VFBGAold.step_5590:20"
  other  "200-ball_VFBGAold.step_5590:21"
  other  "200-ball_VFBGAold.step_5590:22"
  other  "200-ball_VFBGAold.step_5590:23"
  other  "200-ball_VFBGAold.step_5590:24"
  other  "200-ball_VFBGAold.step_5590:25"
  other  "200-ball_VFBGAold.step_5590:26"
  other  "200-ball_VFBGAold.step_5590:27"
  other  "200-ball_VFBGAold.step_5590:28"
  other  "200-ball_VFBGAold.step_5590:29"
  other  "200-ball_VFBGAold.step_5590:30"
  other  "200-ball_VFBGAold.step_5590:31"
  other  "200-ball_VFBGAold.step_5590:32"
  other  "200-ball_VFBGAold.step_5590:33"
  other  "200-ball_VFBGAold.step_5590:34"
  other  "200-ball_VFBGAold.step_5590:35"
  other  "200-ball_VFBGAold.step_5590:36"
  other  "200-ball_VFBGAold.step_5590:37"
  other  "200-ball_VFBGAold.step_5590:38"
  other  "200-ball_VFBGAold.step_5590:39"
  other  "200-ball_VFBGAold.step_5590:40"
  other  "200-ball_VFBGAold.step_5590:41"
  other  "200-ball_VFBGAold.step_5590:42"
  other  "200-ball_VFBGAold.step_5590:43"
  other  "200-ball_VFBGAold.step_5590:44"
  other  "200-ball_VFBGAold.step_5590:45"
  other  "200-ball_VFBGAold.step_5590:46"
  other  "200-ball_VFBGAold.step_5590:47"
  other  "200-ball_VFBGAold.step_5590:48"
  other  "200-ball_VFBGAold.step_5590:49"
  other  "200-ball_VFBGAold.step_5590:50"
  other  "200-ball_VFBGAold.step_5590:51"
  other  "200-ball_VFBGAold.step_5590:52"
  other  "200-ball_VFBGAold.step_5590:53"
  other  "200-ball_VFBGAold.step_5590:54"
  other  "200-ball_VFBGAold.step_5590:55"
  other  "200-ball_VFBGAold.step_5590:56"
  other  "200-ball_VFBGAold.step_5590:57"
  other  "200-ball_VFBGAold.step_5590:58"
  other  "200-ball_VFBGAold.step_5590:59"
  other  "200-ball_VFBGAold.step_5590:60"
  other  "200-ball_VFBGAold.step_5590:61"
  other  "200-ball_VFBGAold.step_5590:62"
  other  "200-ball_VFBGAold.step_5590:63"
  other  "200-ball_VFBGAold.step_5590:64"
  other  "200-ball_VFBGAold.step_5590:65"
  other  "200-ball_VFBGAold.step_5590:66"
  other  "200-ball_VFBGAold.step_5590:67"
  other  "200-ball_VFBGAold.step_5590:68"
  other  "200-ball_VFBGAold.step_5590:69"
  other  "200-ball_VFBGAold.step_5590:70"
  other  "200-ball_VFBGAold.step_5590:71"
  other  "200-ball_VFBGAold.step_5590:72"
  other  "200-ball_VFBGAold.step_5590:73"
  other  "200-ball_VFBGAold.step_5590:74"
  other  "200-ball_VFBGAold.step_5590:75"
  other  "200-ball_VFBGAold.step_5590:76"
  other  "200-ball_VFBGAold.step_5590:77"
  other  "200-ball_VFBGAold.step_5590:78"
  other  "200-ball_VFBGAold.step_5590:79"
  other  "200-ball_VFBGAold.step_5590:80"
  other  "200-ball_VFBGAold.step_5590:81"
  other  "200-ball_VFBGAold.step_5590:82"
  other  "200-ball_VFBGAold.step_5590:83"
  other  "200-ball_VFBGAold.step_5590:84"
  other  "200-ball_VFBGAold.step_5590:85"
  other  "200-ball_VFBGAold.step_5590:86"
  other  "200-ball_VFBGAold.step_5590:87"
  other  "200-ball_VFBGAold.step_5590:88"
  other  "200-ball_VFBGAold.step_5590:89"
  other  "200-ball_VFBGAold.step_5590:90"
  other  "200-ball_VFBGAold.step_5590:91"
  other  "200-ball_VFBGAold.step_5590:92"
  other  "200-ball_VFBGAold.step_5590:93"
  other  "200-ball_VFBGAold.step_5590:94"
  other  "200-ball_VFBGAold.step_5590:95"
  other  "200-ball_VFBGAold.step_5590:96"
  other  "200-ball_VFBGAold.step_5590:97"
  other  "200-ball_VFBGAold.step_5590:98"
  other  "200-ball_VFBGAold.step_5590:99"
  other  "200-ball_VFBGAold.step_5590:100"
  other  "200-ball_VFBGAold.step_5590:101"
  other  "200-ball_VFBGAold.step_5590:102"
  other  "200-ball_VFBGAold.step_5590:103"
  other  "200-ball_VFBGAold.step_5590:104"
  other  "200-ball_VFBGAold.step_5590:105"
  other  "200-ball_VFBGAold.step_5590:106"
  other  "200-ball_VFBGAold.step_5590:107"
  other  "200-ball_VFBGAold.step_5590:108"
  other  "200-ball_VFBGAold.step_5590:109"
  other  "200-ball_VFBGAold.step_5590:110"
  other  "200-ball_VFBGAold.step_5590:111"
  other  "200-ball_VFBGAold.step_5590:112"
  other  "200-ball_VFBGAold.step_5590:113"
  other  "200-ball_VFBGAold.step_5590:114"
  other  "200-ball_VFBGAold.step_5590:115"
  other  "200-ball_VFBGAold.step_5590:116"
  other  "200-ball_VFBGAold.step_5590:117"
  other  "200-ball_VFBGAold.step_5590:118"
  other  "200-ball_VFBGAold.step_5590:119"
  other  "200-ball_VFBGAold.step_5590:120"
  other  "200-ball_VFBGAold.step_5590:121"
  other  "200-ball_VFBGAold.step_5590:122"
  other  "200-ball_VFBGAold.step_5590:123"
  other  "200-ball_VFBGAold.step_5590:124"
  other  "200-ball_VFBGAold.step_5590:125"
  other  "200-ball_VFBGAold.step_5590:126"
  other  "200-ball_VFBGAold.step_5590:127"
  other  "200-ball_VFBGAold.step_5590:128"
  other  "200-ball_VFBGAold.step_5590:129"
  other  "200-ball_VFBGAold.step_5590:130"
  other  "200-ball_VFBGAold.step_5590:131"
  other  "200-ball_VFBGAold.step_5590:132"
  other  "200-ball_VFBGAold.step_5590:133"
  other  "200-ball_VFBGAold.step_5590:134"
  other  "200-ball_VFBGAold.step_5590:135"
  other  "200-ball_VFBGAold.step_5590:136"
  other  "200-ball_VFBGAold.step_5590:137"
  other  "200-ball_VFBGAold.step_5590:138"
  other  "200-ball_VFBGAold.step_5590:139"
  other  "200-ball_VFBGAold.step_5590:140"
  other  "200-ball_VFBGAold.step_5590:141"
  other  "200-ball_VFBGAold.step_5590:142"
  other  "200-ball_VFBGAold.step_5590:143"
  other  "200-ball_VFBGAold.step_5590:144"
  other  "200-ball_VFBGAold.step_5590:145"
  other  "200-ball_VFBGAold.step_5590:146"
  other  "200-ball_VFBGAold.step_5590:147"
  other  "200-ball_VFBGAold.step_5590:148"
  other  "200-ball_VFBGAold.step_5590:149"
  other  "200-ball_VFBGAold.step_5590:150"
  other  "200-ball_VFBGAold.step_5590:151"
  other  "200-ball_VFBGAold.step_5590:152"
  other  "200-ball_VFBGAold.step_5590:153"
  other  "200-ball_VFBGAold.step_5590:154"
  other  "200-ball_VFBGAold.step_5590:155"
  other  "200-ball_VFBGAold.step_5590:156"
  other  "200-ball_VFBGAold.step_5590:157"
  other  "200-ball_VFBGAold.step_5590:158"
  other  "200-ball_VFBGAold.step_5590:159"
  other  "200-ball_VFBGAold.step_5590:160"
  other  "200-ball_VFBGAold.step_5590:161"
  other  "200-ball_VFBGAold.step_5590:162"
  other  "200-ball_VFBGAold.step_5590:163"
  other  "200-ball_VFBGAold.step_5590:164"
  other  "200-ball_VFBGAold.step_5590:165"
  other  "200-ball_VFBGAold.step_5590:166"
  other  "200-ball_VFBGAold.step_5590:167"
  other  "200-ball_VFBGAold.step_5590:168"
  other  "200-ball_VFBGAold.step_5590:169"
  other  "200-ball_VFBGAold.step_5590:170"
  other  "200-ball_VFBGAold.step_5590:171"
  other  "200-ball_VFBGAold.step_5590:172"
  other  "200-ball_VFBGAold.step_5590:173"
  other  "200-ball_VFBGAold.step_5590:174"
  other  "200-ball_VFBGAold.step_5590:175"
  other  "200-ball_VFBGAold.step_5590:176"
  other  "200-ball_VFBGAold.step_5590:177"
  other  "200-ball_VFBGAold.step_5590:178"
  other  "200-ball_VFBGAold.step_5590:179"
  other  "200-ball_VFBGAold.step_5590:180"
  other  "200-ball_VFBGAold.step_5590:181"
  other  "200-ball_VFBGAold.step_5590:182"
  other  "200-ball_VFBGAold.step_5590:183"
  other  "200-ball_VFBGAold.step_5590:184"
  other  "200-ball_VFBGAold.step_5590:185"
  other  "200-ball_VFBGAold.step_5590:186"
  other  "200-ball_VFBGAold.step_5590:187"
  other  "200-ball_VFBGAold.step_5590:188"
  other  "200-ball_VFBGAold.step_5590:189"
  other  "200-ball_VFBGAold.step_5590:190"
  other  "200-ball_VFBGAold.step_5590:191"
  other  "200-ball_VFBGAold.step_5590:192"
  other  "200-ball_VFBGAold.step_5590:193"
  other  "200-ball_VFBGAold.step_5590:194"
  other  "200-ball_VFBGAold.step_5590:195"
  other  "200-ball_VFBGAold.step_5590:196"
  other  "200-ball_VFBGAold.step_5590:197"
  other  "200-ball_VFBGAold.step_5590:198"
  other  "200-ball_VFBGAold.step_5590:199"
  other  "200-ball_VFBGAold.step_5590:200"
  other  "200-ball_VFBGAold.step_5590:201"
  other  "CAP0201.step_5592:1"
  other  "CAP0201.step_5594:1"
  other  "CAP0201.step_5596:1"
  other  "CAP0201.step_5598:1"
  other  "CAP0201.step_5600:1"
  other  "CAP0201.step_5602:1"
  other  "CAP0201.step_5604:1"
  other  "CAP0201.step_5606:1"
  other  "CAP0201.step_5608:1"
  other  "CAP0201.step_5610:1"
  other  "CAP0201.step_5612:1"
  other  "CAP0201.step_5614:1"
  other  "CAP0201.step_5616:1"
  other  "CAP0201.step_5618:1"
  other  "CAP0201.step_5620:1"
  other  "CAP0201.step_5622:1"
  other  "CAP0201.step_5624:1"
  other  "CAP0201.step_5626:1"
  other  "CAP0201.step_5628:1"
  other  "CAP0201.step_5630:1"
  other  "CAP0201.step_5632:1"
  other  "CAP0201.step_5634:1"
  other  "CAP0201.step_5636:1"
  other  "CAP0201.step_5638:1"
  other  "CAP0201.step_5640:1"
  other  "CAP0201.step_5642:1"
  other  "CAP0201.step_5644:1"
  other  "CAP0201.step_5646:1"
  other  "CAP0201.step_5648:1"
  other  "CAP0201.step_5650:1"
  other  "CAP0201.step_5652:1"
  other  "CAP0201.step_5654:1"
  other  "CAP0201.step_5656:1"
  other  "RES0201old.step_5658:1"
  other  "RES0201old.step_5658:2"
  other  "RES0201old.step_5660:1"
  other  "RES0201old.step_5660:2"
  other  "RES0201old.step_5662:1"
  other  "RES0201old.step_5662:2"
  other  "RES0201old.step_5664:1"
  other  "RES0201old.step_5664:2"
  other  "RES0201old.step_5666:1"
  other  "RES0201old.step_5666:2"
  other  "RES0201old.step_5668:1"
  other  "RES0201old.step_5668:2"
  other  "RES0201old.step_5670:1"
  other  "RES0201old.step_5670:2"
  other  "RES0201old.step_5672:1"
  other  "RES0201old.step_5672:2"
  other  "RES0201old.step_5674:1"
  other  "RES0201old.step_5674:2"
  other  "RES0201old.step_5676:1"
  other  "RES0201old.step_5676:2"
  other  "RES0201old.step_5678:1"
  other  "RES0201old.step_5678:2"
  other  "RES0201old.step_5680:1"
  other  "RES0201old.step_5680:2"
  other  "RES0201old.step_5682:1"
  other  "RES0201old.step_5682:2"
  other  "RES0201old.step_5684:1"
  other  "RES0201old.step_5684:2"
  other  "CAP0402.step_5686:1"
  other  "CAP0402.step_5688:1"
  other  "CAP0402.step_5690:1"
  other  "CAP0402.step_5692:1"
  other  "CAP0402.step_5694:1"
  other  "CAP0402.step_5696:1"
  other  "CAP0402.step_5698:1"
  other  "CAP0402.step_5700:1"
  other  "CAP0402.step_5702:1"
  other  "CAP0402.step_5704:1"
  other  "CAP0402.step_5706:1"
  other  "CAP0402.step_5708:1"
  other  "CAP0402.step_5710:1"
  other  "CAP0402.step_5712:1"
  other  "CAP0402.step_5714:1"
  other  "CAP0402.step_5716:1"
  other  "CAP0402.step_5718:1"
  other  "CAP0402.step_5720:1"
  other  "CAP0402.step_5722:1"
  other  "CAP0402.step_5724:1"
  other  "CAP0402.step_5726:1"
  other  "CAP0402.step_5728:1"
  other  "PMIC STEP.STEP_5730:1"
  other  "3D-SRP201208-R47MH-20230512 .step_5732:1"
  other  "3D-SRP201208-R47MH-20230512 .step_5732:2"
  other  "3D-SRP201208-R47MH-20230512 .step_5732:3"
  other  "3D-SRP201208-R47MH-20230512 .step_5734:1"
  other  "3D-SRP201208-R47MH-20230512 .step_5734:2"
  other  "3D-SRP201208-R47MH-20230512 .step_5734:3"
  other  "3D-SRP201208-R47MH-20230512 .step_5736:1"
  other  "3D-SRP201208-R47MH-20230512 .step_5736:2"
  other  "3D-SRP201208-R47MH-20230512 .step_5736:3"
  other  "3D-SRP201208-R47MH-20230512 .step_5738:1"
  other  "3D-SRP201208-R47MH-20230512 .step_5738:2"
  other  "3D-SRP201208-R47MH-20230512 .step_5738:3"
  other  "3D-SRP201208-R47MH-20230512 .step_5740:1"
  other  "3D-SRP201208-R47MH-20230512 .step_5740:2"
  other  "3D-SRP201208-R47MH-20230512 .step_5740:3"
  other  "3D-SRP201208-R47MH-20230512 .step_5742:1"
  other  "3D-SRP201208-R47MH-20230512 .step_5742:2"
  other  "3D-SRP201208-R47MH-20230512 .step_5742:3"
  other  "3D-SRP201208-R47MH-20230512 .step_5744:1"
  other  "3D-SRP201208-R47MH-20230512 .step_5744:2"
  other  "3D-SRP201208-R47MH-20230512 .step_5744:3"
  other  "body_5746:1"
  other  "term2_5747:1"
  other  "term1_5748:1"
  other  "body_5746:2"
  other  "term2_5747:2"
  other  "term1_5748:2"
  other  "body_5746:3"
  other  "term2_5747:3"
  other  "term1_5748:3"
  other  "body_5746:4"
  other  "term2_5747:4"
  other  "term1_5748:4"
  other  "2712 v2 STEP.STEP_5758:1"
  other  "2712 v2 STEP.STEP_5758:2"
  other  "2712 v2 STEP.STEP_5758:3"
  other  "CAP0603.step_5760:1"
  other  "CAP0603.step_5762:1"
  other  "CAP0603.step_5764:1"
  other  "CAP0603.step_5766:1"
  other  "RES0402.step_5768:1"
  other  "RES0402.step_5768:2"
  other  "RES0402.step_5768:3"
  other  "RES0402.step_5768:4"
  other  "RES0402.step_5770:1"
  other  "RES0402.step_5770:2"
  other  "RES0402.step_5770:3"
  other  "RES0402.step_5770:4"
  other  "RES0402.step_5772:1"
  other  "RES0402.step_5772:2"
  other  "RES0402.step_5772:3"
  other  "RES0402.step_5772:4"
  other  "RES0402.step_5774:1"
  other  "RES0402.step_5774:2"
  other  "RES0402.step_5774:3"
  other  "RES0402.step_5774:4"
  other  "RES0402.step_5776:1"
  other  "RES0402.step_5776:2"
  other  "RES0402.step_5776:3"
  other  "RES0402.step_5776:4"
  other  "RES0402.step_5778:1"
  other  "RES0402.step_5778:2"
  other  "RES0402.step_5778:3"
  other  "RES0402.step_5778:4"
  other  "RES0402.step_5780:1"
  other  "RES0402.step_5780:2"
  other  "RES0402.step_5780:3"
  other  "RES0402.step_5780:4"
  other  "RES0402.step_5782:1"
  other  "RES0402.step_5782:2"
  other  "RES0402.step_5782:3"
  other  "RES0402.step_5782:4"
  other  "RES0402.step_5784:1"
  other  "RES0402.step_5784:2"
  other  "RES0402.step_5784:3"
  other  "RES0402.step_5784:4"
  other  "RES0402.step_5786:1"
  other  "RES0402.step_5786:2"
  other  "RES0402.step_5786:3"
  other  "RES0402.step_5786:4"
  other  "CAP0201.step_5788:1"
  other  "CAP0201.step_5790:1"
  other  "CAP0201.step_5792:1"
  other  "CAP0201.step_5794:1"
  other  "CAP0201.step_5796:1"
  other  "CAP0201.step_5798:1"
  other  "SOT883B Mold body_5800:1"
  other  "SOT883B4 LF_5801:1"
  other  "SOT883B4 LF_5801:2"
  other  "SOT883B4 LF_5801:3"
  other  "SOT883B4 LF_5801:4"
  other  "SOT883B4 LF_5801:5"
  other  "SOT883B4 LF_5801:6"
  other  "SOT883B4 LF_5801:7"
  other  "SOT883B4 LF_5801:8"
  other  "SOT883B4 LF_5801:9"
  other  "SOT883B4 LF_5801:10"
  other  "SOT883B4 LF_5801:11"
  other  "SOT883B4 LF_5801:12"
  other  "SOT883B4 LF_5801:13"
  other  "SOT883B Mold body_5800:2"
  other  "SOT883B4 LF_5801:14"
  other  "SOT883B4 LF_5801:15"
  other  "SOT883B4 LF_5801:16"
  other  "SOT883B4 LF_5801:17"
  other  "SOT883B4 LF_5801:18"
  other  "SOT883B4 LF_5801:19"
  other  "SOT883B4 LF_5801:20"
  other  "SOT883B4 LF_5801:21"
  other  "SOT883B4 LF_5801:22"
  other  "SOT883B4 LF_5801:23"
  other  "SOT883B4 LF_5801:24"
  other  "SOT883B4 LF_5801:25"
  other  "SOT883B4 LF_5801:26"
  other  "ProjectY v3 STEP.STEP_5809:1"
  other  "(Unsaved)_5811:1"
  other  "(Unsaved)_5811:2"
  other  "(Unsaved)_5811:3"
  other  "(Unsaved)_5811:4"
  other  "(Unsaved)_5811:5"
  other  "(Unsaved)_5811:6"
  other  "(Unsaved)_5811:7"
  other  "(Unsaved)_5811:8"
  other  "(Unsaved)_5811:9"
  other  "(Unsaved)_5811:10"
  other  "(Unsaved)_5811:11"
  other  "(Unsaved)_5811:12"
  other  "(Unsaved)_5811:13"
  other  "(Unsaved)_5811:14"
  other  "(Unsaved)_5811:15"
  other  "(Unsaved)_5811:16"
  other  "(Unsaved)_5811:17"
  other  "(Unsaved)_5811:18"
  other  "(Unsaved)_5811:19"
  other  "(Unsaved)_5811:20"
  other  "(Unsaved)_5811:21"
  other  "(Unsaved)_5811:22"
  other  "(Unsaved)_5811:23"
  other  "(Unsaved)_5811:24"
  other  "(Unsaved)_5811:25"
  other  "(Unsaved)_5811:26"
  other  "(Unsaved)_5811:27"
  other  "(Unsaved)_5811:28"
  other  "(Unsaved)_5811:29"
  other  "(Unsaved)_5811:30"
  other  "(Unsaved)_5811:31"
  other  "(Unsaved)_5811:32"
  other  "(Unsaved)_5811:33"
  other  "(Unsaved)_5811:34"
  other  "(Unsaved)_5811:35"
  other  "(Unsaved)_5811:36"
  other  "(Unsaved)_5811:37"
  other  "(Unsaved)_5811:38"
  other  "(Unsaved)_5811:39"
  other  "(Unsaved)_5811:40"
  other  "(Unsaved)_5811:41"
  other  "(Unsaved)_5811:42"
  other  "(Unsaved)_5811:43"
  other  "(Unsaved)_5811:44"
  other  "(Unsaved)_5811:45"
  other  "(Unsaved)_5811:46"
  other  "(Unsaved)_5811:47"
  other  "(Unsaved)_5811:48"
  other  "(Unsaved)_5811:49"
  other  "(Unsaved)_5811:50"
  other  "(Unsaved)_5811:51"
  other  "Box_5813:1"
  other  "Box_5813:2"
  other  "Fusion_5815:1"
  other  "CAP0201.step_5820:1"
  other  "CAP0201.step_5822:1"
  other  "CAP0201.step_5824:1"
  other  "CAP0201.step_5826:1"
  other  "CAP0201.step_5828:1"
  other  "CAP0201.step_5830:1"
  other  "CAP0201.step_5832:1"
  other  "CAP0201.step_5834:1"
  other  "CAP0201.step_5836:1"
  other  "CAP0201.step_5838:1"
  other  "CAP0201.step_5840:1"
  other  "CAP0201.step_5842:1"
  other  "CAP0201.step_5844:1"
  other  "CAP0201.step_5846:1"
  other  "CAP0201.step_5848:1"
  other  "CAP0201.step_5850:1"
  other  "CAP0201.step_5852:1"
  other  "CAP0201.step_5854:1"
  other  "CAP0201.step_5856:1"
  other  "CAP0201.step_5858:1"
  other  "CAP0201.step_5860:1"
  other  "CAP0201.step_5862:1"
  other  "CAP0201.step_5864:1"
  other  "CAP0201.step_5866:1"
  other  "CAP0201.step_5868:1"
  other  "CAP0201.step_5870:1"
  other  "CAP0201.step_5872:1"
  other  "CAP0201.step_5874:1"
  other  "CAP0201.step_5876:1"
  other  "CAP0201.step_5878:1"
  other  "CAP0201.step_5880:1"
  other  "CAP0201.step_5882:1"
  other  "CAP0201.step_5884:1"
  other  "CAP0201.step_5886:1"
  other  "CAP0201.step_5888:1"
  other  "CAP0201.step_5890:1"
  other  "CAP0201.step_5892:1"
  other  "CAP0201.step_5894:1"
  other  "CAP0201.step_5896:1"
  other  "CAP0201.step_5898:1"
  other  "CAP0201.step_5900:1"
  other  "CAP0201.step_5902:1"
  other  "CAP0201.step_5904:1"
  other  "CAP0201.step_5906:1"
  other  "CAP0201.step_5908:1"
  other  "CAP0201.step_5910:1"
  other  "CAP0201.step_5912:1"
  other  "CAP0201.step_5914:1"
  other  "CAP0201.step_5916:1"
  other  "CAP0201.step_5918:1"
  other  "CAP0201.step_5920:1"
  other  "CAP0201.step_5922:1"
  other  "CAP0201.step_5924:1"
  other  "CAP0201.step_5926:1"
  other  "CAP0201.step_5928:1"
  other  "CAP0201.step_5930:1"
  other  "CAP0201.step_5932:1"
  other  "CAP0201.step_5934:1"
  other  "CAP0201.step_5936:1"
  other  "CAP0201.step_5938:1"
  other  "CAP0201.step_5940:1"
  other  "CAP0201.step_5942:1"
  other  "CAP0201.step_5944:1"
  other  "CAP0201.step_5946:1"
  other  "CAP0201.step_5948:1"
  other  "CAP0201.step_5950:1"
  other  "CAP0201.step_5952:1"
  other  "CAP0201.step_5954:1"
  other  "CAP0201.step_5956:1"
  other  "CAP0201.step_5958:1"
  other  "CAP0201.step_5960:1"
  other  "CAP0201.step_5962:1"
  other  "CAP0201.step_5964:1"
  other  "CAP0201.step_5966:1"
  other  "CAP0201.step_5968:1"
  other  "CAP0201.step_5970:1"
  other  "CAP0201.step_5972:1"
  other  "CAP0201.step_5974:1"
  other  "CAP0201.step_5976:1"
  other  "CAP0201.step_5978:1"
  other  "CAP0201.step_5980:1"
  other  "CAP0201.step_5982:1"
  other  "CAP0201.step_5984:1"
  other  "CAP0201.step_5986:1"
  other  "CAP0201.step_5988:1"
  other  "CAP0201.step_5990:1"
  other  "CAP0201.step_5992:1"
  other  "CAP0201.step_5994:1"
  other  "CAP0201.step_5996:1"
  other  "CAP0201.step_5998:1"
  other  "CAP0201.step_6000:1"
  other  "CAP0201.step_6002:1"
  other  "CAP0201.step_6004:1"
  other  "CAP0201.step_6006:1"
  other  "CAP0201.step_6008:1"
  other  "CAP0201.step_6010:1"
  other  "CAP0201.step_6012:1"
  other  "CAP0201.step_6014:1"
  other  "CAP0201.step_6016:1"
  other  "CAP0201.step_6018:1"
  other  "CAP0201.step_6020:1"
  other  "CAP0201.step_6022:1"
  other  "CAP0201.step_6024:1"
  other  "CAP0201.step_6026:1"
  other  "CAP0201.step_6028:1"
  other  "CAP0201.step_6030:1"
  other  "CAP0201.step_6032:1"
  other  "CAP0201.step_6034:1"
  other  "CAP0201.step_6036:1"
  other  "CAP0201.step_6038:1"
  other  "CAP0201.step_6040:1"
  other  "CAP0201.step_6042:1"
  other  "CAP0201.step_6044:1"
  other  "CAP0201.step_6046:1"
  other  "CAP0201.step_6048:1"
  other  "CAP0201.step_6050:1"
  other  "CAP0201.step_6052:1"
  other  "CAP0201.step_6054:1"
  other  "CAP0201.step_6056:1"
  other  "CAP0201.step_6058:1"
  other  "CAP0201.step_6060:1"
  other  "CAP0201.step_6062:1"
  other  "CAP0201.step_6064:1"
  other  "CAP0201.step_6066:1"
  other  "CAP0201.step_6068:1"
  other  "CAP0201.step_6070:1"
  other  "CAP0201.step_6072:1"
  other  "CAP0201.step_6074:1"
  other  "CAP0201.step_6076:1"
  other  "CAP0201.step_6078:1"
  other  "CAP0201.step_6080:1"
  other  "CAP0201.step_6082:1"
  other  "CAP0201.step_6084:1"
  other  "CAP0201.step_6086:1"
  other  "CAP0201.step_6088:1"
  other  "CAP0201.step_6090:1"
  other  "CAP0201.step_6092:1"
  other  "CAP0201.step_6094:1"
  other  "CAP0201.step_6096:1"
  other  "CAP0201.step_6098:1"
  other  "CAP0201.step_6100:1"
  other  "CAP0201.step_6102:1"
  other  "CAP0201.step_6104:1"
  other  "CAP0201.step_6106:1"
  other  "CAP0201.step_6108:1"
  other  "CAP0201.step_6110:1"
  other  "CAP0201.step_6112:1"
  other  "CAP0201.step_6114:1"
  other  "CAP0201.step_6116:1"
  other  "CAP0201.step_6118:1"
  other  "CAP0201.step_6120:1"
  other  "RES0201old.step_6122:1"
  other  "RES0201old.step_6122:2"
  other  "RES0201old.step_6124:1"
  other  "RES0201old.step_6124:2"
  other  "RES0201old.step_6126:1"
  other  "RES0201old.step_6126:2"
  other  "RES0201old.step_6128:1"
  other  "RES0201old.step_6128:2"
  other  "RES0201old.step_6130:1"
  other  "RES0201old.step_6130:2"
  other  "RES0201old.step_6132:1"
  other  "RES0201old.step_6132:2"
  other  "RES0201old.step_6134:1"
  other  "RES0201old.step_6134:2"
  other  "RES0201old.step_6136:1"
  other  "RES0201old.step_6136:2"
  other  "RES0201old.step_6138:1"
  other  "RES0201old.step_6138:2"
  other  "RES0201old.step_6140:1"
  other  "RES0201old.step_6140:2"
  other  "RES0201old.step_6142:1"
  other  "RES0201old.step_6142:2"
  other  "RES0201old.step_6144:1"
  other  "RES0201old.step_6144:2"
  other  "RES0201old.step_6146:1"
  other  "RES0201old.step_6146:2"
  other  "RES0201old.step_6148:1"
  other  "RES0201old.step_6148:2"
  other  "RES0201old.step_6150:1"
  other  "RES0201old.step_6150:2"
  other  "RES0201old.step_6152:1"
  other  "RES0201old.step_6152:2"
  other  "RES0201old.step_6154:1"
  other  "RES0201old.step_6154:2"
  other  "RES0201old.step_6156:1"
  other  "RES0201old.step_6156:2"
  other  "RES0201old.step_6158:1"
  other  "RES0201old.step_6158:2"
  other  "RES0201old.step_6160:1"
  other  "RES0201old.step_6160:2"
  other  "RES0201old.step_6162:1"
  other  "RES0201old.step_6162:2"
  other  "RES0201old.step_6164:1"
  other  "RES0201old.step_6164:2"
  other  "RES0201old.step_6166:1"
  other  "RES0201old.step_6166:2"
  other  "RES0201old.step_6168:1"
  other  "RES0201old.step_6168:2"
  other  "RES0201old.step_6170:1"
  other  "RES0201old.step_6170:2"
  other  "RES0201old.step_6172:1"
  other  "RES0201old.step_6172:2"
  other  "RES0201old.step_6174:1"
  other  "RES0201old.step_6174:2"
  other  "RES0201old.step_6176:1"
  other  "RES0201old.step_6176:2"
  other  "RES0201old.step_6178:1"
  other  "RES0201old.step_6178:2"
  other  "RES0201old.step_6180:1"
  other  "RES0201old.step_6180:2"
  other  "RES0201old.step_6182:1"
  other  "RES0201old.step_6182:2"
  other  "RES0201old.step_6184:1"
  other  "RES0201old.step_6184:2"
  other  "RES0201old.step_6186:1"
  other  "RES0201old.step_6186:2"
  other  "RES0201old.step_6188:1"
  other  "RES0201old.step_6188:2"
  other  "RES0201old.step_6190:1"
  other  "RES0201old.step_6190:2"
  other  "RES0201old.step_6192:1"
  other  "RES0201old.step_6192:2"
  other  "RES0201old.step_6194:1"
  other  "RES0201old.step_6194:2"
  other  "RES0201old.step_6196:1"
  other  "RES0201old.step_6196:2"
  other  "RES0201old.step_6198:1"
  other  "RES0201old.step_6198:2"
  other  "RES0201old.step_6200:1"
  other  "RES0201old.step_6200:2"
  other  "RES0201old.step_6202:1"
  other  "RES0201old.step_6202:2"
  other  "RES0201old.step_6204:1"
  other  "RES0201old.step_6204:2"
  other  "RES0201old.step_6206:1"
  other  "RES0201old.step_6206:2"
  other  "RES0201old.step_6208:1"
  other  "RES0201old.step_6208:2"
  other  "RES0201old.step_6210:1"
  other  "RES0201old.step_6210:2"
  other  "RES0201old.step_6212:1"
  other  "RES0201old.step_6212:2"
  other  "RES0201old.step_6214:1"
  other  "RES0201old.step_6214:2"
  other  "RES0201old.step_6216:1"
  other  "RES0201old.step_6216:2"
  other  "RES0201old.step_6218:1"
  other  "RES0201old.step_6218:2"
  other  "RES0201old.step_6220:1"
  other  "RES0201old.step_6220:2"
  other  "RES0201old.step_6222:1"
  other  "RES0201old.step_6222:2"
  other  "RES0201old.step_6224:1"
  other  "RES0201old.step_6224:2"
  other  "RES0201old.step_6226:1"
  other  "RES0201old.step_6226:2"
  other  "RES0201old.step_6228:1"
  other  "RES0201old.step_6228:2"
  other  "RES0201old.step_6230:1"
  other  "RES0201old.step_6230:2"
  other  "RES0201old.step_6232:1"
  other  "RES0201old.step_6232:2"
  other  "RES0201old.step_6234:1"
  other  "RES0201old.step_6234:2"
  other  "PinIndicator_6236:1"
  other  "Pads_6237:1"
  other  "Lid_6238:1"
  other  "Body_6239:1"
  other  "Pad001_6243:1"
  other  "Cut_6244:1"
  other  "Cut_6244:2"
  other  "Pad001_6243:2"
  other  "Cut_6244:3"
  other  "Cut_6244:4"
  other  "Pad001_6243:3"
  other  "Cut_6244:5"
  other  "Cut_6244:6"
  other  "Pad001_6243:4"
  other  "Cut_6244:7"
  other  "Cut_6244:8"
  other  "Pad001_6243:5"
  other  "Cut_6244:9"
  other  "Cut_6244:10"
  other  "Pad001_6243:6"
  other  "Cut_6244:11"
  other  "Cut_6244:12"
  other  "Pad001_6243:7"
  other  "Cut_6244:13"
  other  "Cut_6244:14"
  other  "Pad001_6243:8"
  other  "Cut_6244:15"
  other  "Cut_6244:16"
  other  "Pad001_6243:9"
  other  "Cut_6244:17"
  other  "Cut_6244:18"
  other  "Pad001_6243:10"
  other  "Cut_6244:19"
  other  "Cut_6244:20"
  other  "Pad001_6243:11"
  other  "Cut_6244:21"
  other  "Cut_6244:22"
  other  "Pad001_6243:12"
  other  "Cut_6244:23"
  other  "Cut_6244:24"
  other  "Pad001_6243:13"
  other  "Cut_6244:25"
  other  "Cut_6244:26"
  other  "Pad001_6243:14"
  other  "Cut_6244:27"
  other  "Cut_6244:28"
  other  "Pad001_6243:15"
  other  "Cut_6244:29"
  other  "Cut_6244:30"
  other  "Pad001_6243:16"
  other  "Cut_6244:31"
  other  "Cut_6244:32"
  other  "Pad001_6243:17"
  other  "Cut_6244:33"
  other  "Cut_6244:34"
  other  "Pad001_6243:18"
  other  "Cut_6244:35"
  other  "Cut_6244:36"
  other  "Pad001_6243:19"
  other  "Cut_6244:37"
  other  "Cut_6244:38"
  other  "Pad001_6243:20"
  other  "Cut_6244:39"
  other  "Cut_6244:40"
  other  "Pad001_6243:21"
  other  "Cut_6244:41"
  other  "Cut_6244:42"
  other  "Pad001_6243:22"
  other  "Cut_6244:43"
  other  "Cut_6244:44"
  other  "CAP0402.step_6290:1"
  other  "CAP0402.step_6292:1"
  other  "CAP0402.step_6294:1"
  other  "CAP0402.step_6296:1"
  other  "CAP0402.step_6298:1"
  other  "CAP0402.step_6300:1"
  other  "CAP0402.step_6302:1"
  other  "CAP0402.step_6304:1"
  other  "CAP0402.step_6306:1"
  other  "CAP0402.step_6308:1"
  other  "CAP0402.step_6310:1"
  other  "CAP0402.step_6312:1"
  other  "CAP0402.step_6314:1"
  other  "CAP0402.step_6316:1"
  other  "CAP0402.step_6318:1"
  other  "CAP0402.step_6320:1"
  other  "CAP0402.step_6322:1"
  other  "CAP0402.step_6324:1"
  other  "CAP0402.step_6326:1"
  other  "CAP0402.step_6328:1"
  other  "CAP0402.step_6330:1"
  other  "CAP0402.step_6332:1"
  other  "CAP0402.step_6334:1"
  other  "CAP0402.step_6336:1"
  other  "CAP0402.step_6338:1"
  other  "CAP0402.step_6340:1"
  other  "CAP0402.step_6342:1"
  other  "CAP0402.step_6344:1"
  other  "CAP0402.step_6346:1"
  other  "CAP0402.step_6348:1"
  other  "CAP0402.step_6350:1"
  other  "CAP0402.step_6352:1"
  other  "CAP0402.step_6354:1"
  other  "CAP0402.step_6356:1"
  other  "CAP0402.step_6358:1"
  other  "CAP0402.step_6360:1"
  other  "CAP0402.step_6362:1"
  other  "CAP0402.step_6364:1"
  other  "CAP0402.step_6366:1"
  other  "CAP0402.step_6368:1"
  other  "CAP0402.step_6370:1"
  other  "CAP0402.step_6372:1"
  other  "CAP0402.step_6374:1"
  other  "CAP0402.step_6376:1"
  other  "CAP0402.step_6378:1"
  other  "CAP0402.step_6380:1"
  other  "CAP0402.step_6382:1"
  other  "CAP0402.step_6384:1"
  other  "CAP0402.step_6386:1"
  other  "CAP0402.step_6388:1"
  other  "CAP0402.step_6390:1"
  other  "CAP0402.step_6392:1"
  other  "CAP0402.step_6394:1"
  other  "CAP0402.step_6396:1"
  other  "CAP0402.step_6398:1"
  other  "CAP0402.step_6400:1"
  other  "CAP0402.step_6402:1"
  other  "CAP0402.step_6404:1"
  other  "CAP0402.step_6406:1"
  other  "Plating_6408:1"
  other  "Plating_6408:2"
  other  "Plating_6408:3"
  other  "Plating_6408:4"
  other  "Plating_6408:5"
  other  "LDF_6409:1"
  other  "LDF_6409:2"
  other  "LDF_6409:3"
  other  "LDF_6409:4"
  other  "LDF_6409:5"
  other  "CPD_6410:1"
  other  "Pads_6414:1"
  other  "Lid_6415:1"
  other  "Body_6416:1"
  other  "Pins_6420:1"
  other  "Pins_6420:2"
  other  "Pins_6420:3"
  other  "Pins_6420:4"
  other  "Pins_6420:5"
  other  "Pins_6420:6"
  other  "Pins_6420:7"
  other  "Pins_6420:8"
  other  "Body_6421:1"
  other  "CAP0603.step_6425:1"
  other  "CAP0603.step_6427:1"
  other  "CAP0603.step_6429:1"
  other  "CAP0603.step_6431:1"
  other  "CAP0603.step_6433:1"
  other  "CAP0603.step_6435:1"
  other  "Part_18370_6437:1"
  other  "Part_739_6438:1"
  other  "Part_740_6439:1"
  other  "Part_665_6440:1"
  other  "Part_637_6441:1"
  other  "Part_609_6442:1"
  other  "Part_581_6443:1"
  other  "Part_553_6444:1"
  other  "Part_525_6445:1"
  other  "Part_496_6446:1"
  other  "SOT883B Mold body_5800:3"
  other  "SOT883B4 LF_5801:27"
  other  "SOT883B4 LF_5801:28"
  other  "SOT883B4 LF_5801:29"
  other  "SOT883B4 LF_5801:30"
  other  "SOT883B4 LF_5801:31"
  other  "SOT883B4 LF_5801:32"
  other  "SOT883B4 LF_5801:33"
  other  "SOT883B4 LF_5801:34"
  other  "SOT883B4 LF_5801:35"
  other  "SOT883B4 LF_5801:36"
  other  "SOT883B4 LF_5801:37"
  other  "SOT883B4 LF_5801:38"
  other  "SOT883B4 LF_5801:39"
  other  "SOT883B Mold body_5800:4"
  other  "SOT883B4 LF_5801:40"
  other  "SOT883B4 LF_5801:41"
  other  "SOT883B4 LF_5801:42"
  other  "SOT883B4 LF_5801:43"
  other  "SOT883B4 LF_5801:44"
  other  "SOT883B4 LF_5801:45"
  other  "SOT883B4 LF_5801:46"
  other  "SOT883B4 LF_5801:47"
  other  "SOT883B4 LF_5801:48"
  other  "SOT883B4 LF_5801:49"
  other  "SOT883B4 LF_5801:50"
  other  "SOT883B4 LF_5801:51"
  other  "SOT883B4 LF_5801:52"
  other  "User Library-153BallWFBGA_6454:1"
  other  "User Library-153BallWFBGA_6454:2"
  other  "User Library-153BallWFBGA_6454:3"
  other  "User Library-153BallWFBGA_6454:4"
  other  "User Library-153BallWFBGA_6454:5"
  other  "User Library-153BallWFBGA_6454:6"
  other  "User Library-153BallWFBGA_6454:7"
  other  "User Library-153BallWFBGA_6454:8"
  other  "User Library-153BallWFBGA_6454:9"
  other  "User Library-153BallWFBGA_6454:10"
  other  "User Library-153BallWFBGA_6454:11"
  other  "User Library-153BallWFBGA_6454:12"
  other  "User Library-153BallWFBGA_6454:13"
  other  "User Library-153BallWFBGA_6454:14"
  other  "User Library-153BallWFBGA_6454:15"
  other  "User Library-153BallWFBGA_6454:16"
  other  "User Library-153BallWFBGA_6454:17"
  other  "User Library-153BallWFBGA_6454:18"
  other  "User Library-153BallWFBGA_6454:19"
  other  "User Library-153BallWFBGA_6454:20"
  other  "User Library-153BallWFBGA_6454:21"
  other  "User Library-153BallWFBGA_6454:22"
  other  "User Library-153BallWFBGA_6454:23"
  other  "User Library-153BallWFBGA_6454:24"
  other  "User Library-153BallWFBGA_6454:25"
  other  "User Library-153BallWFBGA_6454:26"
  other  "User Library-153BallWFBGA_6454:27"
  other  "User Library-153BallWFBGA_6454:28"
  other  "User Library-153BallWFBGA_6454:29"
  other  "User Library-153BallWFBGA_6454:30"
  other  "User Library-153BallWFBGA_6454:31"
  other  "User Library-153BallWFBGA_6454:32"
  other  "User Library-153BallWFBGA_6454:33"
  other  "User Library-153BallWFBGA_6454:34"
  other  "User Library-153BallWFBGA_6454:35"
  other  "User Library-153BallWFBGA_6454:36"
  other  "User Library-153BallWFBGA_6454:37"
  other  "User Library-153BallWFBGA_6454:38"
  other  "User Library-153BallWFBGA_6454:39"
  other  "User Library-153BallWFBGA_6454:40"
  other  "User Library-153BallWFBGA_6454:41"
  other  "User Library-153BallWFBGA_6454:42"
  other  "User Library-153BallWFBGA_6454:43"
  other  "User Library-153BallWFBGA_6454:44"
  other  "User Library-153BallWFBGA_6454:45"
  other  "User Library-153BallWFBGA_6454:46"
  other  "User Library-153BallWFBGA_6454:47"
  other  "User Library-153BallWFBGA_6454:48"
  other  "User Library-153BallWFBGA_6454:49"
  other  "User Library-153BallWFBGA_6454:50"
  other  "User Library-153BallWFBGA_6454:51"
  other  "User Library-153BallWFBGA_6454:52"
  other  "User Library-153BallWFBGA_6454:53"
  other  "User Library-153BallWFBGA_6454:54"
  other  "User Library-153BallWFBGA_6454:55"
  other  "User Library-153BallWFBGA_6454:56"
  other  "User Library-153BallWFBGA_6454:57"
  other  "User Library-153BallWFBGA_6454:58"
  other  "User Library-153BallWFBGA_6454:59"
  other  "User Library-153BallWFBGA_6454:60"
  other  "User Library-153BallWFBGA_6454:61"
  other  "User Library-153BallWFBGA_6454:62"
  other  "User Library-153BallWFBGA_6454:63"
  other  "User Library-153BallWFBGA_6454:64"
  other  "User Library-153BallWFBGA_6454:65"
  other  "User Library-153BallWFBGA_6454:66"
  other  "User Library-153BallWFBGA_6454:67"
  other  "User Library-153BallWFBGA_6454:68"
  other  "User Library-153BallWFBGA_6454:69"
  other  "User Library-153BallWFBGA_6454:70"
  other  "User Library-153BallWFBGA_6454:71"
  other  "User Library-153BallWFBGA_6454:72"
  other  "User Library-153BallWFBGA_6454:73"
  other  "User Library-153BallWFBGA_6454:74"
  other  "User Library-153BallWFBGA_6454:75"
  other  "User Library-153BallWFBGA_6454:76"
  other  "User Library-153BallWFBGA_6454:77"
  other  "User Library-153BallWFBGA_6454:78"
  other  "User Library-153BallWFBGA_6454:79"
  other  "User Library-153BallWFBGA_6454:80"
  other  "User Library-153BallWFBGA_6454:81"
  other  "User Library-153BallWFBGA_6454:82"
  other  "User Library-153BallWFBGA_6454:83"
  other  "User Library-153BallWFBGA_6454:84"
  other  "User Library-153BallWFBGA_6454:85"
  other  "User Library-153BallWFBGA_6454:86"
  other  "User Library-153BallWFBGA_6454:87"
  other  "User Library-153BallWFBGA_6454:88"
  other  "User Library-153BallWFBGA_6454:89"
  other  "User Library-153BallWFBGA_6454:90"
  other  "User Library-153BallWFBGA_6454:91"
  other  "User Library-153BallWFBGA_6454:92"
  other  "User Library-153BallWFBGA_6454:93"
  other  "User Library-153BallWFBGA_6454:94"
  other  "User Library-153BallWFBGA_6454:95"
  other  "User Library-153BallWFBGA_6454:96"
  other  "User Library-153BallWFBGA_6454:97"
  other  "User Library-153BallWFBGA_6454:98"
  other  "User Library-153BallWFBGA_6454:99"
  other  "User Library-153BallWFBGA_6454:100"
  other  "User Library-153BallWFBGA_6454:101"
  other  "User Library-153BallWFBGA_6454:102"
  other  "User Library-153BallWFBGA_6454:103"
  other  "User Library-153BallWFBGA_6454:104"
  other  "User Library-153BallWFBGA_6454:105"
  other  "User Library-153BallWFBGA_6454:106"
  other  "User Library-153BallWFBGA_6454:107"
  other  "User Library-153BallWFBGA_6454:108"
  other  "User Library-153BallWFBGA_6454:109"
  other  "User Library-153BallWFBGA_6454:110"
  other  "User Library-153BallWFBGA_6454:111"
  other  "User Library-153BallWFBGA_6454:112"
  other  "User Library-153BallWFBGA_6454:113"
  other  "User Library-153BallWFBGA_6454:114"
  other  "User Library-153BallWFBGA_6454:115"
  other  "User Library-153BallWFBGA_6454:116"
  other  "User Library-153BallWFBGA_6454:117"
  other  "User Library-153BallWFBGA_6454:118"
  other  "User Library-153BallWFBGA_6454:119"
  other  "User Library-153BallWFBGA_6454:120"
  other  "User Library-153BallWFBGA_6454:121"
  other  "User Library-153BallWFBGA_6454:122"
  other  "User Library-153BallWFBGA_6454:123"
  other  "User Library-153BallWFBGA_6454:124"
  other  "User Library-153BallWFBGA_6454:125"
  other  "User Library-153BallWFBGA_6454:126"
  other  "User Library-153BallWFBGA_6454:127"
  other  "User Library-153BallWFBGA_6454:128"
  other  "User Library-153BallWFBGA_6454:129"
  other  "User Library-153BallWFBGA_6454:130"
  other  "User Library-153BallWFBGA_6454:131"
  other  "User Library-153BallWFBGA_6454:132"
  other  "User Library-153BallWFBGA_6454:133"
  other  "User Library-153BallWFBGA_6454:134"
  other  "User Library-153BallWFBGA_6454:135"
  other  "User Library-153BallWFBGA_6454:136"
  other  "User Library-153BallWFBGA_6454:137"
  other  "User Library-153BallWFBGA_6454:138"
  other  "User Library-153BallWFBGA_6454:139"
  other  "User Library-153BallWFBGA_6454:140"
  other  "User Library-153BallWFBGA_6454:141"
  other  "User Library-153BallWFBGA_6454:142"
  other  "User Library-153BallWFBGA_6454:143"
  other  "User Library-153BallWFBGA_6454:144"
  other  "User Library-153BallWFBGA_6454:145"
  other  "User Library-153BallWFBGA_6454:146"
  other  "User Library-153BallWFBGA_6454:147"
  other  "User Library-153BallWFBGA_6454:148"
  other  "User Library-153BallWFBGA_6454:149"
  other  "User Library-153BallWFBGA_6454:150"
  other  "User Library-153BallWFBGA_6454:151"
  other  "User Library-153BallWFBGA_6454:152"
  other  "User Library-153BallWFBGA_6454:153"
  other  "User Library-153BallWFBGA_6454:154"
  other  "User Library-153BallWFBGA_6454:155"
  other  "User Library-153BallWFBGA_6454:156"
  other  "10164228-1001A1RLF.stp_6456:1"
  other  "10164228-1001A1RLF.stp_6458:1"
  other  "ABM11-0022-T3.step_6460:1"
  other  "ABM11-0022-T3.step_6462:1"
  other  "DIELECTRIC_Model_1_Inst_6466:1"
  other  "User Library-User Library-res0402_res0402_body_6470:1"
  other  "User Library-User Library-res0402_res0402_body_6472:1"
  other  "User Library-Chip Cap_MLCC_0402 (1005)_6474:1"
  other  "User Library-Chip Cap_MLCC_0402 (1005)_6476:1"
  other  "User Library-Chip Cap_MLCC_0402 (1005)_6478:1"
  other  "User Library-Chip Cap_MLCC_0402 (1005)_6480:1"
  other  "User Library-Chip Cap_MLCC_0402 (1005)_6482:1"
  other  "User Library-Chip Cap_MLCC_0402 (1005)_6484:1"
  other  "User Library-WS2812-4020_6486:1"
  other  "User Library-WS2812-4020_6486:2"
  other  "User Library-WS2812-4020_6486:3"
  other  "User Library-WS2812-4020_6486:4"
  other  "User Library-WS2812-4020_6486:5"
  other  "User Library-WS2812-4020_6486:6"
  other  "User Library-WS2812-4020_6486:7"
  other  "User Library-WS2812-4020_6486:8"
  other  "User Library-WS2812-4020_6486:9"
  other  "User Library-WS2812-4020_6486:10"
  other  "User Library-WS2812-4020_6488:1"
  other  "User Library-WS2812-4020_6488:2"
  other  "User Library-WS2812-4020_6488:3"
  other  "User Library-WS2812-4020_6488:4"
  other  "User Library-WS2812-4020_6488:5"
  other  "User Library-WS2812-4020_6488:6"
  other  "User Library-WS2812-4020_6488:7"
  other  "User Library-WS2812-4020_6488:8"
  other  "User Library-WS2812-4020_6488:9"
  other  "User Library-WS2812-4020_6488:10"
  other  "User Library-WS2812-4020_6490:1"
  other  "User Library-WS2812-4020_6490:2"
  other  "User Library-WS2812-4020_6490:3"
  other  "User Library-WS2812-4020_6490:4"
  other  "User Library-WS2812-4020_6490:5"
  other  "User Library-WS2812-4020_6490:6"
  other  "User Library-WS2812-4020_6490:7"
  other  "User Library-WS2812-4020_6490:8"
  other  "User Library-WS2812-4020_6490:9"
  other  "User Library-WS2812-4020_6490:10"
  other  "User Library-WS2812-4020_6492:1"
  other  "User Library-WS2812-4020_6492:2"
  other  "User Library-WS2812-4020_6492:3"
  other  "User Library-WS2812-4020_6492:4"
  other  "User Library-WS2812-4020_6492:5"
  other  "User Library-WS2812-4020_6492:6"
  other  "User Library-WS2812-4020_6492:7"
  other  "User Library-WS2812-4020_6492:8"
  other  "User Library-WS2812-4020_6492:9"
  other  "User Library-WS2812-4020_6492:10"
  other  "User Library-WS2812-4020_6494:1"
  other  "User Library-WS2812-4020_6494:2"
  other  "User Library-WS2812-4020_6494:3"
  other  "User Library-WS2812-4020_6494:4"
  other  "User Library-WS2812-4020_6494:5"
  other  "User Library-WS2812-4020_6494:6"
  other  "User Library-WS2812-4020_6494:7"
  other  "User Library-WS2812-4020_6494:8"
  other  "User Library-WS2812-4020_6494:9"
  other  "User Library-WS2812-4020_6494:10"
  other  "User Library-WS2812-4020_6496:1"
  other  "User Library-WS2812-4020_6496:2"
  other  "User Library-WS2812-4020_6496:3"
  other  "User Library-WS2812-4020_6496:4"
  other  "User Library-WS2812-4020_6496:5"
  other  "User Library-WS2812-4020_6496:6"
  other  "User Library-WS2812-4020_6496:7"
  other  "User Library-WS2812-4020_6496:8"
  other  "User Library-WS2812-4020_6496:9"
  other  "User Library-WS2812-4020_6496:10"
  other  "User Library-WS2812-4020_6498:1"
  other  "User Library-WS2812-4020_6498:2"
  other  "User Library-WS2812-4020_6498:3"
  other  "User Library-WS2812-4020_6498:4"
  other  "User Library-WS2812-4020_6498:5"
  other  "User Library-WS2812-4020_6498:6"
  other  "User Library-WS2812-4020_6498:7"
  other  "User Library-WS2812-4020_6498:8"
  other  "User Library-WS2812-4020_6498:9"
  other  "User Library-WS2812-4020_6498:10"
  other  "User Library-WS2812-4020_6500:1"
  other  "User Library-WS2812-4020_6500:2"
  other  "User Library-WS2812-4020_6500:3"
  other  "User Library-WS2812-4020_6500:4"
  other  "User Library-WS2812-4020_6500:5"
  other  "User Library-WS2812-4020_6500:6"
  other  "User Library-WS2812-4020_6500:7"
  other  "User Library-WS2812-4020_6500:8"
  other  "User Library-WS2812-4020_6500:9"
  other  "User Library-WS2812-4020_6500:10"
  other  "User Library-WS2812-4020_6502:1"
  other  "User Library-WS2812-4020_6502:2"
  other  "User Library-WS2812-4020_6502:3"
  other  "User Library-WS2812-4020_6502:4"
  other  "User Library-WS2812-4020_6502:5"
  other  "User Library-WS2812-4020_6502:6"
  other  "User Library-WS2812-4020_6502:7"
  other  "User Library-WS2812-4020_6502:8"
  other  "User Library-WS2812-4020_6502:9"
  other  "User Library-WS2812-4020_6502:10"
  other  "User Library-WS2812-4020_6504:1"
  other  "User Library-WS2812-4020_6504:2"
  other  "User Library-WS2812-4020_6504:3"
  other  "User Library-WS2812-4020_6504:4"
  other  "User Library-WS2812-4020_6504:5"
  other  "User Library-WS2812-4020_6504:6"
  other  "User Library-WS2812-4020_6504:7"
  other  "User Library-WS2812-4020_6504:8"
  other  "User Library-WS2812-4020_6504:9"
  other  "User Library-WS2812-4020_6504:10"
  other  "User Library-WS2812-4020_6506:1"
  other  "User Library-WS2812-4020_6506:2"
  other  "User Library-WS2812-4020_6506:3"
  other  "User Library-WS2812-4020_6506:4"
  other  "User Library-WS2812-4020_6506:5"
  other  "User Library-WS2812-4020_6506:6"
  other  "User Library-WS2812-4020_6506:7"
  other  "User Library-WS2812-4020_6506:8"
  other  "User Library-WS2812-4020_6506:9"
  other  "User Library-WS2812-4020_6506:10"
  other  "User Library-WS2812-4020_6508:1"
  other  "User Library-WS2812-4020_6508:2"
  other  "User Library-WS2812-4020_6508:3"
  other  "User Library-WS2812-4020_6508:4"
  other  "User Library-WS2812-4020_6508:5"
  other  "User Library-WS2812-4020_6508:6"
  other  "User Library-WS2812-4020_6508:7"
  other  "User Library-WS2812-4020_6508:8"
  other  "User Library-WS2812-4020_6508:9"
  other  "User Library-WS2812-4020_6508:10"
  other  "User Library-Chip Cap_MLCC_0402 (1005)_6510:1"
  other  "User Library-Chip Cap_MLCC_0402 (1005)_6512:1"
  other  "User Library-Chip Cap_MLCC_0402 (1005)_6514:1"
  other  "User Library-Chip Cap_MLCC_0402 (1005)_6516:1"
  other  "User Library-Chip Cap_MLCC_0402 (1005)_6518:1"
  other  "User Library-Chip Cap_MLCC_0402 (1005)_6520:1"
  other  "CircuitWorks-SOT-23_6522:1"
  other  "User Library-User Library-res0402_res0402_body_6524:1"
  other  "B3U_1000P[]_6526:1"
  other  "CAPC0603_6528:1"
  other  "CAPC0603_6530:1"
  other  "CircuitWorks-SOT-223_6532:1"
  other  "User Library-LED SMD0603_6534:1"
  other  "User Library-LED SMD0603_6534:2"
  other  "User Library-LED SMD0603_6534:3"
  other  "User Library-LED SMD0603_6534:4"
  other  "User Library-LED SMD0603_6534:5"
  other  "User Library-LED SMD0603_6536:1"
  other  "User Library-LED SMD0603_6536:2"
  other  "User Library-LED SMD0603_6536:3"
  other  "User Library-LED SMD0603_6536:4"
  other  "User Library-LED SMD0603_6536:5"
  other  "User Library-User Library-res0402_res0402_body_6538:1"
  other  "User Library-LED SMD0603_6540:1"
  other  "User Library-LED SMD0603_6540:2"
  other  "User Library-LED SMD0603_6540:3"
  other  "User Library-LED SMD0603_6540:4"
  other  "User Library-LED SMD0603_6540:5"
  other  "User Library-LED SMD0603_6542:1"
  other  "User Library-LED SMD0603_6542:2"
  other  "User Library-LED SMD0603_6542:3"
  other  "User Library-LED SMD0603_6542:4"
  other  "User Library-LED SMD0603_6542:5"
  other  "User Library-LED SMD0603_6544:1"
  other  "User Library-LED SMD0603_6544:2"
  other  "User Library-LED SMD0603_6544:3"
  other  "User Library-LED SMD0603_6544:4"
  other  "User Library-LED SMD0603_6544:5"
  other  "User Library-LED SMD0603_6546:1"
  other  "User Library-LED SMD0603_6546:2"
  other  "User Library-LED SMD0603_6546:3"
  other  "User Library-LED SMD0603_6546:4"
  other  "User Library-LED SMD0603_6546:5"
  other  "User Library-User Library-res0402_res0402_body_6548:1"
  other  "User Library-LED SMD0603_6550:1"
  other  "User Library-LED SMD0603_6550:2"
  other  "User Library-LED SMD0603_6550:3"
  other  "User Library-LED SMD0603_6550:4"
  other  "User Library-LED SMD0603_6550:5"
  other  "User Library-LED SMD0603_6552:1"
  other  "User Library-LED SMD0603_6552:2"
  other  "User Library-LED SMD0603_6552:3"
  other  "User Library-LED SMD0603_6552:4"
  other  "User Library-LED SMD0603_6552:5"
  other  "User Library-User Library-res0402_res0402_body_6554:1"
  other  "User Library-User Library-res0402_res0402_body_6556:1"
  other  "User Library-LED SMD0603_6558:1"
  other  "User Library-LED SMD0603_6558:2"
  other  "User Library-LED SMD0603_6558:3"
  other  "User Library-LED SMD0603_6558:4"
  other  "User Library-LED SMD0603_6558:5"
  other  "User Library-User Library-res0402_res0402_body_6560:1"
  other  "User Library-Chip Cap_MLCC_0402 (1005)_6562:1"
  other  "User Library-Chip Cap_MLCC_0402 (1005)_6564:1"
  other  "User Library-Chip Cap_MLCC_0402 (1005)_6566:1"
  other  "User Library-Chip Cap_MLCC_0402 (1005)_6568:1"
  other  "User Library-Chip Cap_MLCC_0402 (1005)_6570:1"
  other  "User Library-Chip Cap_MLCC_0402 (1005)_6572:1"
  other  "User Library-Chip Cap_MLCC_0402 (1005)_6574:1"
  other  "User Library-Chip Cap_MLCC_0402 (1005)_6576:1"
  other  "User Library-Chip Cap_MLCC_0402 (1005)_6578:1"
  other  "User Library-Chip Cap_MLCC_0402 (1005)_6580:1"
  other  "User Library-Chip Cap_MLCC_0402 (1005)_6582:1"
  other  "User Library-Chip Cap_MLCC_0402 (1005)_6584:1"
  other  "User Library-Chip Cap_MLCC_0402 (1005)_6586:1"
  other  "User Library-Chip Cap_MLCC_0402 (1005)_6588:1"
  other  "User Library-Chip Cap_MLCC_0402 (1005)_6590:1"
  other  "User Library-Chip Cap_MLCC_0402 (1005)_6592:1"
  other  "User Library-Chip Cap_MLCC_0402 (1005)_6594:1"
  other  "User Library-Chip Cap_MLCC_0402 (1005)_6596:1"
  other  "User Library-Chip Cap_MLCC_0402 (1005)_6598:1"
  other  "User Library-Chip Cap_MLCC_0402 (1005)_6600:1"
  other  "User Library-Chip Cap_MLCC_0402 (1005)_6602:1"
  other  "User Library-Chip Cap_MLCC_0402 (1005)_6604:1"
  other  "User Library-Chip Cap_MLCC_0402 (1005)_6606:1"
  other  "User Library-Chip Cap_MLCC_0402 (1005)_6608:1"
  other  "User Library-Chip Cap_MLCC_0402 (1005)_6610:1"
  other  "User Library-Chip Cap_MLCC_0402 (1005)_6612:1"
  other  "User Library-Chip Cap_MLCC_0402 (1005)_6614:1"
  other  "GRM32ER71E226ME15L_6616:1"
  other  "GRM32ER71E226ME15L_6618:1"
  other  "GRM32ER71E226ME15L_6620:1"
  other  "GRM32ER71E226ME15L_6622:1"
  other  "User Library-Chip Cap_MLCC_0402 (1005)_6624:1"
  other  "GRM32ER71E226ME15L_6626:1"
  other  "GRM32ER71E226ME15L_6628:1"
  other  "GRM32ER71E226ME15L_6630:1"
  other  "GRM32ER71E226ME15L_6632:1"
  other  "User Library-Chip Cap_MLCC_0402 (1005)_6634:1"
  other  "User Library-Chip Cap_MLCC_0402 (1005)_6636:1"
  other  "GRM32ER71E226ME15L_6638:1"
  other  "User Library-Chip Cap_MLCC_0402 (1005)_6640:1"
  other  "User Library-Chip Cap_MLCC_0402 (1005)_6642:1"
  other  "GRM32ER71E226ME15L_6644:1"
  other  "GRM32ER71E226ME15L_6646:1"
  other  "GRM32ER71E226ME15L_6648:1"
  other  "User Library-Chip Cap_MLCC_0402 (1005)_6650:1"
  other  "User Library-Chip Cap_MLCC_0402 (1005)_6652:1"
  other  "GRM32ER71E226ME15L_6654:1"
  other  "GRM32ER71E226ME15L_6656:1"
  other  "GRM32ER71E226ME15L_6658:1"
  other  "GRM32ER71E226ME15L_6660:1"
  other  "User Library-Chip Cap_MLCC_0402 (1005)_6662:1"
  other  "User Library-Chip Cap_MLCC_0402 (1005)_6664:1"
  other  "User Library-Chip Cap_MLCC_0402 (1005)_6666:1"
  other  "User Library-Chip Cap_MLCC_0402 (1005)_6668:1"
  other  "User Library-Chip Cap_MLCC_0402 (1005)_6670:1"
  other  "User Library-Chip Cap_MLCC_0402 (1005)_6672:1"
  other  "User Library-Chip Cap_MLCC_0402 (1005)_6674:1"
  other  "User Library-Chip Cap_MLCC_0402 (1005)_6676:1"
  other  "User Library-Chip Cap_MLCC_0402 (1005)_6678:1"
  other  "User Library-Chip Cap_MLCC_0402 (1005)_6680:1"
  other  "User Library-Chip Cap_MLCC_0402 (1005)_6682:1"
  other  "User Library-Chip Cap_MLCC_0402 (1005)_6684:1"
  other  "User Library-Chip Cap_MLCC_0402 (1005)_6686:1"
  other  "User Library-Chip Cap_MLCC_0402 (1005)_6688:1"
  other  "User Library-Chip Cap_MLCC_0402 (1005)_6690:1"
  other  "User Library-Chip Cap_MLCC_0402 (1005)_6692:1"
  other  "User Library-Chip Cap_MLCC_0402 (1005)_6694:1"
  other  "User Library-Chip Cap_MLCC_0402 (1005)_6696:1"
  other  "User Library-Chip Cap_MLCC_0402 (1005)_6698:1"
  other  "User Library-Chip Cap_MLCC_0402 (1005)_6700:1"
  other  "CAPC0603_6702:1"
  other  "CAPC0603_6704:1"
  other  "User Library-Chip Cap_MLCC_0402 (1005)_6706:1"
  other  "User Library-Chip Cap_MLCC_0402 (1005)_6708:1"
  other  "User Library-GeyerElectronics_KX7_6710:1"
  other  "User Library-GeyerElectronics_KX7_6710:2"
  other  "User Library-GeyerElectronics_KX7_6710:3"
  other  "User Library-GeyerElectronics_KX7_6710:4"
  other  "User Library-640456-4_6712:1"
  other  "User Library-640456-4_6713:1"
  other  "Open CASCADE STEP translator 7.5 5.128.1.1_6715:1"
  other  "B2B-PH-K-S_6719:1"
  other  "User Library-2047110001_6721:1"
  other  "User Library-2047110001_6723:1"
  other  "86A--3DModel-STEP-56544_6725:1"
  other  "86A--3DModel-STEP-56544_6725:2"
  other  "86A--3DModel-STEP-56544_6725:3"
  other  "86A--3DModel-STEP-56544_6725:4"
  other  "86A--3DModel-STEP-56544_6727:1"
  other  "86A--3DModel-STEP-56544_6727:2"
  other  "86A--3DModel-STEP-56544_6727:3"
  other  "86A--3DModel-STEP-56544_6727:4"
  other  "User Library-LED SMD0603_6729:1"
  other  "User Library-LED SMD0603_6729:2"
  other  "User Library-LED SMD0603_6729:3"
  other  "User Library-LED SMD0603_6729:4"
  other  "User Library-LED SMD0603_6729:5"
  other  "User Library-LED SMD0603_6731:1"
  other  "User Library-LED SMD0603_6731:2"
  other  "User Library-LED SMD0603_6731:3"
  other  "User Library-LED SMD0603_6731:4"
  other  "User Library-LED SMD0603_6731:5"
  other  "User Library-SOD323F-1_6733:1"
  other  "B3U_1000P[]_6735:1"
  other  "User Library-IT-1187_6737:1"
  other  "User Library-IT-1187_6739:1"
  other  "push-fit_6741:1"
  other  "Linit Switch_6742:1"
  other  "Linit Switch_6742:2"
  other  "Linit Switch_6742:3"
  other  "Linit Switch_6742:4"
  other  "push-fit_6741:2"
  other  "Linit Switch_6742:5"
  other  "Linit Switch_6742:6"
  other  "Linit Switch_6742:7"
  other  "Linit Switch_6742:8"
  other  "User Library-IT-1187_6747:1"
  other  "User Library-IT-1187_6749:1"
  other  "User Library-User Library-res0402_res0402_body_6751:1"
  other  "User Library-User Library-res0402_res0402_body_6753:1"
  other  "User Library-User Library-res0402_res0402_body_6755:1"
  other  "User Library-User Library-res0402_res0402_body_6757:1"
  other  "User Library-User Library-res0402_res0402_body_6759:1"
  other  "User Library-User Library-res0402_res0402_body_6761:1"
  other  "User Library-User Library-res0402_res0402_body_6763:1"
  other  "User Library-User Library-res0402_res0402_body_6765:1"
  other  "User Library-User Library-res0402_res0402_body_6767:1"
  other  "User Library-User Library-res0402_res0402_body_6769:1"
  other  "User Library-User Library-res0402_res0402_body_6771:1"
  other  "User Library-User Library-res0402_res0402_body_6773:1"
  other  "User Library-User Library-res0402_res0402_body_6775:1"
  other  "User Library-User Library-res0402_res0402_body_6777:1"
  other  "User Library-User Library-res0402_res0402_body_6779:1"
  other  "User Library-User Library-res0402_res0402_body_6781:1"
  other  "User Library-User Library-res0402_res0402_body_6783:1"
  other  "User Library-User Library-res0402_res0402_body_6785:1"
  other  "User Library-User Library-res0402_res0402_body_6787:1"
  other  "User Library-User Library-res0402_res0402_body_6789:1"
  other  "User Library-User Library-res0402_res0402_body_6791:1"
  other  "User Library-User Library-res0402_res0402_body_6793:1"
  other  "User Library-User Library-res0402_res0402_body_6795:1"
  other  "User Library-User Library-res0402_res0402_body_6797:1"
  other  "User Library-User Library-res0402_res0402_body_6799:1"
  other  "User Library-User Library-res0402_res0402_body_6801:1"
  other  "User Library-User Library-res0402_res0402_body_6803:1"
  other  "User Library-User Library-res0402_res0402_body_6805:1"
  other  "User Library-User Library-res0402_res0402_body_6807:1"
  other  "User Library-User Library-res0402_res0402_body_6809:1"
  other  "User Library-User Library-res0402_res0402_body_6811:1"
  other  "User Library-User Library-res0402_res0402_body_6813:1"
  other  "User Library-User Library-res0402_res0402_body_6815:1"
  other  "User Library-User Library-res0402_res0402_body_6817:1"
  other  "User Library-741C083_6819:1"
  other  "User Library-741C083_6819:2"
  other  "User Library-User Library-res0402_res0402_body_6821:1"
  other  "User Library-User Library-res0402_res0402_body_6823:1"
  other  "User Library-User Library-res0402_res0402_body_6825:1"
  other  "User Library-User Library-res0402_res0402_body_6827:1"
  other  "User Library-User Library-res0402_res0402_body_6829:1"
  other  "User Library-User Library-res0402_res0402_body_6831:1"
  other  "User Library-User Library-res0402_res0402_body_6833:1"
  other  "User Library-User Library-res0402_res0402_body_6835:1"
  other  "User Library-User Library-res0402_res0402_body_6837:1"
  other  "User Library-User Library-res0402_res0402_body_6839:1"
  other  "User Library-User Library-res0402_res0402_body_6841:1"
  other  "User Library-User Library-res0402_res0402_body_6843:1"
  other  "User Library-User Library-res0402_res0402_body_6845:1"
  other  "User Library-User Library-res0402_res0402_body_6847:1"
  other  "User Library-User Library-res0402_res0402_body_6849:1"
  other  "User Library-User Library-res0402_res0402_body_6851:1"
  other  "User Library-User Library-res0402_res0402_body_6853:1"
  other  "User Library-741C083_6855:1"
  other  "User Library-741C083_6855:2"
  other  "User Library-741C083_6857:1"
  other  "User Library-741C083_6857:2"
  other  "User Library-User Library-res0402_res0402_body_6859:1"
  other  "User Library-741C083_6861:1"
  other  "User Library-741C083_6861:2"
  other  "User Library-741C083_6863:1"
  other  "User Library-741C083_6863:2"
  other  "User Library-741C083_6865:1"
  other  "User Library-741C083_6865:2"
  other  "User Library-741C083_6867:1"
  other  "User Library-741C083_6867:2"
  other  "User Library-741C083_6869:1"
  other  "User Library-741C083_6869:2"
  other  "User Library-User Library-res0402_res0402_body_6871:1"
  other  "User Library-User Library-res0402_res0402_body_6873:1"
  other  "User Library-User Library-res0402_res0402_body_6875:1"
  other  "User Library-User Library-res0402_res0402_body_6877:1"
  other  "User Library-User Library-res0402_res0402_body_6879:1"
  other  "User Library-User Library-res0402_res0402_body_6881:1"
  other  "User Library-User Library-res0402_res0402_body_6883:1"
  other  "User Library-Bourns_SRP1038A_series_CASE-Non-Lead-Frame_6885:1"
  other  "User Library-Bourns_SRP1038A_series_CASE-Non-Lead-Frame_6885:2"
  other  "User Library-Bourns_SRP1038A_series_CASE-Non-Lead-Frame_6885:3"
  other  "User Library-Bourns_SRP1038A_series_CASE-Non-Lead-Frame_6887:1"
  other  "User Library-Bourns_SRP1038A_series_CASE-Non-Lead-Frame_6887:2"
  other  "User Library-Bourns_SRP1038A_series_CASE-Non-Lead-Frame_6887:3"
  other  "User Library-WS2812-4020_6889:1"
  other  "User Library-WS2812-4020_6889:2"
  other  "User Library-WS2812-4020_6889:3"
  other  "User Library-WS2812-4020_6889:4"
  other  "User Library-WS2812-4020_6889:5"
  other  "User Library-WS2812-4020_6889:6"
  other  "User Library-WS2812-4020_6889:7"
  other  "User Library-WS2812-4020_6889:8"
  other  "User Library-WS2812-4020_6889:9"
  other  "User Library-WS2812-4020_6889:10"
  other  "User Library-WS2812-4020_6891:1"
  other  "User Library-WS2812-4020_6891:2"
  other  "User Library-WS2812-4020_6891:3"
  other  "User Library-WS2812-4020_6891:4"
  other  "User Library-WS2812-4020_6891:5"
  other  "User Library-WS2812-4020_6891:6"
  other  "User Library-WS2812-4020_6891:7"
  other  "User Library-WS2812-4020_6891:8"
  other  "User Library-WS2812-4020_6891:9"
  other  "User Library-WS2812-4020_6891:10"
  other  "User Library-WS2812-4020_6893:1"
  other  "User Library-WS2812-4020_6893:2"
  other  "User Library-WS2812-4020_6893:3"
  other  "User Library-WS2812-4020_6893:4"
  other  "User Library-WS2812-4020_6893:5"
  other  "User Library-WS2812-4020_6893:6"
  other  "User Library-WS2812-4020_6893:7"
  other  "User Library-WS2812-4020_6893:8"
  other  "User Library-WS2812-4020_6893:9"
  other  "User Library-WS2812-4020_6893:10"
  other  "User Library-WS2812-4020_6895:1"
  other  "User Library-WS2812-4020_6895:2"
  other  "User Library-WS2812-4020_6895:3"
  other  "User Library-WS2812-4020_6895:4"
  other  "User Library-WS2812-4020_6895:5"
  other  "User Library-WS2812-4020_6895:6"
  other  "User Library-WS2812-4020_6895:7"
  other  "User Library-WS2812-4020_6895:8"
  other  "User Library-WS2812-4020_6895:9"
  other  "User Library-WS2812-4020_6895:10"
  other  "User Library-WS2812-4020_6897:1"
  other  "User Library-WS2812-4020_6897:2"
  other  "User Library-WS2812-4020_6897:3"
  other  "User Library-WS2812-4020_6897:4"
  other  "User Library-WS2812-4020_6897:5"
  other  "User Library-WS2812-4020_6897:6"
  other  "User Library-WS2812-4020_6897:7"
  other  "User Library-WS2812-4020_6897:8"
  other  "User Library-WS2812-4020_6897:9"
  other  "User Library-WS2812-4020_6897:10"
  other  "User Library-WS2812-4020_6899:1"
  other  "User Library-WS2812-4020_6899:2"
  other  "User Library-WS2812-4020_6899:3"
  other  "User Library-WS2812-4020_6899:4"
  other  "User Library-WS2812-4020_6899:5"
  other  "User Library-WS2812-4020_6899:6"
  other  "User Library-WS2812-4020_6899:7"
  other  "User Library-WS2812-4020_6899:8"
  other  "User Library-WS2812-4020_6899:9"
  other  "User Library-WS2812-4020_6899:10"
  other  "User Library-WS2812-4020_6901:1"
  other  "User Library-WS2812-4020_6901:2"
  other  "User Library-WS2812-4020_6901:3"
  other  "User Library-WS2812-4020_6901:4"
  other  "User Library-WS2812-4020_6901:5"
  other  "User Library-WS2812-4020_6901:6"
  other  "User Library-WS2812-4020_6901:7"
  other  "User Library-WS2812-4020_6901:8"
  other  "User Library-WS2812-4020_6901:9"
  other  "User Library-WS2812-4020_6901:10"
  other  "User Library-WS2812-4020_6903:1"
  other  "User Library-WS2812-4020_6903:2"
  other  "User Library-WS2812-4020_6903:3"
  other  "User Library-WS2812-4020_6903:4"
  other  "User Library-WS2812-4020_6903:5"
  other  "User Library-WS2812-4020_6903:6"
  other  "User Library-WS2812-4020_6903:7"
  other  "User Library-WS2812-4020_6903:8"
  other  "User Library-WS2812-4020_6903:9"
  other  "User Library-WS2812-4020_6903:10"
  other  "User Library-WS2812-4020_6905:1"
  other  "User Library-WS2812-4020_6905:2"
  other  "User Library-WS2812-4020_6905:3"
  other  "User Library-WS2812-4020_6905:4"
  other  "User Library-WS2812-4020_6905:5"
  other  "User Library-WS2812-4020_6905:6"
  other  "User Library-WS2812-4020_6905:7"
  other  "User Library-WS2812-4020_6905:8"
  other  "User Library-WS2812-4020_6905:9"
  other  "User Library-WS2812-4020_6905:10"
  other  "User Library-WS2812-4020_6907:1"
  other  "User Library-WS2812-4020_6907:2"
  other  "User Library-WS2812-4020_6907:3"
  other  "User Library-WS2812-4020_6907:4"
  other  "User Library-WS2812-4020_6907:5"
  other  "User Library-WS2812-4020_6907:6"
  other  "User Library-WS2812-4020_6907:7"
  other  "User Library-WS2812-4020_6907:8"
  other  "User Library-WS2812-4020_6907:9"
  other  "User Library-WS2812-4020_6907:10"
  other  "User Library-WS2812-4020_6909:1"
  other  "User Library-WS2812-4020_6909:2"
  other  "User Library-WS2812-4020_6909:3"
  other  "User Library-WS2812-4020_6909:4"
  other  "User Library-WS2812-4020_6909:5"
  other  "User Library-WS2812-4020_6909:6"
  other  "User Library-WS2812-4020_6909:7"
  other  "User Library-WS2812-4020_6909:8"
  other  "User Library-WS2812-4020_6909:9"
  other  "User Library-WS2812-4020_6909:10"
  other  "User Library-WS2812-4020_6911:1"
  other  "User Library-WS2812-4020_6911:2"
  other  "User Library-WS2812-4020_6911:3"
  other  "User Library-WS2812-4020_6911:4"
  other  "User Library-WS2812-4020_6911:5"
  other  "User Library-WS2812-4020_6911:6"
  other  "User Library-WS2812-4020_6911:7"
  other  "User Library-WS2812-4020_6911:8"
  other  "User Library-WS2812-4020_6911:9"
  other  "User Library-WS2812-4020_6911:10"
  other  "User Library-WS2812-4020_6913:1"
  other  "User Library-WS2812-4020_6913:2"
  other  "User Library-WS2812-4020_6913:3"
  other  "User Library-WS2812-4020_6913:4"
  other  "User Library-WS2812-4020_6913:5"
  other  "User Library-WS2812-4020_6913:6"
  other  "User Library-WS2812-4020_6913:7"
  other  "User Library-WS2812-4020_6913:8"
  other  "User Library-WS2812-4020_6913:9"
  other  "User Library-WS2812-4020_6913:10"
  other  "User Library-WS2812-4020_6915:1"
  other  "User Library-WS2812-4020_6915:2"
  other  "User Library-WS2812-4020_6915:3"
  other  "User Library-WS2812-4020_6915:4"
  other  "User Library-WS2812-4020_6915:5"
  other  "User Library-WS2812-4020_6915:6"
  other  "User Library-WS2812-4020_6915:7"
  other  "User Library-WS2812-4020_6915:8"
  other  "User Library-WS2812-4020_6915:9"
  other  "User Library-WS2812-4020_6915:10"
  other  "User Library-WS2812-4020_6917:1"
  other  "User Library-WS2812-4020_6917:2"
  other  "User Library-WS2812-4020_6917:3"
  other  "User Library-WS2812-4020_6917:4"
  other  "User Library-WS2812-4020_6917:5"
  other  "User Library-WS2812-4020_6917:6"
  other  "User Library-WS2812-4020_6917:7"
  other  "User Library-WS2812-4020_6917:8"
  other  "User Library-WS2812-4020_6917:9"
  other  "User Library-WS2812-4020_6917:10"
  other  "User Library-WS2812-4020_6919:1"
  other  "User Library-WS2812-4020_6919:2"
  other  "User Library-WS2812-4020_6919:3"
  other  "User Library-WS2812-4020_6919:4"
  other  "User Library-WS2812-4020_6919:5"
  other  "User Library-WS2812-4020_6919:6"
  other  "User Library-WS2812-4020_6919:7"
  other  "User Library-WS2812-4020_6919:8"
  other  "User Library-WS2812-4020_6919:9"
  other  "User Library-WS2812-4020_6919:10"
  other  "User Library-WS2812-4020_6921:1"
  other  "User Library-WS2812-4020_6921:2"
  other  "User Library-WS2812-4020_6921:3"
  other  "User Library-WS2812-4020_6921:4"
  other  "User Library-WS2812-4020_6921:5"
  other  "User Library-WS2812-4020_6921:6"
  other  "User Library-WS2812-4020_6921:7"
  other  "User Library-WS2812-4020_6921:8"
  other  "User Library-WS2812-4020_6921:9"
  other  "User Library-WS2812-4020_6921:10"
  other  "User Library-WS2812-4020_6923:1"
  other  "User Library-WS2812-4020_6923:2"
  other  "User Library-WS2812-4020_6923:3"
  other  "User Library-WS2812-4020_6923:4"
  other  "User Library-WS2812-4020_6923:5"
  other  "User Library-WS2812-4020_6923:6"
  other  "User Library-WS2812-4020_6923:7"
  other  "User Library-WS2812-4020_6923:8"
  other  "User Library-WS2812-4020_6923:9"
  other  "User Library-WS2812-4020_6923:10"
  other  "User Library-WS2812-4020_6925:1"
  other  "User Library-WS2812-4020_6925:2"
  other  "User Library-WS2812-4020_6925:3"
  other  "User Library-WS2812-4020_6925:4"
  other  "User Library-WS2812-4020_6925:5"
  other  "User Library-WS2812-4020_6925:6"
  other  "User Library-WS2812-4020_6925:7"
  other  "User Library-WS2812-4020_6925:8"
  other  "User Library-WS2812-4020_6925:9"
  other  "User Library-WS2812-4020_6925:10"
  other  "User Library-WS2812-4020_6927:1"
  other  "User Library-WS2812-4020_6927:2"
  other  "User Library-WS2812-4020_6927:3"
  other  "User Library-WS2812-4020_6927:4"
  other  "User Library-WS2812-4020_6927:5"
  other  "User Library-WS2812-4020_6927:6"
  other  "User Library-WS2812-4020_6927:7"
  other  "User Library-WS2812-4020_6927:8"
  other  "User Library-WS2812-4020_6927:9"
  other  "User Library-WS2812-4020_6927:10"
  other  "User Library-WS2812-4020_6929:1"
  other  "User Library-WS2812-4020_6929:2"
  other  "User Library-WS2812-4020_6929:3"
  other  "User Library-WS2812-4020_6929:4"
  other  "User Library-WS2812-4020_6929:5"
  other  "User Library-WS2812-4020_6929:6"
  other  "User Library-WS2812-4020_6929:7"
  other  "User Library-WS2812-4020_6929:8"
  other  "User Library-WS2812-4020_6929:9"
  other  "User Library-WS2812-4020_6929:10"
  other  "User Library-WS2812-4020_6931:1"
  other  "User Library-WS2812-4020_6931:2"
  other  "User Library-WS2812-4020_6931:3"
  other  "User Library-WS2812-4020_6931:4"
  other  "User Library-WS2812-4020_6931:5"
  other  "User Library-WS2812-4020_6931:6"
  other  "User Library-WS2812-4020_6931:7"
  other  "User Library-WS2812-4020_6931:8"
  other  "User Library-WS2812-4020_6931:9"
  other  "User Library-WS2812-4020_6931:10"
  other  "User Library-WS2812-4020_6933:1"
  other  "User Library-WS2812-4020_6933:2"
  other  "User Library-WS2812-4020_6933:3"
  other  "User Library-WS2812-4020_6933:4"
  other  "User Library-WS2812-4020_6933:5"
  other  "User Library-WS2812-4020_6933:6"
  other  "User Library-WS2812-4020_6933:7"
  other  "User Library-WS2812-4020_6933:8"
  other  "User Library-WS2812-4020_6933:9"
  other  "User Library-WS2812-4020_6933:10"
  other  "User Library-WS2812-4020_6935:1"
  other  "User Library-WS2812-4020_6935:2"
  other  "User Library-WS2812-4020_6935:3"
  other  "User Library-WS2812-4020_6935:4"
  other  "User Library-WS2812-4020_6935:5"
  other  "User Library-WS2812-4020_6935:6"
  other  "User Library-WS2812-4020_6935:7"
  other  "User Library-WS2812-4020_6935:8"
  other  "User Library-WS2812-4020_6935:9"
  other  "User Library-WS2812-4020_6935:10"
  other  "User Library-QFN24_4x4x0_75_p0_5_6937:1"
  other  "MC33926 8X8X2_6939:1"
  other  "MC33926 8X8X2_6939:2"
  other  "MC33926 8X8X2_6939:3"
  other  "MC33926 8X8X2_6939:4"
  other  "MC33926 8X8X2_6939:5"
  other  "MC33926 8X8X2_6939:6"
  other  "MC33926 8X8X2_6939:7"
  other  "MC33926 8X8X2_6939:8"
  other  "MC33926 8X8X2_6939:9"
  other  "MC33926 8X8X2_6939:10"
  other  "MC33926 8X8X2_6939:11"
  other  "MC33926 8X8X2_6939:12"
  other  "MC33926 8X8X2_6939:13"
  other  "MC33926 8X8X2_6939:14"
  other  "MC33926 8X8X2_6939:15"
  other  "MC33926 8X8X2_6939:16"
  other  "MC33926 8X8X2_6939:17"
  other  "MC33926 8X8X2_6939:18"
  other  "MC33926 8X8X2_6939:19"
  other  "MC33926 8X8X2_6939:20"
  other  "MC33926 8X8X2_6939:21"
  other  "MC33926 8X8X2_6939:22"
  other  "MC33926 8X8X2_6939:23"
  other  "MC33926 8X8X2_6939:24"
  other  "MC33926 8X8X2_6939:25"
  other  "MC33926 8X8X2_6939:26"
  other  "MC33926 8X8X2_6939:27"
  other  "MC33926 8X8X2_6939:28"
  other  "MC33926 8X8X2_6939:29"
  other  "MC33926 8X8X2_6939:30"
  other  "MC33926 8X8X2_6939:31"
  other  "MC33926 8X8X2_6939:32"
  other  "MC33926 8X8X2_6939:33"
  other  "MC33926 8X8X2_6941:1"
  other  "MC33926 8X8X2_6941:2"
  other  "MC33926 8X8X2_6941:3"
  other  "MC33926 8X8X2_6941:4"
  other  "MC33926 8X8X2_6941:5"
  other  "MC33926 8X8X2_6941:6"
  other  "MC33926 8X8X2_6941:7"
  other  "MC33926 8X8X2_6941:8"
  other  "MC33926 8X8X2_6941:9"
  other  "MC33926 8X8X2_6941:10"
  other  "MC33926 8X8X2_6941:11"
  other  "MC33926 8X8X2_6941:12"
  other  "MC33926 8X8X2_6941:13"
  other  "MC33926 8X8X2_6941:14"
  other  "MC33926 8X8X2_6941:15"
  other  "MC33926 8X8X2_6941:16"
  other  "MC33926 8X8X2_6941:17"
  other  "MC33926 8X8X2_6941:18"
  other  "MC33926 8X8X2_6941:19"
  other  "MC33926 8X8X2_6941:20"
  other  "MC33926 8X8X2_6941:21"
  other  "MC33926 8X8X2_6941:22"
  other  "MC33926 8X8X2_6941:23"
  other  "MC33926 8X8X2_6941:24"
  other  "MC33926 8X8X2_6941:25"
  other  "MC33926 8X8X2_6941:26"
  other  "MC33926 8X8X2_6941:27"
  other  "MC33926 8X8X2_6941:28"
  other  "MC33926 8X8X2_6941:29"
  other  "MC33926 8X8X2_6941:30"
  other  "MC33926 8X8X2_6941:31"
  other  "MC33926 8X8X2_6941:32"
  other  "MC33926 8X8X2_6941:33"
  other  "BODY-SON_6943:1"
  other  "Open CASCADE STEP translator 7.5 5.240.1.2.1_6944:1"
  other  "Open CASCADE STEP translator 7.5 5.240.1.2.2_6945:1"
  other  "Open CASCADE STEP translator 7.5 5.240.1.2.3_6946:1"
  other  "Open CASCADE STEP translator 7.5 5.240.1.2.4_6947:1"
  other  "Open CASCADE STEP translator 7.5 5.240.1.2.5_6948:1"
  other  "Open CASCADE STEP translator 7.5 5.240.1.2.6_6949:1"
  other  "Open CASCADE STEP translator 7.5 5.240.1.2.7_6950:1"
  other  "Open CASCADE STEP translator 7.5 5.240.1.2.8_6951:1"
  other  "Open CASCADE STEP translator 7.5 5.240.1.2.9_6952:1"
  other  "Open CASCADE STEP translator 7.5 5.240.1.2.10_6953:1"
  other  "Open CASCADE STEP translator 7.5 5.240.1.2.11_6954:1"
  other  "BODY-SON_6943:2"
  other  "Open CASCADE STEP translator 7.5 5.240.1.2.1_6944:2"
  other  "Open CASCADE STEP translator 7.5 5.240.1.2.2_6945:2"
  other  "Open CASCADE STEP translator 7.5 5.240.1.2.3_6946:2"
  other  "Open CASCADE STEP translator 7.5 5.240.1.2.4_6947:2"
  other  "Open CASCADE STEP translator 7.5 5.240.1.2.5_6948:2"
  other  "Open CASCADE STEP translator 7.5 5.240.1.2.6_6949:2"
  other  "Open CASCADE STEP translator 7.5 5.240.1.2.7_6950:2"
  other  "Open CASCADE STEP translator 7.5 5.240.1.2.8_6951:2"
  other  "Open CASCADE STEP translator 7.5 5.240.1.2.9_6952:2"
  other  "Open CASCADE STEP translator 7.5 5.240.1.2.10_6953:2"
  other  "Open CASCADE STEP translator 7.5 5.240.1.2.11_6954:2"
  other  "User Library-SOT353-1-1_6961:1"
  other  "User Library-SOT353-1-1_6961:2"
  other  "User Library-SOT353-1-1_6961:3"
  other  "User Library-SOT353-1-1_6961:4"
  other  "User Library-SOT353-1-1_6961:5"
  other  "User Library-SOT353-1-1_6961:6"
  extrude  "Extruded_6963:1"  [1 undecoded]
  extrude  "Extruded_6966:1"  [1 undecoded]
  other  "128x32-OLED_6969:1"
  other  "Составной1"
  other  "SRF1"
note: 2 required parameter values undecoded (feature->parameter linkage not recoverable at this tier; creation-order binding heuristic only, values carry confidence <= 0.55)
